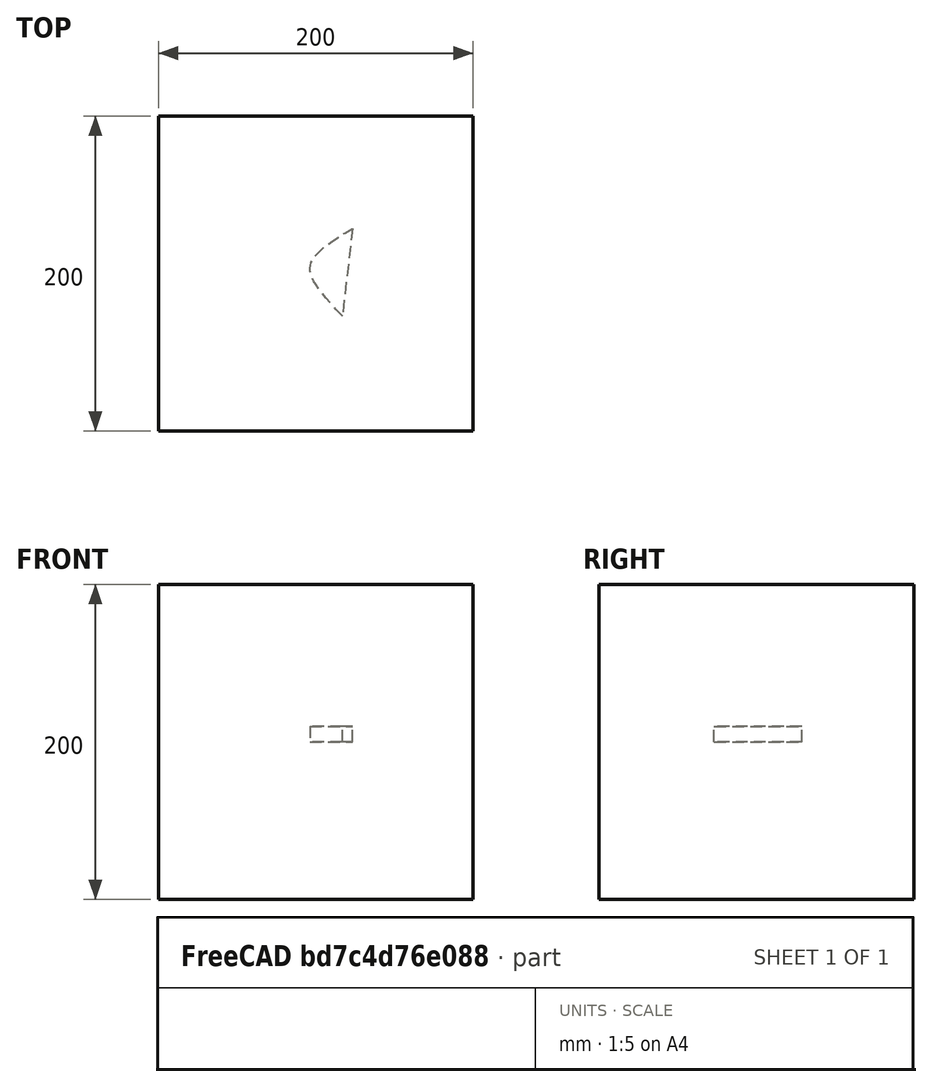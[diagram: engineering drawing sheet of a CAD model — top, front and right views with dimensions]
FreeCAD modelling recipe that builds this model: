
FCSTD DOCUMENT  (FreeCAD 1.0R39109 (Git))
Label: extrudedHyperbola
License: All rights reserved
LicenseURL: http://en.wikipedia.org/wiki/All_rights_reserved
objects: App::DocumentObjectGroupPython×1248, App::Part×2, Part::FeaturePython×1, Sketcher::SketchObject×1, Part::Extrusion×1
note: 4 computed .brp shape members not serialized (recipe doc carries the construction recipe); baked Part::Feature solids carry a one-line shape summary decoded from their .brp

FEATURE [App::DocumentObjectGroupPython] HALFPI  # scripted group (container) (typed FeaturePython)
  name = HALFPI
  value = pi/2.
FEATURE [App::DocumentObjectGroupPython] PI  # scripted group (container) (typed FeaturePython)
  name = PI
  value = 1.*pi
FEATURE [App::DocumentObjectGroupPython] TWOPI  # scripted group (container) (typed FeaturePython)
  name = TWOPI
  value = 2.*pi
FEATURE [App::DocumentObjectGroupPython] Constants  # scripted group (container) (typed FeaturePython)
  Group = -> [HALFPI,PI,TWOPI]
FEATURE [App::DocumentObjectGroupPython] Variables  # scripted group (container) (typed FeaturePython)
FEATURE [App::DocumentObjectGroupPython] Quantities  # scripted group (container) (typed FeaturePython)
FEATURE [App::DocumentObjectGroupPython] Isotopes  # scripted group (container) (typed FeaturePython)
FEATURE [App::DocumentObjectGroupPython] Elements  # scripted group (container) (typed FeaturePython)
FEATURE [App::DocumentObjectGroupPython] G4Isotopes  # scripted group (container) (typed FeaturePython)
FEATURE [App::DocumentObjectGroupPython] H_element  # scripted group (container) (typed FeaturePython)
  Z = 1
  atom_value = 1.008
  formula = H
  name = H_element
FEATURE [App::DocumentObjectGroupPython] He_element  # scripted group (container) (typed FeaturePython)
  Z = 2
  atom_value = 4.0026
  formula = He
  name = He_element
FEATURE [App::DocumentObjectGroupPython] Li_element  # scripted group (container) (typed FeaturePython)
  Z = 3
  atom_value = 6.94
  formula = Li
  name = Li_element
FEATURE [App::DocumentObjectGroupPython] Be_element  # scripted group (container) (typed FeaturePython)
  Z = 4
  atom_value = 9.01218
  formula = Be
  name = Be_element
FEATURE [App::DocumentObjectGroupPython] B_element  # scripted group (container) (typed FeaturePython)
  Z = 5
  atom_value = 10.81
  formula = B
  name = B_element
FEATURE [App::DocumentObjectGroupPython] C_element  # scripted group (container) (typed FeaturePython)
  Z = 6
  atom_value = 12.011
  formula = C
  name = C_element
FEATURE [App::DocumentObjectGroupPython] N_element  # scripted group (container) (typed FeaturePython)
  Z = 7
  atom_value = 14.007
  formula = N
  name = N_element
FEATURE [App::DocumentObjectGroupPython] O_element  # scripted group (container) (typed FeaturePython)
  Z = 8
  atom_value = 15.999
  formula = O
  name = O_element
FEATURE [App::DocumentObjectGroupPython] F_element  # scripted group (container) (typed FeaturePython)
  Z = 9
  atom_value = 18.9984
  formula = F
  name = F_element
FEATURE [App::DocumentObjectGroupPython] Ne_element  # scripted group (container) (typed FeaturePython)
  Z = 10
  atom_value = 20.1797
  formula = Ne
  name = Ne_element
FEATURE [App::DocumentObjectGroupPython] Na_element  # scripted group (container) (typed FeaturePython)
  Z = 11
  atom_value = 22.9898
  formula = Na
  name = Na_element
FEATURE [App::DocumentObjectGroupPython] Mg_element  # scripted group (container) (typed FeaturePython)
  Z = 12
  atom_value = 24.305
  formula = Mg
  name = Mg_element
FEATURE [App::DocumentObjectGroupPython] Al_element  # scripted group (container) (typed FeaturePython)
  Z = 13
  atom_value = 26.9815
  formula = Al
  name = Al_element
FEATURE [App::DocumentObjectGroupPython] Si_element  # scripted group (container) (typed FeaturePython)
  Z = 14
  atom_value = 28.085
  formula = Si
  name = Si_element
FEATURE [App::DocumentObjectGroupPython] P_element  # scripted group (container) (typed FeaturePython)
  Z = 15
  atom_value = 30.9738
  formula = P
  name = P_element
FEATURE [App::DocumentObjectGroupPython] S_element  # scripted group (container) (typed FeaturePython)
  Z = 16
  atom_value = 32.06
  formula = S
  name = S_element
FEATURE [App::DocumentObjectGroupPython] Cl_element  # scripted group (container) (typed FeaturePython)
  Z = 17
  atom_value = 35.45
  formula = Cl
  name = Cl_element
FEATURE [App::DocumentObjectGroupPython] Ar_element  # scripted group (container) (typed FeaturePython)
  Z = 18
  atom_value = 39.95
  formula = Ar
  name = Ar_element
FEATURE [App::DocumentObjectGroupPython] K_element  # scripted group (container) (typed FeaturePython)
  Z = 19
  atom_value = 39.0983
  formula = K
  name = K_element
FEATURE [App::DocumentObjectGroupPython] Ca_element  # scripted group (container) (typed FeaturePython)
  Z = 20
  atom_value = 40.078
  formula = Ca
  name = Ca_element
FEATURE [App::DocumentObjectGroupPython] Sc_element  # scripted group (container) (typed FeaturePython)
  Z = 21
  atom_value = 44.9559
  formula = Sc
  name = Sc_element
FEATURE [App::DocumentObjectGroupPython] Ti_element  # scripted group (container) (typed FeaturePython)
  Z = 22
  atom_value = 47.867
  formula = Ti
  name = Ti_element
FEATURE [App::DocumentObjectGroupPython] V_element  # scripted group (container) (typed FeaturePython)
  Z = 23
  atom_value = 50.9415
  formula = V
  name = V_element
FEATURE [App::DocumentObjectGroupPython] Cr_element  # scripted group (container) (typed FeaturePython)
  Z = 24
  atom_value = 51.9961
  formula = Cr
  name = Cr_element
FEATURE [App::DocumentObjectGroupPython] Mn_element  # scripted group (container) (typed FeaturePython)
  Z = 25
  atom_value = 54.938
  formula = Mn
  name = Mn_element
FEATURE [App::DocumentObjectGroupPython] Fe_element  # scripted group (container) (typed FeaturePython)
  Z = 26
  atom_value = 55.845
  formula = Fe
  name = Fe_element
FEATURE [App::DocumentObjectGroupPython] Co_element  # scripted group (container) (typed FeaturePython)
  Z = 27
  atom_value = 58.9332
  formula = Co
  name = Co_element
FEATURE [App::DocumentObjectGroupPython] Ni_element  # scripted group (container) (typed FeaturePython)
  Z = 28
  atom_value = 58.6934
  formula = Ni
  name = Ni_element
FEATURE [App::DocumentObjectGroupPython] Cu_element  # scripted group (container) (typed FeaturePython)
  Z = 29
  atom_value = 63.546
  formula = Cu
  name = Cu_element
FEATURE [App::DocumentObjectGroupPython] Zn_element  # scripted group (container) (typed FeaturePython)
  Z = 30
  atom_value = 65.38
  formula = Zn
  name = Zn_element
FEATURE [App::DocumentObjectGroupPython] Ga_element  # scripted group (container) (typed FeaturePython)
  Z = 31
  atom_value = 69.723
  formula = Ga
  name = Ga_element
FEATURE [App::DocumentObjectGroupPython] Ge_element  # scripted group (container) (typed FeaturePython)
  Z = 32
  atom_value = 72.63
  formula = Ge
  name = Ge_element
FEATURE [App::DocumentObjectGroupPython] As_element  # scripted group (container) (typed FeaturePython)
  Z = 33
  atom_value = 74.9216
  formula = As
  name = As_element
FEATURE [App::DocumentObjectGroupPython] Se_element  # scripted group (container) (typed FeaturePython)
  Z = 34
  atom_value = 78.971
  formula = Se
  name = Se_element
FEATURE [App::DocumentObjectGroupPython] Br_element  # scripted group (container) (typed FeaturePython)
  Z = 35
  atom_value = 79.904
  formula = Br
  name = Br_element
FEATURE [App::DocumentObjectGroupPython] Kr_element  # scripted group (container) (typed FeaturePython)
  Z = 36
  atom_value = 83.798
  formula = Kr
  name = Kr_element
FEATURE [App::DocumentObjectGroupPython] Rb_element  # scripted group (container) (typed FeaturePython)
  Z = 37
  atom_value = 85.4678
  formula = Rb
  name = Rb_element
FEATURE [App::DocumentObjectGroupPython] Sr_element  # scripted group (container) (typed FeaturePython)
  Z = 38
  atom_value = 87.62
  formula = Sr
  name = Sr_element
FEATURE [App::DocumentObjectGroupPython] Y_element  # scripted group (container) (typed FeaturePython)
  Z = 39
  atom_value = 88.9058
  formula = Y
  name = Y_element
FEATURE [App::DocumentObjectGroupPython] Zr_element  # scripted group (container) (typed FeaturePython)
  Z = 40
  atom_value = 91.224
  formula = Zr
  name = Zr_element
FEATURE [App::DocumentObjectGroupPython] Nb_element  # scripted group (container) (typed FeaturePython)
  Z = 41
  atom_value = 92.9064
  formula = Nb
  name = Nb_element
FEATURE [App::DocumentObjectGroupPython] Mo_element  # scripted group (container) (typed FeaturePython)
  Z = 42
  atom_value = 95.95
  formula = Mo
  name = Mo_element
FEATURE [App::DocumentObjectGroupPython] Tc_element  # scripted group (container) (typed FeaturePython)
  Z = 43
  atom_value = 97
  formula = Tc
  name = Tc_element
FEATURE [App::DocumentObjectGroupPython] Ru_element  # scripted group (container) (typed FeaturePython)
  Z = 44
  atom_value = 101.07
  formula = Ru
  name = Ru_element
FEATURE [App::DocumentObjectGroupPython] Rh_element  # scripted group (container) (typed FeaturePython)
  Z = 45
  atom_value = 102.905
  formula = Rh
  name = Rh_element
FEATURE [App::DocumentObjectGroupPython] Pd_element  # scripted group (container) (typed FeaturePython)
  Z = 46
  atom_value = 106.42
  formula = Pd
  name = Pd_element
FEATURE [App::DocumentObjectGroupPython] Ag_element  # scripted group (container) (typed FeaturePython)
  Z = 47
  atom_value = 107.868
  formula = Ag
  name = Ag_element
FEATURE [App::DocumentObjectGroupPython] Cd_element  # scripted group (container) (typed FeaturePython)
  Z = 48
  atom_value = 112.414
  formula = Cd
  name = Cd_element
FEATURE [App::DocumentObjectGroupPython] In_element  # scripted group (container) (typed FeaturePython)
  Z = 49
  atom_value = 114.818
  formula = In
  name = In_element
FEATURE [App::DocumentObjectGroupPython] Sn_element  # scripted group (container) (typed FeaturePython)
  Z = 50
  atom_value = 118.71
  formula = Sn
  name = Sn_element
FEATURE [App::DocumentObjectGroupPython] Sb_element  # scripted group (container) (typed FeaturePython)
  Z = 51
  atom_value = 121.76
  formula = Sb
  name = Sb_element
FEATURE [App::DocumentObjectGroupPython] Te_element  # scripted group (container) (typed FeaturePython)
  Z = 52
  atom_value = 127.6
  formula = Te
  name = Te_element
FEATURE [App::DocumentObjectGroupPython] I_element  # scripted group (container) (typed FeaturePython)
  Z = 53
  atom_value = 126.904
  formula = I
  name = I_element
FEATURE [App::DocumentObjectGroupPython] Xe_element  # scripted group (container) (typed FeaturePython)
  Z = 54
  atom_value = 131.293
  formula = Xe
  name = Xe_element
FEATURE [App::DocumentObjectGroupPython] Cs_element  # scripted group (container) (typed FeaturePython)
  Z = 55
  atom_value = 132.905
  formula = Cs
  name = Cs_element
FEATURE [App::DocumentObjectGroupPython] Ba_element  # scripted group (container) (typed FeaturePython)
  Z = 56
  atom_value = 137.327
  formula = Ba
  name = Ba_element
FEATURE [App::DocumentObjectGroupPython] La_element  # scripted group (container) (typed FeaturePython)
  Z = 57
  atom_value = 138.905
  formula = La
  name = La_element
FEATURE [App::DocumentObjectGroupPython] Ce_element  # scripted group (container) (typed FeaturePython)
  Z = 58
  atom_value = 140.116
  formula = Ce
  name = Ce_element
FEATURE [App::DocumentObjectGroupPython] Pr_element  # scripted group (container) (typed FeaturePython)
  Z = 59
  atom_value = 140.908
  formula = Pr
  name = Pr_element
FEATURE [App::DocumentObjectGroupPython] Nd_element  # scripted group (container) (typed FeaturePython)
  Z = 60
  atom_value = 144.242
  formula = Nd
  name = Nd_element
FEATURE [App::DocumentObjectGroupPython] Pm_element  # scripted group (container) (typed FeaturePython)
  Z = 61
  atom_value = 145
  formula = Pm
  name = Pm_element
FEATURE [App::DocumentObjectGroupPython] Sm_element  # scripted group (container) (typed FeaturePython)
  Z = 62
  atom_value = 150.36
  formula = Sm
  name = Sm_element
FEATURE [App::DocumentObjectGroupPython] Eu_element  # scripted group (container) (typed FeaturePython)
  Z = 63
  atom_value = 151.964
  formula = Eu
  name = Eu_element
FEATURE [App::DocumentObjectGroupPython] Gd_element  # scripted group (container) (typed FeaturePython)
  Z = 64
  atom_value = 157.25
  formula = Gd
  name = Gd_element
FEATURE [App::DocumentObjectGroupPython] Tb_element  # scripted group (container) (typed FeaturePython)
  Z = 65
  atom_value = 158.925
  formula = Tb
  name = Tb_element
FEATURE [App::DocumentObjectGroupPython] Dy_element  # scripted group (container) (typed FeaturePython)
  Z = 66
  atom_value = 162.5
  formula = Dy
  name = Dy_element
FEATURE [App::DocumentObjectGroupPython] Ho_element  # scripted group (container) (typed FeaturePython)
  Z = 67
  atom_value = 164.93
  formula = Ho
  name = Ho_element
FEATURE [App::DocumentObjectGroupPython] Er_element  # scripted group (container) (typed FeaturePython)
  Z = 68
  atom_value = 167.259
  formula = Er
  name = Er_element
FEATURE [App::DocumentObjectGroupPython] Tm_element  # scripted group (container) (typed FeaturePython)
  Z = 69
  atom_value = 168.934
  formula = Tm
  name = Tm_element
FEATURE [App::DocumentObjectGroupPython] Yb_element  # scripted group (container) (typed FeaturePython)
  Z = 70
  atom_value = 173.045
  formula = Yb
  name = Yb_element
FEATURE [App::DocumentObjectGroupPython] Lu_element  # scripted group (container) (typed FeaturePython)
  Z = 71
  atom_value = 174.967
  formula = Lu
  name = Lu_element
FEATURE [App::DocumentObjectGroupPython] Hf_element  # scripted group (container) (typed FeaturePython)
  Z = 72
  atom_value = 178.49
  formula = Hf
  name = Hf_element
FEATURE [App::DocumentObjectGroupPython] Ta_element  # scripted group (container) (typed FeaturePython)
  Z = 73
  atom_value = 180.948
  formula = Ta
  name = Ta_element
FEATURE [App::DocumentObjectGroupPython] W_element  # scripted group (container) (typed FeaturePython)
  Z = 74
  atom_value = 183.84
  formula = W
  name = W_element
FEATURE [App::DocumentObjectGroupPython] Re_element  # scripted group (container) (typed FeaturePython)
  Z = 75
  atom_value = 186.207
  formula = Re
  name = Re_element
FEATURE [App::DocumentObjectGroupPython] Os_element  # scripted group (container) (typed FeaturePython)
  Z = 76
  atom_value = 190.23
  formula = Os
  name = Os_element
FEATURE [App::DocumentObjectGroupPython] Ir_element  # scripted group (container) (typed FeaturePython)
  Z = 77
  atom_value = 192.217
  formula = Ir
  name = Ir_element
FEATURE [App::DocumentObjectGroupPython] Pt_element  # scripted group (container) (typed FeaturePython)
  Z = 78
  atom_value = 195.084
  formula = Pt
  name = Pt_element
FEATURE [App::DocumentObjectGroupPython] Au_element  # scripted group (container) (typed FeaturePython)
  Z = 79
  atom_value = 196.967
  formula = Au
  name = Au_element
FEATURE [App::DocumentObjectGroupPython] Hg_element  # scripted group (container) (typed FeaturePython)
  Z = 80
  atom_value = 200.592
  formula = Hg
  name = Hg_element
FEATURE [App::DocumentObjectGroupPython] Tl_element  # scripted group (container) (typed FeaturePython)
  Z = 81
  atom_value = 204.38
  formula = Tl
  name = Tl_element
FEATURE [App::DocumentObjectGroupPython] Pb_element  # scripted group (container) (typed FeaturePython)
  Z = 82
  atom_value = 207.2
  formula = Pb
  name = Pb_element
FEATURE [App::DocumentObjectGroupPython] Bi_element  # scripted group (container) (typed FeaturePython)
  Z = 83
  atom_value = 208.98
  formula = Bi
  name = Bi_element
FEATURE [App::DocumentObjectGroupPython] Po_element  # scripted group (container) (typed FeaturePython)
  Z = 84
  atom_value = 209
  formula = Po
  name = Po_element
FEATURE [App::DocumentObjectGroupPython] At_element  # scripted group (container) (typed FeaturePython)
  Z = 85
  atom_value = 210
  formula = At
  name = At_element
FEATURE [App::DocumentObjectGroupPython] Rn_element  # scripted group (container) (typed FeaturePython)
  Z = 86
  atom_value = 222
  formula = Rn
  name = Rn_element
FEATURE [App::DocumentObjectGroupPython] Fr_element  # scripted group (container) (typed FeaturePython)
  Z = 87
  atom_value = 223
  formula = Fr
  name = Fr_element
FEATURE [App::DocumentObjectGroupPython] Ra_element  # scripted group (container) (typed FeaturePython)
  Z = 88
  atom_value = 226
  formula = Ra
  name = Ra_element
FEATURE [App::DocumentObjectGroupPython] Ac_element  # scripted group (container) (typed FeaturePython)
  Z = 89
  atom_value = 227
  formula = Ac
  name = Ac_element
FEATURE [App::DocumentObjectGroupPython] Th_element  # scripted group (container) (typed FeaturePython)
  Z = 90
  atom_value = 232.038
  formula = Th
  name = Th_element
FEATURE [App::DocumentObjectGroupPython] Pa_element  # scripted group (container) (typed FeaturePython)
  Z = 91
  atom_value = 231.036
  formula = Pa
  name = Pa_element
FEATURE [App::DocumentObjectGroupPython] U_element  # scripted group (container) (typed FeaturePython)
  Z = 92
  atom_value = 238.029
  formula = U
  name = U_element
FEATURE [App::DocumentObjectGroupPython] Np_element  # scripted group (container) (typed FeaturePython)
  Z = 93
  atom_value = 237
  formula = Np
  name = Np_element
FEATURE [App::DocumentObjectGroupPython] Pu_element  # scripted group (container) (typed FeaturePython)
  Z = 94
  atom_value = 244
  formula = Pu
  name = Pu_element
FEATURE [App::DocumentObjectGroupPython] Am_element  # scripted group (container) (typed FeaturePython)
  Z = 95
  atom_value = 243
  formula = Am
  name = Am_element
FEATURE [App::DocumentObjectGroupPython] Cm_element  # scripted group (container) (typed FeaturePython)
  Z = 96
  atom_value = 247
  formula = Cm
  name = Cm_element
FEATURE [App::DocumentObjectGroupPython] Bk_element  # scripted group (container) (typed FeaturePython)
  Z = 97
  atom_value = 247
  formula = Bk
  name = Bk_element
FEATURE [App::DocumentObjectGroupPython] Cf_element  # scripted group (container) (typed FeaturePython)
  Z = 98
  atom_value = 251
  formula = Cf
  name = Cf_element
FEATURE [App::DocumentObjectGroupPython] G4Elements  # scripted group (container) (typed FeaturePython)
  Group = -> [H_element,He_element,Li_element,Be_element,B_element,C_element,N_element,O_element,F_element,Ne_element,Na_element,Mg_element,Al_element,Si_element,P_element,S_element,Cl_element,Ar_element,K_element,Ca_element,Sc_element,Ti_element,V_element,Cr_element,Mn_element,Fe_element,Co_element,Ni_element,Cu_element,Zn_element,Ga_element,Ge_element,As_element,Se_element,Br_element,Kr_element,Rb_element,+61 more]
FEATURE [App::DocumentObjectGroupPython] H_element001  label="H_element : 0.101"  # scripted group (container) (typed FeaturePython)
  n = 0.101327
FEATURE [App::DocumentObjectGroupPython] C_element001  label="C_element : 0.775"  # scripted group (container) (typed FeaturePython)
  n = 0.7755
FEATURE [App::DocumentObjectGroupPython] N_element001  label="N_element : 0.035"  # scripted group (container) (typed FeaturePython)
  n = 0.035057
FEATURE [App::DocumentObjectGroupPython] O_element001  label="O_element : 0.052"  # scripted group (container) (typed FeaturePython)
  n = 0.0523159
FEATURE [App::DocumentObjectGroupPython] F_element001  label="F_element : 0.017"  # scripted group (container) (typed FeaturePython)
  n = 0.017422
FEATURE [App::DocumentObjectGroupPython] Ca_element001  label="Ca_element : 0.018"  # scripted group (container) (typed FeaturePython)
  n = 0.018378
FEATURE [App::DocumentObjectGroupPython] G4_A_150_TISSUE  label="G4_A-150_TISSUE"  # scripted group (container) (typed FeaturePython)
  Dunit = g/cm3
  Dvalue = 1.127
  Group = -> [H_element001,C_element001,N_element001,O_element001,F_element001,Ca_element001]
  conduct = 2
  density = 1
  expand = 3
  formula = G4_A-150_TISSUE
  name = G4_A-150_TISSUE
  specific = 4
FEATURE [App::DocumentObjectGroupPython] C_element002  label="C_element : 3"  # scripted group (container) (typed FeaturePython)
  n = 3
  ref = C_element
FEATURE [App::DocumentObjectGroupPython] H_element002  label="H_element : 6"  # scripted group (container) (typed FeaturePython)
  n = 6
  ref = H_element
FEATURE [App::DocumentObjectGroupPython] O_element002  label="O_element : 1"  # scripted group (container) (typed FeaturePython)
  n = 1
  ref = O_element
FEATURE [App::DocumentObjectGroupPython] G4_ACETONE  # scripted group (container) (typed FeaturePython)
  Dunit = g/cm3
  Dvalue = 0.7899
  Group = -> [C_element002,H_element002,O_element002]
  conduct = 2
  density = 1
  expand = 3
  formula = G4_ACETONE
  name = G4_ACETONE
  specific = 4
FEATURE [App::DocumentObjectGroupPython] C_element003  label="C_element : 2"  # scripted group (container) (typed FeaturePython)
  n = 2
  ref = C_element
FEATURE [App::DocumentObjectGroupPython] H_element003  label="H_element : 2"  # scripted group (container) (typed FeaturePython)
  n = 2
  ref = H_element
FEATURE [App::DocumentObjectGroupPython] G4_ACETYLENE  # scripted group (container) (typed FeaturePython)
  Dunit = g/cm3
  Dvalue = 0.0010967
  Group = -> [C_element003,H_element003]
  conduct = 2
  density = 1
  expand = 3
  formula = G4_ACETYLENE
  name = G4_ACETYLENE
  specific = 4
FEATURE [App::DocumentObjectGroupPython] C_element004  label="C_element : 5"  # scripted group (container) (typed FeaturePython)
  n = 5
  ref = C_element
FEATURE [App::DocumentObjectGroupPython] H_element004  label="H_element : 5"  # scripted group (container) (typed FeaturePython)
  n = 5
  ref = H_element
FEATURE [App::DocumentObjectGroupPython] N_element002  label="N_element : 5"  # scripted group (container) (typed FeaturePython)
  n = 5
  ref = N_element
FEATURE [App::DocumentObjectGroupPython] G4_ADENINE  # scripted group (container) (typed FeaturePython)
  Dunit = g/cm3
  Dvalue = 1.6
  Group = -> [C_element004,H_element004,N_element002]
  conduct = 2
  density = 1
  expand = 3
  formula = G4_ADENINE
  name = G4_ADENINE
  specific = 4
FEATURE [App::DocumentObjectGroupPython] H_element005  label="H_element : 0.114"  # scripted group (container) (typed FeaturePython)
  n = 0.114
FEATURE [App::DocumentObjectGroupPython] C_element005  label="C_element : 0.598"  # scripted group (container) (typed FeaturePython)
  n = 0.598
FEATURE [App::DocumentObjectGroupPython] N_element003  label="N_element : 0.007"  # scripted group (container) (typed FeaturePython)
  n = 0.007
FEATURE [App::DocumentObjectGroupPython] O_element003  label="O_element : 0.278"  # scripted group (container) (typed FeaturePython)
  n = 0.278
FEATURE [App::DocumentObjectGroupPython] Na_element001  label="Na_element : 0.001"  # scripted group (container) (typed FeaturePython)
  n = 0.001
FEATURE [App::DocumentObjectGroupPython] S_element001  label="S_element : 0.001"  # scripted group (container) (typed FeaturePython)
  n = 0.001
FEATURE [App::DocumentObjectGroupPython] Cl_element001  label="Cl_element : 0.001"  # scripted group (container) (typed FeaturePython)
  n = 0.001
FEATURE [App::DocumentObjectGroupPython] G4_ADIPOSE_TISSUE_ICRP  # scripted group (container) (typed FeaturePython)
  Dunit = g/cm3
  Dvalue = 0.95
  Group = -> [H_element005,C_element005,N_element003,O_element003,Na_element001,S_element001,Cl_element001]
  conduct = 2
  density = 1
  expand = 3
  formula = G4_ADIPOSE_TISSUE_ICRP
  name = G4_ADIPOSE_TISSUE_ICRP
  specific = 4
FEATURE [App::DocumentObjectGroupPython] C_element006  label="C_element : 0.000"  # scripted group (container) (typed FeaturePython)
  n = 0.000124
FEATURE [App::DocumentObjectGroupPython] N_element004  label="N_element : 0.755"  # scripted group (container) (typed FeaturePython)
  n = 0.755268
FEATURE [App::DocumentObjectGroupPython] O_element004  label="O_element : 0.232"  # scripted group (container) (typed FeaturePython)
  n = 0.231781
FEATURE [App::DocumentObjectGroupPython] Ar_element001  label="Ar_element : 0.013"  # scripted group (container) (typed FeaturePython)
  n = 0.012827
FEATURE [App::DocumentObjectGroupPython] G4_AIR  # scripted group (container) (typed FeaturePython)
  Dunit = g/cm3
  Dvalue = 0.00120479
  Group = -> [C_element006,N_element004,O_element004,Ar_element001]
  conduct = 2
  density = 1
  expand = 3
  formula = G4_AIR
  name = G4_AIR
  specific = 4
FEATURE [App::DocumentObjectGroupPython] C_element007  label="C_element : 006"  # scripted group (container) (typed FeaturePython)
  n = 3
  ref = C_element
FEATURE [App::DocumentObjectGroupPython] H_element006  label="H_element : 7"  # scripted group (container) (typed FeaturePython)
  n = 7
  ref = H_element
FEATURE [App::DocumentObjectGroupPython] N_element005  label="N_element : 1"  # scripted group (container) (typed FeaturePython)
  n = 1
  ref = N_element
FEATURE [App::DocumentObjectGroupPython] O_element005  label="O_element : 2"  # scripted group (container) (typed FeaturePython)
  n = 2
  ref = O_element
FEATURE [App::DocumentObjectGroupPython] G4_ALANINE  # scripted group (container) (typed FeaturePython)
  Dunit = g/cm3
  Dvalue = 1.42
  Group = -> [C_element007,H_element006,N_element005,O_element005]
  conduct = 2
  density = 1
  expand = 3
  formula = G4_ALANINE
  name = G4_ALANINE
  specific = 4
FEATURE [App::DocumentObjectGroupPython] Al_element001  label="Al_element : 2"  # scripted group (container) (typed FeaturePython)
  n = 2
  ref = Al_element
FEATURE [App::DocumentObjectGroupPython] O_element006  label="O_element : 3"  # scripted group (container) (typed FeaturePython)
  n = 3
  ref = O_element
FEATURE [App::DocumentObjectGroupPython] G4_ALUMINUM_OXIDE  # scripted group (container) (typed FeaturePython)
  Dunit = g/cm3
  Dvalue = 3.97
  Group = -> [Al_element001,O_element006]
  conduct = 2
  density = 1
  expand = 3
  formula = G4_ALUMINUM_OXIDE
  name = G4_ALUMINUM_OXIDE
  specific = 4
FEATURE [App::DocumentObjectGroupPython] H_element007  label="H_element : 0.106"  # scripted group (container) (typed FeaturePython)
  n = 0.10593
FEATURE [App::DocumentObjectGroupPython] C_element008  label="C_element : 0.789"  # scripted group (container) (typed FeaturePython)
  n = 0.788974
FEATURE [App::DocumentObjectGroupPython] O_element007  label="O_element : 0.105"  # scripted group (container) (typed FeaturePython)
  n = 0.105096
FEATURE [App::DocumentObjectGroupPython] G4_AMBER  # scripted group (container) (typed FeaturePython)
  Dunit = g/cm3
  Dvalue = 1.1
  Group = -> [H_element007,C_element008,O_element007]
  conduct = 2
  density = 1
  expand = 3
  formula = G4_AMBER
  name = G4_AMBER
  specific = 4
FEATURE [App::DocumentObjectGroupPython] N_element006  label="N_element : 006"  # scripted group (container) (typed FeaturePython)
  n = 1
  ref = N_element
FEATURE [App::DocumentObjectGroupPython] H_element008  label="H_element : 3"  # scripted group (container) (typed FeaturePython)
  n = 3
  ref = H_element
FEATURE [App::DocumentObjectGroupPython] G4_AMMONIA  # scripted group (container) (typed FeaturePython)
  Dunit = g/cm3
  Dvalue = 0.000826019
  Group = -> [N_element006,H_element008]
  conduct = 2
  density = 1
  expand = 3
  formula = G4_AMMONIA
  name = G4_AMMONIA
  specific = 4
FEATURE [App::DocumentObjectGroupPython] C_element009  label="C_element : 6"  # scripted group (container) (typed FeaturePython)
  n = 6
  ref = C_element
FEATURE [App::DocumentObjectGroupPython] H_element009  label="H_element : 008"  # scripted group (container) (typed FeaturePython)
  n = 7
  ref = H_element
FEATURE [App::DocumentObjectGroupPython] N_element007  label="N_element : 007"  # scripted group (container) (typed FeaturePython)
  n = 1
  ref = N_element
FEATURE [App::DocumentObjectGroupPython] G4_ANILINE  # scripted group (container) (typed FeaturePython)
  Dunit = g/cm3
  Dvalue = 1.0235
  Group = -> [C_element009,H_element009,N_element007]
  conduct = 2
  density = 1
  expand = 3
  formula = G4_ANILINE
  name = G4_ANILINE
  specific = 4
FEATURE [App::DocumentObjectGroupPython] C_element010  label="C_element : 14"  # scripted group (container) (typed FeaturePython)
  n = 14
  ref = C_element
FEATURE [App::DocumentObjectGroupPython] H_element010  label="H_element : 10"  # scripted group (container) (typed FeaturePython)
  n = 10
  ref = H_element
FEATURE [App::DocumentObjectGroupPython] G4_ANTHRACENE  # scripted group (container) (typed FeaturePython)
  Dunit = g/cm3
  Dvalue = 1.283
  Group = -> [C_element010,H_element010]
  conduct = 2
  density = 1
  expand = 3
  formula = G4_ANTHRACENE
  name = G4_ANTHRACENE
  specific = 4
FEATURE [App::DocumentObjectGroupPython] H_element011  label="H_element : 0.065"  # scripted group (container) (typed FeaturePython)
  n = 0.0654709
FEATURE [App::DocumentObjectGroupPython] C_element011  label="C_element : 0.537"  # scripted group (container) (typed FeaturePython)
  n = 0.536944
FEATURE [App::DocumentObjectGroupPython] N_element008  label="N_element : 0.021"  # scripted group (container) (typed FeaturePython)
  n = 0.0215
FEATURE [App::DocumentObjectGroupPython] O_element008  label="O_element : 0.032"  # scripted group (container) (typed FeaturePython)
  n = 0.032085
FEATURE [App::DocumentObjectGroupPython] F_element002  label="F_element : 0.167"  # scripted group (container) (typed FeaturePython)
  n = 0.167411
FEATURE [App::DocumentObjectGroupPython] Ca_element002  label="Ca_element : 0.177"  # scripted group (container) (typed FeaturePython)
  n = 0.176589
FEATURE [App::DocumentObjectGroupPython] G4_B_100_BONE  label="G4_B-100_BONE"  # scripted group (container) (typed FeaturePython)
  Dunit = g/cm3
  Dvalue = 1.45
  Group = -> [H_element011,C_element011,N_element008,O_element008,F_element002,Ca_element002]
  conduct = 2
  density = 1
  expand = 3
  formula = G4_B-100_BONE
  name = G4_B-100_BONE
  specific = 4
FEATURE [App::DocumentObjectGroupPython] H_element012  label="H_element : 0.057"  # scripted group (container) (typed FeaturePython)
  n = 0.057441
FEATURE [App::DocumentObjectGroupPython] C_element012  label="C_element : 0.790"  # scripted group (container) (typed FeaturePython)
  n = 0.774591
FEATURE [App::DocumentObjectGroupPython] O_element009  label="O_element : 0.168"  # scripted group (container) (typed FeaturePython)
  n = 0.167968
FEATURE [App::DocumentObjectGroupPython] G4_BAKELITE  # scripted group (container) (typed FeaturePython)
  Dunit = g/cm3
  Dvalue = 1.25
  Group = -> [H_element012,C_element012,O_element009]
  conduct = 2
  density = 1
  expand = 3
  formula = G4_BAKELITE
  name = G4_BAKELITE
  specific = 4
FEATURE [App::DocumentObjectGroupPython] Ba_element001  label="Ba_element : 1"  # scripted group (container) (typed FeaturePython)
  n = 1
  ref = Ba_element
FEATURE [App::DocumentObjectGroupPython] F_element003  label="F_element : 2"  # scripted group (container) (typed FeaturePython)
  n = 2
  ref = F_element
FEATURE [App::DocumentObjectGroupPython] G4_BARIUM_FLUORIDE  # scripted group (container) (typed FeaturePython)
  Dunit = g/cm3
  Dvalue = 4.89
  Group = -> [Ba_element001,F_element003]
  conduct = 2
  density = 1
  expand = 3
  formula = G4_BARIUM_FLUORIDE
  name = G4_BARIUM_FLUORIDE
  specific = 4
FEATURE [App::DocumentObjectGroupPython] Ba_element002  label="Ba_element : 002"  # scripted group (container) (typed FeaturePython)
  n = 1
  ref = Ba_element
FEATURE [App::DocumentObjectGroupPython] S_element002  label="S_element : 1"  # scripted group (container) (typed FeaturePython)
  n = 1
  ref = S_element
FEATURE [App::DocumentObjectGroupPython] O_element010  label="O_element : 4"  # scripted group (container) (typed FeaturePython)
  n = 4
  ref = O_element
FEATURE [App::DocumentObjectGroupPython] G4_BARIUM_SULFATE  # scripted group (container) (typed FeaturePython)
  Dunit = g/cm3
  Dvalue = 4.5
  Group = -> [Ba_element002,S_element002,O_element010]
  conduct = 2
  density = 1
  expand = 3
  formula = G4_BARIUM_SULFATE
  name = G4_BARIUM_SULFATE
  specific = 4
FEATURE [App::DocumentObjectGroupPython] C_element013  label="C_element : 007"  # scripted group (container) (typed FeaturePython)
  n = 6
  ref = C_element
FEATURE [App::DocumentObjectGroupPython] H_element013  label="H_element : 009"  # scripted group (container) (typed FeaturePython)
  n = 6
  ref = H_element
FEATURE [App::DocumentObjectGroupPython] G4_BENZENE  # scripted group (container) (typed FeaturePython)
  Dunit = g/cm3
  Dvalue = 0.87865
  Group = -> [C_element013,H_element013]
  conduct = 2
  density = 1
  expand = 3
  formula = G4_BENZENE
  name = G4_BENZENE
  specific = 4
FEATURE [App::DocumentObjectGroupPython] Be_element001  label="Be_element : 1"  # scripted group (container) (typed FeaturePython)
  n = 1
  ref = Be_element
FEATURE [App::DocumentObjectGroupPython] O_element011  label="O_element : 005"  # scripted group (container) (typed FeaturePython)
  n = 1
  ref = O_element
FEATURE [App::DocumentObjectGroupPython] G4_BERYLLIUM_OXIDE  # scripted group (container) (typed FeaturePython)
  Dunit = g/cm3
  Dvalue = 3.01
  Group = -> [Be_element001,O_element011]
  conduct = 2
  density = 1
  expand = 3
  formula = G4_BERYLLIUM_OXIDE
  name = G4_BERYLLIUM_OXIDE
  specific = 4
FEATURE [App::DocumentObjectGroupPython] Bi_element001  label="Bi_element : 4"  # scripted group (container) (typed FeaturePython)
  n = 4
  ref = Bi_element
FEATURE [App::DocumentObjectGroupPython] Ge_element001  label="Ge_element : 3"  # scripted group (container) (typed FeaturePython)
  n = 3
  ref = Ge_element
FEATURE [App::DocumentObjectGroupPython] O_element012  label="O_element : 12"  # scripted group (container) (typed FeaturePython)
  n = 12
  ref = O_element
FEATURE [App::DocumentObjectGroupPython] G4_BGO  # scripted group (container) (typed FeaturePython)
  Dunit = g/cm3
  Dvalue = 7.13
  Group = -> [Bi_element001,Ge_element001,O_element012]
  conduct = 2
  density = 1
  expand = 3
  formula = G4_BGO
  name = G4_BGO
  specific = 4
FEATURE [App::DocumentObjectGroupPython] H_element014  label="H_element : 0.102"  # scripted group (container) (typed FeaturePython)
  n = 0.102
FEATURE [App::DocumentObjectGroupPython] C_element014  label="C_element : 0.110"  # scripted group (container) (typed FeaturePython)
  n = 0.11
FEATURE [App::DocumentObjectGroupPython] N_element009  label="N_element : 0.033"  # scripted group (container) (typed FeaturePython)
  n = 0.033
FEATURE [App::DocumentObjectGroupPython] O_element013  label="O_element : 0.745"  # scripted group (container) (typed FeaturePython)
  n = 0.745
FEATURE [App::DocumentObjectGroupPython] Na_element002  label="Na_element : 0.002"  # scripted group (container) (typed FeaturePython)
  n = 0.001
FEATURE [App::DocumentObjectGroupPython] P_element001  label="P_element : 0.001"  # scripted group (container) (typed FeaturePython)
  n = 0.001
FEATURE [App::DocumentObjectGroupPython] S_element003  label="S_element : 0.002"  # scripted group (container) (typed FeaturePython)
  n = 0.002
FEATURE [App::DocumentObjectGroupPython] Cl_element002  label="Cl_element : 0.003"  # scripted group (container) (typed FeaturePython)
  n = 0.003
FEATURE [App::DocumentObjectGroupPython] K_element001  label="K_element : 0.002"  # scripted group (container) (typed FeaturePython)
  n = 0.002
FEATURE [App::DocumentObjectGroupPython] Fe_element001  label="Fe_element : 0.001"  # scripted group (container) (typed FeaturePython)
  n = 0.001
FEATURE [App::DocumentObjectGroupPython] G4_BLOOD_ICRP  # scripted group (container) (typed FeaturePython)
  Dunit = g/cm3
  Dvalue = 1.06
  Group = -> [H_element014,C_element014,N_element009,O_element013,Na_element002,P_element001,S_element003,Cl_element002,K_element001,Fe_element001]
  conduct = 2
  density = 1
  expand = 3
  formula = G4_BLOOD_ICRP
  name = G4_BLOOD_ICRP
  specific = 4
FEATURE [App::DocumentObjectGroupPython] H_element015  label="H_element : 0.064"  # scripted group (container) (typed FeaturePython)
  n = 0.064
FEATURE [App::DocumentObjectGroupPython] C_element015  label="C_element : 0.278"  # scripted group (container) (typed FeaturePython)
  n = 0.278
FEATURE [App::DocumentObjectGroupPython] N_element010  label="N_element : 0.027"  # scripted group (container) (typed FeaturePython)
  n = 0.027
FEATURE [App::DocumentObjectGroupPython] O_element014  label="O_element : 0.410"  # scripted group (container) (typed FeaturePython)
  n = 0.41
FEATURE [App::DocumentObjectGroupPython] Mg_element001  label="Mg_element : 0.002"  # scripted group (container) (typed FeaturePython)
  n = 0.002
FEATURE [App::DocumentObjectGroupPython] P_element002  label="P_element : 0.070"  # scripted group (container) (typed FeaturePython)
  n = 0.07
FEATURE [App::DocumentObjectGroupPython] S_element004  label="S_element : 0.003"  # scripted group (container) (typed FeaturePython)
  n = 0.002
FEATURE [App::DocumentObjectGroupPython] Ca_element003  label="Ca_element : 0.147"  # scripted group (container) (typed FeaturePython)
  n = 0.147
FEATURE [App::DocumentObjectGroupPython] G4_BONE_COMPACT_ICRU  # scripted group (container) (typed FeaturePython)
  Dunit = g/cm3
  Dvalue = 1.85
  Group = -> [H_element015,C_element015,N_element010,O_element014,Mg_element001,P_element002,S_element004,Ca_element003]
  conduct = 2
  density = 1
  expand = 3
  formula = G4_BONE_COMPACT_ICRU
  name = G4_BONE_COMPACT_ICRU
  specific = 4
FEATURE [App::DocumentObjectGroupPython] H_element016  label="H_element : 0.034"  # scripted group (container) (typed FeaturePython)
  n = 0.034
FEATURE [App::DocumentObjectGroupPython] C_element016  label="C_element : 0.155"  # scripted group (container) (typed FeaturePython)
  n = 0.155
FEATURE [App::DocumentObjectGroupPython] N_element011  label="N_element : 0.042"  # scripted group (container) (typed FeaturePython)
  n = 0.042
FEATURE [App::DocumentObjectGroupPython] O_element015  label="O_element : 0.435"  # scripted group (container) (typed FeaturePython)
  n = 0.435
FEATURE [App::DocumentObjectGroupPython] Na_element003  label="Na_element : 0.003"  # scripted group (container) (typed FeaturePython)
  n = 0.001
FEATURE [App::DocumentObjectGroupPython] Mg_element002  label="Mg_element : 0.003"  # scripted group (container) (typed FeaturePython)
  n = 0.002
FEATURE [App::DocumentObjectGroupPython] P_element003  label="P_element : 0.103"  # scripted group (container) (typed FeaturePython)
  n = 0.103
FEATURE [App::DocumentObjectGroupPython] S_element005  label="S_element : 0.004"  # scripted group (container) (typed FeaturePython)
  n = 0.003
FEATURE [App::DocumentObjectGroupPython] Ca_element004  label="Ca_element : 0.225"  # scripted group (container) (typed FeaturePython)
  n = 0.225
FEATURE [App::DocumentObjectGroupPython] G4_BONE_CORTICAL_ICRP  # scripted group (container) (typed FeaturePython)
  Dunit = g/cm3
  Dvalue = 1.92
  Group = -> [H_element016,C_element016,N_element011,O_element015,Na_element003,Mg_element002,P_element003,S_element005,Ca_element004]
  conduct = 2
  density = 1
  expand = 3
  formula = G4_BONE_CORTICAL_ICRP
  name = G4_BONE_CORTICAL_ICRP
  specific = 4
FEATURE [App::DocumentObjectGroupPython] B_element001  label="B_element : 4"  # scripted group (container) (typed FeaturePython)
  n = 4
  ref = B_element
FEATURE [App::DocumentObjectGroupPython] C_element017  label="C_element : 1"  # scripted group (container) (typed FeaturePython)
  n = 1
  ref = C_element
FEATURE [App::DocumentObjectGroupPython] G4_BORON_CARBIDE  # scripted group (container) (typed FeaturePython)
  Dunit = g/cm3
  Dvalue = 2.52
  Group = -> [B_element001,C_element017]
  conduct = 2
  density = 1
  expand = 3
  formula = G4_BORON_CARBIDE
  name = G4_BORON_CARBIDE
  specific = 4
FEATURE [App::DocumentObjectGroupPython] B_element002  label="B_element : 2"  # scripted group (container) (typed FeaturePython)
  n = 2
  ref = B_element
FEATURE [App::DocumentObjectGroupPython] O_element016  label="O_element : 006"  # scripted group (container) (typed FeaturePython)
  n = 3
  ref = O_element
FEATURE [App::DocumentObjectGroupPython] G4_BORON_OXIDE  # scripted group (container) (typed FeaturePython)
  Dunit = g/cm3
  Dvalue = 1.812
  Group = -> [B_element002,O_element016]
  conduct = 2
  density = 1
  expand = 3
  formula = G4_BORON_OXIDE
  name = G4_BORON_OXIDE
  specific = 4
FEATURE [App::DocumentObjectGroupPython] H_element017  label="H_element : 0.107"  # scripted group (container) (typed FeaturePython)
  n = 0.107
FEATURE [App::DocumentObjectGroupPython] C_element018  label="C_element : 0.145"  # scripted group (container) (typed FeaturePython)
  n = 0.145
FEATURE [App::DocumentObjectGroupPython] N_element012  label="N_element : 0.022"  # scripted group (container) (typed FeaturePython)
  n = 0.022
FEATURE [App::DocumentObjectGroupPython] O_element017  label="O_element : 0.712"  # scripted group (container) (typed FeaturePython)
  n = 0.712
FEATURE [App::DocumentObjectGroupPython] Na_element004  label="Na_element : 0.004"  # scripted group (container) (typed FeaturePython)
  n = 0.002
FEATURE [App::DocumentObjectGroupPython] P_element004  label="P_element : 0.004"  # scripted group (container) (typed FeaturePython)
  n = 0.004
FEATURE [App::DocumentObjectGroupPython] S_element006  label="S_element : 0.005"  # scripted group (container) (typed FeaturePython)
  n = 0.002
FEATURE [App::DocumentObjectGroupPython] Cl_element003  label="Cl_element : 0.004"  # scripted group (container) (typed FeaturePython)
  n = 0.003
FEATURE [App::DocumentObjectGroupPython] K_element002  label="K_element : 0.003"  # scripted group (container) (typed FeaturePython)
  n = 0.003
FEATURE [App::DocumentObjectGroupPython] G4_BRAIN_ICRP  # scripted group (container) (typed FeaturePython)
  Dunit = g/cm3
  Dvalue = 1.04
  Group = -> [H_element017,C_element018,N_element012,O_element017,Na_element004,P_element004,S_element006,Cl_element003,K_element002]
  conduct = 2
  density = 1
  expand = 3
  formula = G4_BRAIN_ICRP
  name = G4_BRAIN_ICRP
  specific = 4
FEATURE [App::DocumentObjectGroupPython] C_element019  label="C_element : 4"  # scripted group (container) (typed FeaturePython)
  n = 4
  ref = C_element
FEATURE [App::DocumentObjectGroupPython] H_element018  label="H_element : 010"  # scripted group (container) (typed FeaturePython)
  n = 10
  ref = H_element
FEATURE [App::DocumentObjectGroupPython] G4_BUTANE  # scripted group (container) (typed FeaturePython)
  Dunit = g/cm3
  Dvalue = 0.00249343
  Group = -> [C_element019,H_element018]
  conduct = 2
  density = 1
  expand = 3
  formula = G4_BUTANE
  name = G4_BUTANE
  specific = 4
FEATURE [App::DocumentObjectGroupPython] C_element020  label="C_element : 008"  # scripted group (container) (typed FeaturePython)
  n = 4
  ref = C_element
FEATURE [App::DocumentObjectGroupPython] H_element019  label="H_element : 011"  # scripted group (container) (typed FeaturePython)
  n = 10
  ref = H_element
FEATURE [App::DocumentObjectGroupPython] O_element018  label="O_element : 007"  # scripted group (container) (typed FeaturePython)
  n = 1
  ref = O_element
FEATURE [App::DocumentObjectGroupPython] G4_N_BUTYL_ALCOHOL  label="G4_N-BUTYL_ALCOHOL"  # scripted group (container) (typed FeaturePython)
  Dunit = g/cm3
  Dvalue = 0.8098
  Group = -> [C_element020,H_element019,O_element018]
  conduct = 2
  density = 1
  expand = 3
  formula = G4_N-BUTYL_ALCOHOL
  name = G4_N-BUTYL_ALCOHOL
  specific = 4
FEATURE [App::DocumentObjectGroupPython] H_element020  label="H_element : 0.025"  # scripted group (container) (typed FeaturePython)
  n = 0.02468
FEATURE [App::DocumentObjectGroupPython] C_element021  label="C_element : 0.502"  # scripted group (container) (typed FeaturePython)
  n = 0.501611
FEATURE [App::DocumentObjectGroupPython] O_element019  label="O_element : 0.005"  # scripted group (container) (typed FeaturePython)
  n = 0.004527
FEATURE [App::DocumentObjectGroupPython] F_element004  label="F_element : 0.465"  # scripted group (container) (typed FeaturePython)
  n = 0.465209
FEATURE [App::DocumentObjectGroupPython] Si_element001  label="Si_element : 0.004"  # scripted group (container) (typed FeaturePython)
  n = 0.003973
FEATURE [App::DocumentObjectGroupPython] G4_C_552  label="G4_C-552"  # scripted group (container) (typed FeaturePython)
  Dunit = g/cm3
  Dvalue = 1.76
  Group = -> [H_element020,C_element021,O_element019,F_element004,Si_element001]
  conduct = 2
  density = 1
  expand = 3
  formula = G4_C-552
  name = G4_C-552
  specific = 4
FEATURE [App::DocumentObjectGroupPython] Cd_element001  label="Cd_element : 1"  # scripted group (container) (typed FeaturePython)
  n = 1
  ref = Cd_element
FEATURE [App::DocumentObjectGroupPython] Te_element001  label="Te_element : 1"  # scripted group (container) (typed FeaturePython)
  n = 1
  ref = Te_element
FEATURE [App::DocumentObjectGroupPython] G4_CADMIUM_TELLURIDE  # scripted group (container) (typed FeaturePython)
  Dunit = g/cm3
  Dvalue = 6.2
  Group = -> [Cd_element001,Te_element001]
  conduct = 2
  density = 1
  expand = 3
  formula = G4_CADMIUM_TELLURIDE
  name = G4_CADMIUM_TELLURIDE
  specific = 4
FEATURE [App::DocumentObjectGroupPython] Cd_element002  label="Cd_element : 002"  # scripted group (container) (typed FeaturePython)
  n = 1
  ref = Cd_element
FEATURE [App::DocumentObjectGroupPython] W_element001  label="W_element : 1"  # scripted group (container) (typed FeaturePython)
  n = 1
  ref = W_element
FEATURE [App::DocumentObjectGroupPython] O_element020  label="O_element : 008"  # scripted group (container) (typed FeaturePython)
  n = 4
  ref = O_element
FEATURE [App::DocumentObjectGroupPython] G4_CADMIUM_TUNGSTATE  # scripted group (container) (typed FeaturePython)
  Dunit = g/cm3
  Dvalue = 7.9
  Group = -> [Cd_element002,W_element001,O_element020]
  conduct = 2
  density = 1
  expand = 3
  formula = G4_CADMIUM_TUNGSTATE
  name = G4_CADMIUM_TUNGSTATE
  specific = 4
FEATURE [App::DocumentObjectGroupPython] Ca_element005  label="Ca_element : 1"  # scripted group (container) (typed FeaturePython)
  n = 1
  ref = Ca_element
FEATURE [App::DocumentObjectGroupPython] C_element022  label="C_element : 009"  # scripted group (container) (typed FeaturePython)
  n = 1
  ref = C_element
FEATURE [App::DocumentObjectGroupPython] O_element021  label="O_element : 009"  # scripted group (container) (typed FeaturePython)
  n = 3
  ref = O_element
FEATURE [App::DocumentObjectGroupPython] G4_CALCIUM_CARBONATE  # scripted group (container) (typed FeaturePython)
  Dunit = g/cm3
  Dvalue = 2.8
  Group = -> [Ca_element005,C_element022,O_element021]
  conduct = 2
  density = 1
  expand = 3
  formula = G4_CALCIUM_CARBONATE
  name = G4_CALCIUM_CARBONATE
  specific = 4
FEATURE [App::DocumentObjectGroupPython] Ca_element006  label="Ca_element : 002"  # scripted group (container) (typed FeaturePython)
  n = 1
  ref = Ca_element
FEATURE [App::DocumentObjectGroupPython] F_element005  label="F_element : 003"  # scripted group (container) (typed FeaturePython)
  n = 2
  ref = F_element
FEATURE [App::DocumentObjectGroupPython] G4_CALCIUM_FLUORIDE  # scripted group (container) (typed FeaturePython)
  Dunit = g/cm3
  Dvalue = 3.18
  Group = -> [Ca_element006,F_element005]
  conduct = 2
  density = 1
  expand = 3
  formula = G4_CALCIUM_FLUORIDE
  name = G4_CALCIUM_FLUORIDE
  specific = 4
FEATURE [App::DocumentObjectGroupPython] Ca_element007  label="Ca_element : 003"  # scripted group (container) (typed FeaturePython)
  n = 1
  ref = Ca_element
FEATURE [App::DocumentObjectGroupPython] O_element022  label="O_element : 010"  # scripted group (container) (typed FeaturePython)
  n = 1
  ref = O_element
FEATURE [App::DocumentObjectGroupPython] G4_CALCIUM_OXIDE  # scripted group (container) (typed FeaturePython)
  Dunit = g/cm3
  Dvalue = 3.3
  Group = -> [Ca_element007,O_element022]
  conduct = 2
  density = 1
  expand = 3
  formula = G4_CALCIUM_OXIDE
  name = G4_CALCIUM_OXIDE
  specific = 4
FEATURE [App::DocumentObjectGroupPython] Ca_element008  label="Ca_element : 004"  # scripted group (container) (typed FeaturePython)
  n = 1
  ref = Ca_element
FEATURE [App::DocumentObjectGroupPython] S_element007  label="S_element : 002"  # scripted group (container) (typed FeaturePython)
  n = 1
  ref = S_element
FEATURE [App::DocumentObjectGroupPython] O_element023  label="O_element : 011"  # scripted group (container) (typed FeaturePython)
  n = 4
  ref = O_element
FEATURE [App::DocumentObjectGroupPython] G4_CALCIUM_SULFATE  # scripted group (container) (typed FeaturePython)
  Dunit = g/cm3
  Dvalue = 2.96
  Group = -> [Ca_element008,S_element007,O_element023]
  conduct = 2
  density = 1
  expand = 3
  formula = G4_CALCIUM_SULFATE
  name = G4_CALCIUM_SULFATE
  specific = 4
FEATURE [App::DocumentObjectGroupPython] Ca_element009  label="Ca_element : 005"  # scripted group (container) (typed FeaturePython)
  n = 1
  ref = Ca_element
FEATURE [App::DocumentObjectGroupPython] W_element002  label="W_element : 002"  # scripted group (container) (typed FeaturePython)
  n = 1
  ref = W_element
FEATURE [App::DocumentObjectGroupPython] O_element024  label="O_element : 012"  # scripted group (container) (typed FeaturePython)
  n = 4
  ref = O_element
FEATURE [App::DocumentObjectGroupPython] G4_CALCIUM_TUNGSTATE  # scripted group (container) (typed FeaturePython)
  Dunit = g/cm3
  Dvalue = 6.062
  Group = -> [Ca_element009,W_element002,O_element024]
  conduct = 2
  density = 1
  expand = 3
  formula = G4_CALCIUM_TUNGSTATE
  name = G4_CALCIUM_TUNGSTATE
  specific = 4
FEATURE [App::DocumentObjectGroupPython] C_element023  label="C_element : 010"  # scripted group (container) (typed FeaturePython)
  n = 1
  ref = C_element
FEATURE [App::DocumentObjectGroupPython] O_element025  label="O_element : 013"  # scripted group (container) (typed FeaturePython)
  n = 2
  ref = O_element
FEATURE [App::DocumentObjectGroupPython] G4_CARBON_DIOXIDE  # scripted group (container) (typed FeaturePython)
  Dunit = g/cm3
  Dvalue = 0.00184212
  Group = -> [C_element023,O_element025]
  conduct = 2
  density = 1
  expand = 3
  formula = G4_CARBON_DIOXIDE
  name = G4_CARBON_DIOXIDE
  specific = 4
FEATURE [App::DocumentObjectGroupPython] C_element024  label="C_element : 011"  # scripted group (container) (typed FeaturePython)
  n = 1
  ref = C_element
FEATURE [App::DocumentObjectGroupPython] Cl_element004  label="Cl_element : 4"  # scripted group (container) (typed FeaturePython)
  n = 4
  ref = Cl_element
FEATURE [App::DocumentObjectGroupPython] G4_CARBON_TETRACHLORIDE  # scripted group (container) (typed FeaturePython)
  Dunit = g/cm3
  Dvalue = 1.594
  Group = -> [C_element024,Cl_element004]
  conduct = 2
  density = 1
  expand = 3
  formula = G4_CARBON_TETRACHLORIDE
  name = G4_CARBON_TETRACHLORIDE
  specific = 4
FEATURE [App::DocumentObjectGroupPython] C_element025  label="C_element : 012"  # scripted group (container) (typed FeaturePython)
  n = 6
  ref = C_element
FEATURE [App::DocumentObjectGroupPython] H_element021  label="H_element : 012"  # scripted group (container) (typed FeaturePython)
  n = 10
  ref = H_element
FEATURE [App::DocumentObjectGroupPython] O_element026  label="O_element : 5"  # scripted group (container) (typed FeaturePython)
  n = 5
  ref = O_element
FEATURE [App::DocumentObjectGroupPython] G4_CELLULOSE_CELLOPHANE  # scripted group (container) (typed FeaturePython)
  Dunit = g/cm3
  Dvalue = 1.42
  Group = -> [C_element025,H_element021,O_element026]
  conduct = 2
  density = 1
  expand = 3
  formula = G4_CELLULOSE_CELLOPHANE
  name = G4_CELLULOSE_CELLOPHANE
  specific = 4
FEATURE [App::DocumentObjectGroupPython] H_element022  label="H_element : 0.067"  # scripted group (container) (typed FeaturePython)
  n = 0.067125
FEATURE [App::DocumentObjectGroupPython] C_element026  label="C_element : 0.545"  # scripted group (container) (typed FeaturePython)
  n = 0.545403
FEATURE [App::DocumentObjectGroupPython] O_element027  label="O_element : 0.387"  # scripted group (container) (typed FeaturePython)
  n = 0.387472
FEATURE [App::DocumentObjectGroupPython] G4_CELLULOSE_BUTYRATE  # scripted group (container) (typed FeaturePython)
  Dunit = g/cm3
  Dvalue = 1.2
  Group = -> [H_element022,C_element026,O_element027]
  conduct = 2
  density = 1
  expand = 3
  formula = G4_CELLULOSE_BUTYRATE
  name = G4_CELLULOSE_BUTYRATE
  specific = 4
FEATURE [App::DocumentObjectGroupPython] H_element023  label="H_element : 0.029"  # scripted group (container) (typed FeaturePython)
  n = 0.029216
FEATURE [App::DocumentObjectGroupPython] C_element027  label="C_element : 0.271"  # scripted group (container) (typed FeaturePython)
  n = 0.271296
FEATURE [App::DocumentObjectGroupPython] N_element013  label="N_element : 0.121"  # scripted group (container) (typed FeaturePython)
  n = 0.121276
FEATURE [App::DocumentObjectGroupPython] O_element028  label="O_element : 0.578"  # scripted group (container) (typed FeaturePython)
  n = 0.578212
FEATURE [App::DocumentObjectGroupPython] G4_CELLULOSE_NITRATE  # scripted group (container) (typed FeaturePython)
  Dunit = g/cm3
  Dvalue = 1.49
  Group = -> [H_element023,C_element027,N_element013,O_element028]
  conduct = 2
  density = 1
  expand = 3
  formula = G4_CELLULOSE_NITRATE
  name = G4_CELLULOSE_NITRATE
  specific = 4
FEATURE [App::DocumentObjectGroupPython] H_element024  label="H_element : 0.108"  # scripted group (container) (typed FeaturePython)
  n = 0.107596
FEATURE [App::DocumentObjectGroupPython] N_element014  label="N_element : 0.001"  # scripted group (container) (typed FeaturePython)
  n = 0.0008
FEATURE [App::DocumentObjectGroupPython] O_element029  label="O_element : 0.875"  # scripted group (container) (typed FeaturePython)
  n = 0.874976
FEATURE [App::DocumentObjectGroupPython] S_element008  label="S_element : 0.015"  # scripted group (container) (typed FeaturePython)
  n = 0.014627
FEATURE [App::DocumentObjectGroupPython] Ce_element001  label="Ce_element : 0.002"  # scripted group (container) (typed FeaturePython)
  n = 0.002001
FEATURE [App::DocumentObjectGroupPython] G4_CERIC_SULFATE  # scripted group (container) (typed FeaturePython)
  Dunit = g/cm3
  Dvalue = 1.03
  Group = -> [H_element024,N_element014,O_element029,S_element008,Ce_element001]
  conduct = 2
  density = 1
  expand = 3
  formula = G4_CERIC_SULFATE
  name = G4_CERIC_SULFATE
  specific = 4
FEATURE [App::DocumentObjectGroupPython] Cs_element001  label="Cs_element : 1"  # scripted group (container) (typed FeaturePython)
  n = 1
  ref = Cs_element
FEATURE [App::DocumentObjectGroupPython] F_element006  label="F_element : 1"  # scripted group (container) (typed FeaturePython)
  n = 1
  ref = F_element
FEATURE [App::DocumentObjectGroupPython] G4_CESIUM_FLUORIDE  # scripted group (container) (typed FeaturePython)
  Dunit = g/cm3
  Dvalue = 4.115
  Group = -> [Cs_element001,F_element006]
  conduct = 2
  density = 1
  expand = 3
  formula = G4_CESIUM_FLUORIDE
  name = G4_CESIUM_FLUORIDE
  specific = 4
FEATURE [App::DocumentObjectGroupPython] Cs_element002  label="Cs_element : 002"  # scripted group (container) (typed FeaturePython)
  n = 1
  ref = Cs_element
FEATURE [App::DocumentObjectGroupPython] I_element001  label="I_element : 1"  # scripted group (container) (typed FeaturePython)
  n = 1
  ref = I_element
FEATURE [App::DocumentObjectGroupPython] G4_CESIUM_IODIDE  # scripted group (container) (typed FeaturePython)
  Dunit = g/cm3
  Dvalue = 4.51
  Group = -> [Cs_element002,I_element001]
  conduct = 2
  density = 1
  expand = 3
  formula = G4_CESIUM_IODIDE
  name = G4_CESIUM_IODIDE
  specific = 4
FEATURE [App::DocumentObjectGroupPython] C_element028  label="C_element : 013"  # scripted group (container) (typed FeaturePython)
  n = 6
  ref = C_element
FEATURE [App::DocumentObjectGroupPython] H_element025  label="H_element : 013"  # scripted group (container) (typed FeaturePython)
  n = 5
  ref = H_element
FEATURE [App::DocumentObjectGroupPython] Cl_element005  label="Cl_element : 1"  # scripted group (container) (typed FeaturePython)
  n = 1
  ref = Cl_element
FEATURE [App::DocumentObjectGroupPython] G4_CHLOROBENZENE  # scripted group (container) (typed FeaturePython)
  Dunit = g/cm3
  Dvalue = 1.1058
  Group = -> [C_element028,H_element025,Cl_element005]
  conduct = 2
  density = 1
  expand = 3
  formula = G4_CHLOROBENZENE
  name = G4_CHLOROBENZENE
  specific = 4
FEATURE [App::DocumentObjectGroupPython] C_element029  label="C_element : 014"  # scripted group (container) (typed FeaturePython)
  n = 1
  ref = C_element
FEATURE [App::DocumentObjectGroupPython] H_element026  label="H_element : 1"  # scripted group (container) (typed FeaturePython)
  n = 1
  ref = H_element
FEATURE [App::DocumentObjectGroupPython] Cl_element006  label="Cl_element : 3"  # scripted group (container) (typed FeaturePython)
  n = 3
  ref = Cl_element
FEATURE [App::DocumentObjectGroupPython] G4_CHLOROFORM  # scripted group (container) (typed FeaturePython)
  Dunit = g/cm3
  Dvalue = 1.4832
  Group = -> [C_element029,H_element026,Cl_element006]
  conduct = 2
  density = 1
  expand = 3
  formula = G4_CHLOROFORM
  name = G4_CHLOROFORM
  specific = 4
FEATURE [App::DocumentObjectGroupPython] H_element027  label="H_element : 0.010"  # scripted group (container) (typed FeaturePython)
  n = 0.01
FEATURE [App::DocumentObjectGroupPython] C_element030  label="C_element : 0.001"  # scripted group (container) (typed FeaturePython)
  n = 0.001
FEATURE [App::DocumentObjectGroupPython] O_element030  label="O_element : 0.529"  # scripted group (container) (typed FeaturePython)
  n = 0.529107
FEATURE [App::DocumentObjectGroupPython] Na_element005  label="Na_element : 0.016"  # scripted group (container) (typed FeaturePython)
  n = 0.016
FEATURE [App::DocumentObjectGroupPython] Mg_element003  label="Mg_element : 0.004"  # scripted group (container) (typed FeaturePython)
  n = 0.002
FEATURE [App::DocumentObjectGroupPython] Al_element002  label="Al_element : 0.034"  # scripted group (container) (typed FeaturePython)
  n = 0.033872
FEATURE [App::DocumentObjectGroupPython] Si_element002  label="Si_element : 0.337"  # scripted group (container) (typed FeaturePython)
  n = 0.337021
FEATURE [App::DocumentObjectGroupPython] K_element003  label="K_element : 0.013"  # scripted group (container) (typed FeaturePython)
  n = 0.013
FEATURE [App::DocumentObjectGroupPython] Ca_element010  label="Ca_element : 0.044"  # scripted group (container) (typed FeaturePython)
  n = 0.044
FEATURE [App::DocumentObjectGroupPython] Fe_element002  label="Fe_element : 0.014"  # scripted group (container) (typed FeaturePython)
  n = 0.014
FEATURE [App::DocumentObjectGroupPython] G4_CONCRETE  # scripted group (container) (typed FeaturePython)
  Dunit = g/cm3
  Dvalue = 2.3
  Group = -> [H_element027,C_element030,O_element030,Na_element005,Mg_element003,Al_element002,Si_element002,K_element003,Ca_element010,Fe_element002]
  conduct = 2
  density = 1
  expand = 3
  formula = G4_CONCRETE
  name = G4_CONCRETE
  specific = 4
FEATURE [App::DocumentObjectGroupPython] C_element031  label="C_element : 015"  # scripted group (container) (typed FeaturePython)
  n = 6
  ref = C_element
FEATURE [App::DocumentObjectGroupPython] H_element028  label="H_element : 12"  # scripted group (container) (typed FeaturePython)
  n = 12
  ref = H_element
FEATURE [App::DocumentObjectGroupPython] G4_CYCLOHEXANE  # scripted group (container) (typed FeaturePython)
  Dunit = g/cm3
  Dvalue = 0.779
  Group = -> [C_element031,H_element028]
  conduct = 2
  density = 1
  expand = 3
  formula = G4_CYCLOHEXANE
  name = G4_CYCLOHEXANE
  specific = 4
FEATURE [App::DocumentObjectGroupPython] C_element032  label="C_element : 016"  # scripted group (container) (typed FeaturePython)
  n = 6
  ref = C_element
FEATURE [App::DocumentObjectGroupPython] H_element029  label="H_element : 4"  # scripted group (container) (typed FeaturePython)
  n = 4
  ref = H_element
FEATURE [App::DocumentObjectGroupPython] Cl_element007  label="Cl_element : 2"  # scripted group (container) (typed FeaturePython)
  n = 2
  ref = Cl_element
FEATURE [App::DocumentObjectGroupPython] G4_1_2_DICHLOROBENZENE  label="G4_1.2-DICHLOROBENZENE"  # scripted group (container) (typed FeaturePython)
  Dunit = g/cm3
  Dvalue = 1.3048
  Group = -> [C_element032,H_element029,Cl_element007]
  conduct = 2
  density = 1
  expand = 3
  formula = G4_1.2-DICHLOROBENZENE
  name = G4_1.2-DICHLOROBENZENE
  specific = 4
FEATURE [App::DocumentObjectGroupPython] C_element033  label="C_element : 017"  # scripted group (container) (typed FeaturePython)
  n = 4
  ref = C_element
FEATURE [App::DocumentObjectGroupPython] H_element030  label="H_element : 8"  # scripted group (container) (typed FeaturePython)
  n = 8
  ref = H_element
FEATURE [App::DocumentObjectGroupPython] O_element031  label="O_element : 014"  # scripted group (container) (typed FeaturePython)
  n = 1
  ref = O_element
FEATURE [App::DocumentObjectGroupPython] Cl_element008  label="Cl_element : 005"  # scripted group (container) (typed FeaturePython)
  n = 2
  ref = Cl_element
FEATURE [App::DocumentObjectGroupPython] G4_DICHLORODIETHYL_ETHER  # scripted group (container) (typed FeaturePython)
  Dunit = g/cm3
  Dvalue = 1.2199
  Group = -> [C_element033,H_element030,O_element031,Cl_element008]
  conduct = 2
  density = 1
  expand = 3
  formula = G4_DICHLORODIETHYL_ETHER
  name = G4_DICHLORODIETHYL_ETHER
  specific = 4
FEATURE [App::DocumentObjectGroupPython] C_element034  label="C_element : 018"  # scripted group (container) (typed FeaturePython)
  n = 2
  ref = C_element
FEATURE [App::DocumentObjectGroupPython] H_element031  label="H_element : 014"  # scripted group (container) (typed FeaturePython)
  n = 4
  ref = H_element
FEATURE [App::DocumentObjectGroupPython] Cl_element009  label="Cl_element : 006"  # scripted group (container) (typed FeaturePython)
  n = 2
  ref = Cl_element
FEATURE [App::DocumentObjectGroupPython] G4_1_2_DICHLOROETHANE  label="G4_1.2-DICHLOROETHANE"  # scripted group (container) (typed FeaturePython)
  Dunit = g/cm3
  Dvalue = 1.2351
  Group = -> [C_element034,H_element031,Cl_element009]
  conduct = 2
  density = 1
  expand = 3
  formula = G4_1.2-DICHLOROETHANE
  name = G4_1.2-DICHLOROETHANE
  specific = 4
FEATURE [App::DocumentObjectGroupPython] C_element035  label="C_element : 019"  # scripted group (container) (typed FeaturePython)
  n = 4
  ref = C_element
FEATURE [App::DocumentObjectGroupPython] H_element032  label="H_element : 015"  # scripted group (container) (typed FeaturePython)
  n = 10
  ref = H_element
FEATURE [App::DocumentObjectGroupPython] O_element032  label="O_element : 015"  # scripted group (container) (typed FeaturePython)
  n = 1
  ref = O_element
FEATURE [App::DocumentObjectGroupPython] G4_DIETHYL_ETHER  # scripted group (container) (typed FeaturePython)
  Dunit = g/cm3
  Dvalue = 0.71378
  Group = -> [C_element035,H_element032,O_element032]
  conduct = 2
  density = 1
  expand = 3
  formula = G4_DIETHYL_ETHER
  name = G4_DIETHYL_ETHER
  specific = 4
FEATURE [App::DocumentObjectGroupPython] C_element036  label="C_element : 020"  # scripted group (container) (typed FeaturePython)
  n = 3
  ref = C_element
FEATURE [App::DocumentObjectGroupPython] H_element033  label="H_element : 016"  # scripted group (container) (typed FeaturePython)
  n = 7
  ref = H_element
FEATURE [App::DocumentObjectGroupPython] N_element015  label="N_element : 008"  # scripted group (container) (typed FeaturePython)
  n = 1
  ref = N_element
FEATURE [App::DocumentObjectGroupPython] O_element033  label="O_element : 016"  # scripted group (container) (typed FeaturePython)
  n = 1
  ref = O_element
FEATURE [App::DocumentObjectGroupPython] G4_N_N_DIMETHYL_FORMAMIDE  label="G4_N.N-DIMETHYL_FORMAMIDE"  # scripted group (container) (typed FeaturePython)
  Dunit = g/cm3
  Dvalue = 0.9487
  Group = -> [C_element036,H_element033,N_element015,O_element033]
  conduct = 2
  density = 1
  expand = 3
  formula = G4_N.N-DIMETHYL_FORMAMIDE
  name = G4_N.N-DIMETHYL_FORMAMIDE
  specific = 4
FEATURE [App::DocumentObjectGroupPython] C_element037  label="C_element : 021"  # scripted group (container) (typed FeaturePython)
  n = 2
  ref = C_element
FEATURE [App::DocumentObjectGroupPython] H_element034  label="H_element : 017"  # scripted group (container) (typed FeaturePython)
  n = 6
  ref = H_element
FEATURE [App::DocumentObjectGroupPython] O_element034  label="O_element : 017"  # scripted group (container) (typed FeaturePython)
  n = 1
  ref = O_element
FEATURE [App::DocumentObjectGroupPython] S_element009  label="S_element : 003"  # scripted group (container) (typed FeaturePython)
  n = 1
  ref = S_element
FEATURE [App::DocumentObjectGroupPython] G4_DIMETHYL_SULFOXIDE  # scripted group (container) (typed FeaturePython)
  Dunit = g/cm3
  Dvalue = 1.1014
  Group = -> [C_element037,H_element034,O_element034,S_element009]
  conduct = 2
  density = 1
  expand = 3
  formula = G4_DIMETHYL_SULFOXIDE
  name = G4_DIMETHYL_SULFOXIDE
  specific = 4
FEATURE [App::DocumentObjectGroupPython] C_element038  label="C_element : 022"  # scripted group (container) (typed FeaturePython)
  n = 2
  ref = C_element
FEATURE [App::DocumentObjectGroupPython] H_element035  label="H_element : 018"  # scripted group (container) (typed FeaturePython)
  n = 6
  ref = H_element
FEATURE [App::DocumentObjectGroupPython] G4_ETHANE  # scripted group (container) (typed FeaturePython)
  Dunit = g/cm3
  Dvalue = 0.00125324
  Group = -> [C_element038,H_element035]
  conduct = 2
  density = 1
  expand = 3
  formula = G4_ETHANE
  name = G4_ETHANE
  specific = 4
FEATURE [App::DocumentObjectGroupPython] C_element039  label="C_element : 023"  # scripted group (container) (typed FeaturePython)
  n = 2
  ref = C_element
FEATURE [App::DocumentObjectGroupPython] H_element036  label="H_element : 019"  # scripted group (container) (typed FeaturePython)
  n = 6
  ref = H_element
FEATURE [App::DocumentObjectGroupPython] O_element035  label="O_element : 018"  # scripted group (container) (typed FeaturePython)
  n = 1
  ref = O_element
FEATURE [App::DocumentObjectGroupPython] G4_ETHYL_ALCOHOL  # scripted group (container) (typed FeaturePython)
  Dunit = g/cm3
  Dvalue = 0.7893
  Group = -> [C_element039,H_element036,O_element035]
  conduct = 2
  density = 1
  expand = 3
  formula = G4_ETHYL_ALCOHOL
  name = G4_ETHYL_ALCOHOL
  specific = 4
FEATURE [App::DocumentObjectGroupPython] H_element037  label="H_element : 0.090"  # scripted group (container) (typed FeaturePython)
  n = 0.090027
FEATURE [App::DocumentObjectGroupPython] C_element040  label="C_element : 0.585"  # scripted group (container) (typed FeaturePython)
  n = 0.585182
FEATURE [App::DocumentObjectGroupPython] O_element036  label="O_element : 0.325"  # scripted group (container) (typed FeaturePython)
  n = 0.324791
FEATURE [App::DocumentObjectGroupPython] G4_ETHYL_CELLULOSE  # scripted group (container) (typed FeaturePython)
  Dunit = g/cm3
  Dvalue = 1.13
  Group = -> [H_element037,C_element040,O_element036]
  conduct = 2
  density = 1
  expand = 3
  formula = G4_ETHYL_CELLULOSE
  name = G4_ETHYL_CELLULOSE
  specific = 4
FEATURE [App::DocumentObjectGroupPython] C_element041  label="C_element : 024"  # scripted group (container) (typed FeaturePython)
  n = 2
  ref = C_element
FEATURE [App::DocumentObjectGroupPython] H_element038  label="H_element : 020"  # scripted group (container) (typed FeaturePython)
  n = 4
  ref = H_element
FEATURE [App::DocumentObjectGroupPython] G4_ETHYLENE  # scripted group (container) (typed FeaturePython)
  Dunit = g/cm3
  Dvalue = 0.00117497
  Group = -> [C_element041,H_element038]
  conduct = 2
  density = 1
  expand = 3
  formula = G4_ETHYLENE
  name = G4_ETHYLENE
  specific = 4
FEATURE [App::DocumentObjectGroupPython] H_element039  label="H_element : 0.096"  # scripted group (container) (typed FeaturePython)
  n = 0.096
FEATURE [App::DocumentObjectGroupPython] C_element042  label="C_element : 0.195"  # scripted group (container) (typed FeaturePython)
  n = 0.195
FEATURE [App::DocumentObjectGroupPython] N_element016  label="N_element : 0.057"  # scripted group (container) (typed FeaturePython)
  n = 0.057
FEATURE [App::DocumentObjectGroupPython] O_element037  label="O_element : 0.646"  # scripted group (container) (typed FeaturePython)
  n = 0.646
FEATURE [App::DocumentObjectGroupPython] Na_element006  label="Na_element : 0.017"  # scripted group (container) (typed FeaturePython)
  n = 0.001
FEATURE [App::DocumentObjectGroupPython] P_element005  label="P_element : 0.104"  # scripted group (container) (typed FeaturePython)
  n = 0.001
FEATURE [App::DocumentObjectGroupPython] S_element010  label="S_element : 0.016"  # scripted group (container) (typed FeaturePython)
  n = 0.003
FEATURE [App::DocumentObjectGroupPython] Cl_element010  label="Cl_element : 0.005"  # scripted group (container) (typed FeaturePython)
  n = 0.001
FEATURE [App::DocumentObjectGroupPython] G4_EYE_LENS_ICRP  # scripted group (container) (typed FeaturePython)
  Dunit = g/cm3
  Dvalue = 1.07
  Group = -> [H_element039,C_element042,N_element016,O_element037,Na_element006,P_element005,S_element010,Cl_element010]
  conduct = 2
  density = 1
  expand = 3
  formula = G4_EYE_LENS_ICRP
  name = G4_EYE_LENS_ICRP
  specific = 4
FEATURE [App::DocumentObjectGroupPython] Fe_element003  label="Fe_element : 2"  # scripted group (container) (typed FeaturePython)
  n = 2
  ref = Fe_element
FEATURE [App::DocumentObjectGroupPython] O_element038  label="O_element : 019"  # scripted group (container) (typed FeaturePython)
  n = 3
  ref = O_element
FEATURE [App::DocumentObjectGroupPython] G4_FERRIC_OXIDE  # scripted group (container) (typed FeaturePython)
  Dunit = g/cm3
  Dvalue = 5.2
  Group = -> [Fe_element003,O_element038]
  conduct = 2
  density = 1
  expand = 3
  formula = G4_FERRIC_OXIDE
  name = G4_FERRIC_OXIDE
  specific = 4
FEATURE [App::DocumentObjectGroupPython] Fe_element004  label="Fe_element : 1"  # scripted group (container) (typed FeaturePython)
  n = 1
  ref = Fe_element
FEATURE [App::DocumentObjectGroupPython] B_element003  label="B_element : 1"  # scripted group (container) (typed FeaturePython)
  n = 1
  ref = B_element
FEATURE [App::DocumentObjectGroupPython] G4_FERROBORIDE  # scripted group (container) (typed FeaturePython)
  Dunit = g/cm3
  Dvalue = 7.15
  Group = -> [Fe_element004,B_element003]
  conduct = 2
  density = 1
  expand = 3
  formula = G4_FERROBORIDE
  name = G4_FERROBORIDE
  specific = 4
FEATURE [App::DocumentObjectGroupPython] Fe_element005  label="Fe_element : 003"  # scripted group (container) (typed FeaturePython)
  n = 1
  ref = Fe_element
FEATURE [App::DocumentObjectGroupPython] O_element039  label="O_element : 020"  # scripted group (container) (typed FeaturePython)
  n = 1
  ref = O_element
FEATURE [App::DocumentObjectGroupPython] G4_FERROUS_OXIDE  # scripted group (container) (typed FeaturePython)
  Dunit = g/cm3
  Dvalue = 5.7
  Group = -> [Fe_element005,O_element039]
  conduct = 2
  density = 1
  expand = 3
  formula = G4_FERROUS_OXIDE
  name = G4_FERROUS_OXIDE
  specific = 4
FEATURE [App::DocumentObjectGroupPython] H_element040  label="H_element : 0.115"  # scripted group (container) (typed FeaturePython)
  n = 0.108259
FEATURE [App::DocumentObjectGroupPython] N_element017  label="N_element : 0.000"  # scripted group (container) (typed FeaturePython)
  n = 2.7e-05
FEATURE [App::DocumentObjectGroupPython] O_element040  label="O_element : 0.879"  # scripted group (container) (typed FeaturePython)
  n = 0.878636
FEATURE [App::DocumentObjectGroupPython] Na_element007  label="Na_element : 0.000"  # scripted group (container) (typed FeaturePython)
  n = 2.2e-05
FEATURE [App::DocumentObjectGroupPython] S_element011  label="S_element : 0.013"  # scripted group (container) (typed FeaturePython)
  n = 0.012968
FEATURE [App::DocumentObjectGroupPython] Cl_element011  label="Cl_element : 0.000"  # scripted group (container) (typed FeaturePython)
  n = 3.4e-05
FEATURE [App::DocumentObjectGroupPython] Fe_element006  label="Fe_element : 0.000"  # scripted group (container) (typed FeaturePython)
  n = 5.4e-05
FEATURE [App::DocumentObjectGroupPython] G4_FERROUS_SULFATE  # scripted group (container) (typed FeaturePython)
  Dunit = g/cm3
  Dvalue = 1.024
  Group = -> [H_element040,N_element017,O_element040,Na_element007,S_element011,Cl_element011,Fe_element006]
  conduct = 2
  density = 1
  expand = 3
  formula = G4_FERROUS_SULFATE
  name = G4_FERROUS_SULFATE
  specific = 4
FEATURE [App::DocumentObjectGroupPython] C_element043  label="C_element : 0.099"  # scripted group (container) (typed FeaturePython)
  n = 0.099335
FEATURE [App::DocumentObjectGroupPython] F_element007  label="F_element : 0.314"  # scripted group (container) (typed FeaturePython)
  n = 0.314247
FEATURE [App::DocumentObjectGroupPython] Cl_element012  label="Cl_element : 0.586"  # scripted group (container) (typed FeaturePython)
  n = 0.586418
FEATURE [App::DocumentObjectGroupPython] G4_FREON_12  label="G4_FREON-12"  # scripted group (container) (typed FeaturePython)
  Dunit = g/cm3
  Dvalue = 1.12
  Group = -> [C_element043,F_element007,Cl_element012]
  conduct = 2
  density = 1
  expand = 3
  formula = G4_FREON-12
  name = G4_FREON-12
  specific = 4
FEATURE [App::DocumentObjectGroupPython] C_element044  label="C_element : 0.057"  # scripted group (container) (typed FeaturePython)
  n = 0.057245
FEATURE [App::DocumentObjectGroupPython] F_element008  label="F_element : 0.181"  # scripted group (container) (typed FeaturePython)
  n = 0.181096
FEATURE [App::DocumentObjectGroupPython] Br_element001  label="Br_element : 0.762"  # scripted group (container) (typed FeaturePython)
  n = 0.761659
FEATURE [App::DocumentObjectGroupPython] G4_FREON_12B2  label="G4_FREON-12B2"  # scripted group (container) (typed FeaturePython)
  Dunit = g/cm3
  Dvalue = 1.8
  Group = -> [C_element044,F_element008,Br_element001]
  conduct = 2
  density = 1
  expand = 3
  formula = G4_FREON-12B2
  name = G4_FREON-12B2
  specific = 4
FEATURE [App::DocumentObjectGroupPython] C_element045  label="C_element : 0.115"  # scripted group (container) (typed FeaturePython)
  n = 0.114983
FEATURE [App::DocumentObjectGroupPython] F_element009  label="F_element : 0.546"  # scripted group (container) (typed FeaturePython)
  n = 0.545621
FEATURE [App::DocumentObjectGroupPython] Cl_element013  label="Cl_element : 0.339"  # scripted group (container) (typed FeaturePython)
  n = 0.339396
FEATURE [App::DocumentObjectGroupPython] G4_FREON_13  label="G4_FREON-13"  # scripted group (container) (typed FeaturePython)
  Dunit = g/cm3
  Dvalue = 0.95
  Group = -> [C_element045,F_element009,Cl_element013]
  conduct = 2
  density = 1
  expand = 3
  formula = G4_FREON-13
  name = G4_FREON-13
  specific = 4
FEATURE [App::DocumentObjectGroupPython] C_element046  label="C_element : 025"  # scripted group (container) (typed FeaturePython)
  n = 1
  ref = C_element
FEATURE [App::DocumentObjectGroupPython] F_element010  label="F_element : 3"  # scripted group (container) (typed FeaturePython)
  n = 3
  ref = F_element
FEATURE [App::DocumentObjectGroupPython] Br_element002  label="Br_element : 1"  # scripted group (container) (typed FeaturePython)
  n = 1
  ref = Br_element
FEATURE [App::DocumentObjectGroupPython] G4_FREON_13B1  label="G4_FREON-13B1"  # scripted group (container) (typed FeaturePython)
  Dunit = g/cm3
  Dvalue = 1.5
  Group = -> [C_element046,F_element010,Br_element002]
  conduct = 2
  density = 1
  expand = 3
  formula = G4_FREON-13B1
  name = G4_FREON-13B1
  specific = 4
FEATURE [App::DocumentObjectGroupPython] C_element047  label="C_element : 0.061"  # scripted group (container) (typed FeaturePython)
  n = 0.061309
FEATURE [App::DocumentObjectGroupPython] F_element011  label="F_element : 0.291"  # scripted group (container) (typed FeaturePython)
  n = 0.290924
FEATURE [App::DocumentObjectGroupPython] I_element002  label="I_element : 0.648"  # scripted group (container) (typed FeaturePython)
  n = 0.647767
FEATURE [App::DocumentObjectGroupPython] G4_FREON_13I1  label="G4_FREON-13I1"  # scripted group (container) (typed FeaturePython)
  Dunit = g/cm3
  Dvalue = 1.8
  Group = -> [C_element047,F_element011,I_element002]
  conduct = 2
  density = 1
  expand = 3
  formula = G4_FREON-13I1
  name = G4_FREON-13I1
  specific = 4
FEATURE [App::DocumentObjectGroupPython] Gd_element001  label="Gd_element : 2"  # scripted group (container) (typed FeaturePython)
  n = 2
  ref = Gd_element
FEATURE [App::DocumentObjectGroupPython] O_element041  label="O_element : 021"  # scripted group (container) (typed FeaturePython)
  n = 2
  ref = O_element
FEATURE [App::DocumentObjectGroupPython] S_element012  label="S_element : 004"  # scripted group (container) (typed FeaturePython)
  n = 1
  ref = S_element
FEATURE [App::DocumentObjectGroupPython] G4_GADOLINIUM_OXYSULFIDE  # scripted group (container) (typed FeaturePython)
  Dunit = g/cm3
  Dvalue = 7.44
  Group = -> [Gd_element001,O_element041,S_element012]
  conduct = 2
  density = 1
  expand = 3
  formula = G4_GADOLINIUM_OXYSULFIDE
  name = G4_GADOLINIUM_OXYSULFIDE
  specific = 4
FEATURE [App::DocumentObjectGroupPython] Ga_element001  label="Ga_element : 1"  # scripted group (container) (typed FeaturePython)
  n = 1
  ref = Ga_element
FEATURE [App::DocumentObjectGroupPython] As_element001  label="As_element : 1"  # scripted group (container) (typed FeaturePython)
  n = 1
  ref = As_element
FEATURE [App::DocumentObjectGroupPython] G4_GALLIUM_ARSENIDE  # scripted group (container) (typed FeaturePython)
  Dunit = g/cm3
  Dvalue = 5.31
  Group = -> [Ga_element001,As_element001]
  conduct = 2
  density = 1
  expand = 3
  formula = G4_GALLIUM_ARSENIDE
  name = G4_GALLIUM_ARSENIDE
  specific = 4
FEATURE [App::DocumentObjectGroupPython] H_element041  label="H_element : 0.081"  # scripted group (container) (typed FeaturePython)
  n = 0.08118
FEATURE [App::DocumentObjectGroupPython] C_element048  label="C_element : 0.416"  # scripted group (container) (typed FeaturePython)
  n = 0.41606
FEATURE [App::DocumentObjectGroupPython] N_element018  label="N_element : 0.111"  # scripted group (container) (typed FeaturePython)
  n = 0.11124
FEATURE [App::DocumentObjectGroupPython] O_element042  label="O_element : 0.381"  # scripted group (container) (typed FeaturePython)
  n = 0.38064
FEATURE [App::DocumentObjectGroupPython] S_element013  label="S_element : 0.011"  # scripted group (container) (typed FeaturePython)
  n = 0.01088
FEATURE [App::DocumentObjectGroupPython] G4_GEL_PHOTO_EMULSION  # scripted group (container) (typed FeaturePython)
  Dunit = g/cm3
  Dvalue = 1.2914
  Group = -> [H_element041,C_element048,N_element018,O_element042,S_element013]
  conduct = 2
  density = 1
  expand = 3
  formula = G4_GEL_PHOTO_EMULSION
  name = G4_GEL_PHOTO_EMULSION
  specific = 4
FEATURE [App::DocumentObjectGroupPython] B_element004  label="B_element : 0.040"  # scripted group (container) (typed FeaturePython)
  n = 0.0400639
FEATURE [App::DocumentObjectGroupPython] O_element043  label="O_element : 0.540"  # scripted group (container) (typed FeaturePython)
  n = 0.539561
FEATURE [App::DocumentObjectGroupPython] Na_element008  label="Na_element : 0.028"  # scripted group (container) (typed FeaturePython)
  n = 0.0281909
FEATURE [App::DocumentObjectGroupPython] Al_element003  label="Al_element : 0.012"  # scripted group (container) (typed FeaturePython)
  n = 0.011644
FEATURE [App::DocumentObjectGroupPython] Si_element003  label="Si_element : 0.377"  # scripted group (container) (typed FeaturePython)
  n = 0.377219
FEATURE [App::DocumentObjectGroupPython] K_element004  label="K_element : 0.014"  # scripted group (container) (typed FeaturePython)
  n = 0.00332099
FEATURE [App::DocumentObjectGroupPython] G4_Pyrex_Glass  # scripted group (container) (typed FeaturePython)
  Dunit = g/cm3
  Dvalue = 2.23
  Group = -> [B_element004,O_element043,Na_element008,Al_element003,Si_element003,K_element004]
  conduct = 2
  density = 1
  expand = 3
  formula = G4_Pyrex_Glass
  name = G4_Pyrex_Glass
  specific = 4
FEATURE [App::DocumentObjectGroupPython] O_element044  label="O_element : 0.156"  # scripted group (container) (typed FeaturePython)
  n = 0.156453
FEATURE [App::DocumentObjectGroupPython] Si_element004  label="Si_element : 0.081"  # scripted group (container) (typed FeaturePython)
  n = 0.080866
FEATURE [App::DocumentObjectGroupPython] Ti_element001  label="Ti_element : 0.008"  # scripted group (container) (typed FeaturePython)
  n = 0.008092
FEATURE [App::DocumentObjectGroupPython] As_element002  label="As_element : 0.003"  # scripted group (container) (typed FeaturePython)
  n = 0.002651
FEATURE [App::DocumentObjectGroupPython] Pb_element001  label="Pb_element : 0.752"  # scripted group (container) (typed FeaturePython)
  n = 0.751938
FEATURE [App::DocumentObjectGroupPython] G4_GLASS_LEAD  # scripted group (container) (typed FeaturePython)
  Dunit = g/cm3
  Dvalue = 6.22
  Group = -> [O_element044,Si_element004,Ti_element001,As_element002,Pb_element001]
  conduct = 2
  density = 1
  expand = 3
  formula = G4_GLASS_LEAD
  name = G4_GLASS_LEAD
  specific = 4
FEATURE [App::DocumentObjectGroupPython] O_element045  label="O_element : 0.460"  # scripted group (container) (typed FeaturePython)
  n = 0.4598
FEATURE [App::DocumentObjectGroupPython] Na_element009  label="Na_element : 0.096"  # scripted group (container) (typed FeaturePython)
  n = 0.0964411
FEATURE [App::DocumentObjectGroupPython] Si_element005  label="Si_element : 0.378"  # scripted group (container) (typed FeaturePython)
  n = 0.336553
FEATURE [App::DocumentObjectGroupPython] Ca_element011  label="Ca_element : 0.107"  # scripted group (container) (typed FeaturePython)
  n = 0.107205
FEATURE [App::DocumentObjectGroupPython] G4_GLASS_PLATE  # scripted group (container) (typed FeaturePython)
  Dunit = g/cm3
  Dvalue = 2.4
  Group = -> [O_element045,Na_element009,Si_element005,Ca_element011]
  conduct = 2
  density = 1
  expand = 3
  formula = G4_GLASS_PLATE
  name = G4_GLASS_PLATE
  specific = 4
FEATURE [App::DocumentObjectGroupPython] C_element049  label="C_element : 026"  # scripted group (container) (typed FeaturePython)
  n = 5
  ref = C_element
FEATURE [App::DocumentObjectGroupPython] H_element042  label="H_element : 021"  # scripted group (container) (typed FeaturePython)
  n = 10
  ref = H_element
FEATURE [App::DocumentObjectGroupPython] N_element019  label="N_element : 2"  # scripted group (container) (typed FeaturePython)
  n = 2
  ref = N_element
FEATURE [App::DocumentObjectGroupPython] O_element046  label="O_element : 022"  # scripted group (container) (typed FeaturePython)
  n = 3
  ref = O_element
FEATURE [App::DocumentObjectGroupPython] G4_GLUTAMINE  # scripted group (container) (typed FeaturePython)
  Dunit = g/cm3
  Dvalue = 1.46
  Group = -> [C_element049,H_element042,N_element019,O_element046]
  conduct = 2
  density = 1
  expand = 3
  formula = G4_GLUTAMINE
  name = G4_GLUTAMINE
  specific = 4
FEATURE [App::DocumentObjectGroupPython] C_element050  label="C_element : 027"  # scripted group (container) (typed FeaturePython)
  n = 3
  ref = C_element
FEATURE [App::DocumentObjectGroupPython] H_element043  label="H_element : 022"  # scripted group (container) (typed FeaturePython)
  n = 8
  ref = H_element
FEATURE [App::DocumentObjectGroupPython] O_element047  label="O_element : 023"  # scripted group (container) (typed FeaturePython)
  n = 3
  ref = O_element
FEATURE [App::DocumentObjectGroupPython] G4_GLYCEROL  # scripted group (container) (typed FeaturePython)
  Dunit = g/cm3
  Dvalue = 1.2613
  Group = -> [C_element050,H_element043,O_element047]
  conduct = 2
  density = 1
  expand = 3
  formula = G4_GLYCEROL
  name = G4_GLYCEROL
  specific = 4
FEATURE [App::DocumentObjectGroupPython] C_element051  label="C_element : 028"  # scripted group (container) (typed FeaturePython)
  n = 5
  ref = C_element
FEATURE [App::DocumentObjectGroupPython] H_element044  label="H_element : 023"  # scripted group (container) (typed FeaturePython)
  n = 5
  ref = H_element
FEATURE [App::DocumentObjectGroupPython] N_element020  label="N_element : 009"  # scripted group (container) (typed FeaturePython)
  n = 5
  ref = N_element
FEATURE [App::DocumentObjectGroupPython] O_element048  label="O_element : 024"  # scripted group (container) (typed FeaturePython)
  n = 1
  ref = O_element
FEATURE [App::DocumentObjectGroupPython] G4_GUANINE  # scripted group (container) (typed FeaturePython)
  Dunit = g/cm3
  Dvalue = 2.2
  Group = -> [C_element051,H_element044,N_element020,O_element048]
  conduct = 2
  density = 1
  expand = 3
  formula = G4_GUANINE
  name = G4_GUANINE
  specific = 4
FEATURE [App::DocumentObjectGroupPython] Ca_element012  label="Ca_element : 006"  # scripted group (container) (typed FeaturePython)
  n = 1
  ref = Ca_element
FEATURE [App::DocumentObjectGroupPython] S_element014  label="S_element : 005"  # scripted group (container) (typed FeaturePython)
  n = 1
  ref = S_element
FEATURE [App::DocumentObjectGroupPython] O_element049  label="O_element : 6"  # scripted group (container) (typed FeaturePython)
  n = 6
  ref = O_element
FEATURE [App::DocumentObjectGroupPython] H_element045  label="H_element : 024"  # scripted group (container) (typed FeaturePython)
  n = 4
  ref = H_element
FEATURE [App::DocumentObjectGroupPython] G4_GYPSUM  # scripted group (container) (typed FeaturePython)
  Dunit = g/cm3
  Dvalue = 2.32
  Group = -> [Ca_element012,S_element014,O_element049,H_element045]
  conduct = 2
  density = 1
  expand = 3
  formula = G4_GYPSUM
  name = G4_GYPSUM
  specific = 4
FEATURE [App::DocumentObjectGroupPython] C_element052  label="C_element : 7"  # scripted group (container) (typed FeaturePython)
  n = 7
  ref = C_element
FEATURE [App::DocumentObjectGroupPython] H_element046  label="H_element : 16"  # scripted group (container) (typed FeaturePython)
  n = 16
  ref = H_element
FEATURE [App::DocumentObjectGroupPython] G4_N_HEPTANE  label="G4_N-HEPTANE"  # scripted group (container) (typed FeaturePython)
  Dunit = g/cm3
  Dvalue = 0.68376
  Group = -> [C_element052,H_element046]
  conduct = 2
  density = 1
  expand = 3
  formula = G4_N-HEPTANE
  name = G4_N-HEPTANE
  specific = 4
FEATURE [App::DocumentObjectGroupPython] C_element053  label="C_element : 029"  # scripted group (container) (typed FeaturePython)
  n = 6
  ref = C_element
FEATURE [App::DocumentObjectGroupPython] H_element047  label="H_element : 14"  # scripted group (container) (typed FeaturePython)
  n = 14
  ref = H_element
FEATURE [App::DocumentObjectGroupPython] G4_N_HEXANE  label="G4_N-HEXANE"  # scripted group (container) (typed FeaturePython)
  Dunit = g/cm3
  Dvalue = 0.6603
  Group = -> [C_element053,H_element047]
  conduct = 2
  density = 1
  expand = 3
  formula = G4_N-HEXANE
  name = G4_N-HEXANE
  specific = 4
FEATURE [App::DocumentObjectGroupPython] C_element054  label="C_element : 22"  # scripted group (container) (typed FeaturePython)
  n = 22
  ref = C_element
FEATURE [App::DocumentObjectGroupPython] H_element048  label="H_element : 025"  # scripted group (container) (typed FeaturePython)
  n = 10
  ref = H_element
FEATURE [App::DocumentObjectGroupPython] N_element021  label="N_element : 010"  # scripted group (container) (typed FeaturePython)
  n = 2
  ref = N_element
FEATURE [App::DocumentObjectGroupPython] O_element050  label="O_element : 025"  # scripted group (container) (typed FeaturePython)
  n = 5
  ref = O_element
FEATURE [App::DocumentObjectGroupPython] G4_KAPTON  # scripted group (container) (typed FeaturePython)
  Dunit = g/cm3
  Dvalue = 1.42
  Group = -> [C_element054,H_element048,N_element021,O_element050]
  conduct = 2
  density = 1
  expand = 3
  formula = G4_KAPTON
  name = G4_KAPTON
  specific = 4
FEATURE [App::DocumentObjectGroupPython] La_element001  label="La_element : 1"  # scripted group (container) (typed FeaturePython)
  n = 1
  ref = La_element
FEATURE [App::DocumentObjectGroupPython] Br_element003  label="Br_element : 002"  # scripted group (container) (typed FeaturePython)
  n = 1
  ref = Br_element
FEATURE [App::DocumentObjectGroupPython] O_element051  label="O_element : 026"  # scripted group (container) (typed FeaturePython)
  n = 1
  ref = O_element
FEATURE [App::DocumentObjectGroupPython] G4_LANTHANUM_OXYBROMIDE  # scripted group (container) (typed FeaturePython)
  Dunit = g/cm3
  Dvalue = 6.28
  Group = -> [La_element001,Br_element003,O_element051]
  conduct = 2
  density = 1
  expand = 3
  formula = G4_LANTHANUM_OXYBROMIDE
  name = G4_LANTHANUM_OXYBROMIDE
  specific = 4
FEATURE [App::DocumentObjectGroupPython] La_element002  label="La_element : 2"  # scripted group (container) (typed FeaturePython)
  n = 2
  ref = La_element
FEATURE [App::DocumentObjectGroupPython] O_element052  label="O_element : 027"  # scripted group (container) (typed FeaturePython)
  n = 2
  ref = O_element
FEATURE [App::DocumentObjectGroupPython] S_element015  label="S_element : 006"  # scripted group (container) (typed FeaturePython)
  n = 1
  ref = S_element
FEATURE [App::DocumentObjectGroupPython] G4_LANTHANUM_OXYSULFIDE  # scripted group (container) (typed FeaturePython)
  Dunit = g/cm3
  Dvalue = 5.86
  Group = -> [La_element002,O_element052,S_element015]
  conduct = 2
  density = 1
  expand = 3
  formula = G4_LANTHANUM_OXYSULFIDE
  name = G4_LANTHANUM_OXYSULFIDE
  specific = 4
FEATURE [App::DocumentObjectGroupPython] O_element053  label="O_element : 0.072"  # scripted group (container) (typed FeaturePython)
  n = 0.071682
FEATURE [App::DocumentObjectGroupPython] Pb_element002  label="Pb_element : 0.928"  # scripted group (container) (typed FeaturePython)
  n = 0.928318
FEATURE [App::DocumentObjectGroupPython] G4_LEAD_OXIDE  # scripted group (container) (typed FeaturePython)
  Dunit = g/cm3
  Dvalue = 9.53
  Group = -> [O_element053,Pb_element002]
  conduct = 2
  density = 1
  expand = 3
  formula = G4_LEAD_OXIDE
  name = G4_LEAD_OXIDE
  specific = 4
FEATURE [App::DocumentObjectGroupPython] Li_element001  label="Li_element : 1"  # scripted group (container) (typed FeaturePython)
  n = 1
  ref = Li_element
FEATURE [App::DocumentObjectGroupPython] N_element022  label="N_element : 011"  # scripted group (container) (typed FeaturePython)
  n = 1
  ref = N_element
FEATURE [App::DocumentObjectGroupPython] H_element049  label="H_element : 026"  # scripted group (container) (typed FeaturePython)
  n = 2
  ref = H_element
FEATURE [App::DocumentObjectGroupPython] G4_LITHIUM_AMIDE  # scripted group (container) (typed FeaturePython)
  Dunit = g/cm3
  Dvalue = 1.178
  Group = -> [Li_element001,N_element022,H_element049]
  conduct = 2
  density = 1
  expand = 3
  formula = G4_LITHIUM_AMIDE
  name = G4_LITHIUM_AMIDE
  specific = 4
FEATURE [App::DocumentObjectGroupPython] Li_element002  label="Li_element : 2"  # scripted group (container) (typed FeaturePython)
  n = 2
  ref = Li_element
FEATURE [App::DocumentObjectGroupPython] C_element055  label="C_element : 030"  # scripted group (container) (typed FeaturePython)
  n = 1
  ref = C_element
FEATURE [App::DocumentObjectGroupPython] O_element054  label="O_element : 028"  # scripted group (container) (typed FeaturePython)
  n = 3
  ref = O_element
FEATURE [App::DocumentObjectGroupPython] G4_LITHIUM_CARBONATE  # scripted group (container) (typed FeaturePython)
  Dunit = g/cm3
  Dvalue = 2.11
  Group = -> [Li_element002,C_element055,O_element054]
  conduct = 2
  density = 1
  expand = 3
  formula = G4_LITHIUM_CARBONATE
  name = G4_LITHIUM_CARBONATE
  specific = 4
FEATURE [App::DocumentObjectGroupPython] Li_element003  label="Li_element : 003"  # scripted group (container) (typed FeaturePython)
  n = 1
  ref = Li_element
FEATURE [App::DocumentObjectGroupPython] F_element012  label="F_element : 004"  # scripted group (container) (typed FeaturePython)
  n = 1
  ref = F_element
FEATURE [App::DocumentObjectGroupPython] G4_LITHIUM_FLUORIDE  # scripted group (container) (typed FeaturePython)
  Dunit = g/cm3
  Dvalue = 2.635
  Group = -> [Li_element003,F_element012]
  conduct = 2
  density = 1
  expand = 3
  formula = G4_LITHIUM_FLUORIDE
  name = G4_LITHIUM_FLUORIDE
  specific = 4
FEATURE [App::DocumentObjectGroupPython] Li_element004  label="Li_element : 004"  # scripted group (container) (typed FeaturePython)
  n = 1
  ref = Li_element
FEATURE [App::DocumentObjectGroupPython] H_element050  label="H_element : 027"  # scripted group (container) (typed FeaturePython)
  n = 1
  ref = H_element
FEATURE [App::DocumentObjectGroupPython] G4_LITHIUM_HYDRIDE  # scripted group (container) (typed FeaturePython)
  Dunit = g/cm3
  Dvalue = 0.82
  Group = -> [Li_element004,H_element050]
  conduct = 2
  density = 1
  expand = 3
  formula = G4_LITHIUM_HYDRIDE
  name = G4_LITHIUM_HYDRIDE
  specific = 4
FEATURE [App::DocumentObjectGroupPython] Li_element005  label="Li_element : 005"  # scripted group (container) (typed FeaturePython)
  n = 1
  ref = Li_element
FEATURE [App::DocumentObjectGroupPython] I_element003  label="I_element : 002"  # scripted group (container) (typed FeaturePython)
  n = 1
  ref = I_element
FEATURE [App::DocumentObjectGroupPython] G4_LITHIUM_IODIDE  # scripted group (container) (typed FeaturePython)
  Dunit = g/cm3
  Dvalue = 3.494
  Group = -> [Li_element005,I_element003]
  conduct = 2
  density = 1
  expand = 3
  formula = G4_LITHIUM_IODIDE
  name = G4_LITHIUM_IODIDE
  specific = 4
FEATURE [App::DocumentObjectGroupPython] Li_element006  label="Li_element : 006"  # scripted group (container) (typed FeaturePython)
  n = 2
  ref = Li_element
FEATURE [App::DocumentObjectGroupPython] O_element055  label="O_element : 029"  # scripted group (container) (typed FeaturePython)
  n = 1
  ref = O_element
FEATURE [App::DocumentObjectGroupPython] G4_LITHIUM_OXIDE  # scripted group (container) (typed FeaturePython)
  Dunit = g/cm3
  Dvalue = 2.013
  Group = -> [Li_element006,O_element055]
  conduct = 2
  density = 1
  expand = 3
  formula = G4_LITHIUM_OXIDE
  name = G4_LITHIUM_OXIDE
  specific = 4
FEATURE [App::DocumentObjectGroupPython] Li_element007  label="Li_element : 007"  # scripted group (container) (typed FeaturePython)
  n = 2
  ref = Li_element
FEATURE [App::DocumentObjectGroupPython] B_element005  label="B_element : 005"  # scripted group (container) (typed FeaturePython)
  n = 4
  ref = B_element
FEATURE [App::DocumentObjectGroupPython] O_element056  label="O_element : 7"  # scripted group (container) (typed FeaturePython)
  n = 7
  ref = O_element
FEATURE [App::DocumentObjectGroupPython] G4_LITHIUM_TETRABORATE  # scripted group (container) (typed FeaturePython)
  Dunit = g/cm3
  Dvalue = 2.44
  Group = -> [Li_element007,B_element005,O_element056]
  conduct = 2
  density = 1
  expand = 3
  formula = G4_LITHIUM_TETRABORATE
  name = G4_LITHIUM_TETRABORATE
  specific = 4
FEATURE [App::DocumentObjectGroupPython] H_element051  label="H_element : 0.105"  # scripted group (container) (typed FeaturePython)
  n = 0.105
FEATURE [App::DocumentObjectGroupPython] C_element056  label="C_element : 0.083"  # scripted group (container) (typed FeaturePython)
  n = 0.083
FEATURE [App::DocumentObjectGroupPython] N_element023  label="N_element : 0.023"  # scripted group (container) (typed FeaturePython)
  n = 0.023
FEATURE [App::DocumentObjectGroupPython] O_element057  label="O_element : 0.779"  # scripted group (container) (typed FeaturePython)
  n = 0.779
FEATURE [App::DocumentObjectGroupPython] Na_element010  label="Na_element : 0.097"  # scripted group (container) (typed FeaturePython)
  n = 0.002
FEATURE [App::DocumentObjectGroupPython] P_element006  label="P_element : 0.105"  # scripted group (container) (typed FeaturePython)
  n = 0.001
FEATURE [App::DocumentObjectGroupPython] S_element016  label="S_element : 0.017"  # scripted group (container) (typed FeaturePython)
  n = 0.002
FEATURE [App::DocumentObjectGroupPython] Cl_element014  label="Cl_element : 0.587"  # scripted group (container) (typed FeaturePython)
  n = 0.003
FEATURE [App::DocumentObjectGroupPython] K_element005  label="K_element : 0.015"  # scripted group (container) (typed FeaturePython)
  n = 0.002
FEATURE [App::DocumentObjectGroupPython] G4_LUNG_ICRP  # scripted group (container) (typed FeaturePython)
  Dunit = g/cm3
  Dvalue = 1.04
  Group = -> [H_element051,C_element056,N_element023,O_element057,Na_element010,P_element006,S_element016,Cl_element014,K_element005]
  conduct = 2
  density = 1
  expand = 3
  formula = G4_LUNG_ICRP
  name = G4_LUNG_ICRP
  specific = 4
FEATURE [App::DocumentObjectGroupPython] H_element052  label="H_element : 0.116"  # scripted group (container) (typed FeaturePython)
  n = 0.114318
FEATURE [App::DocumentObjectGroupPython] C_element057  label="C_element : 0.656"  # scripted group (container) (typed FeaturePython)
  n = 0.655824
FEATURE [App::DocumentObjectGroupPython] O_element058  label="O_element : 0.092"  # scripted group (container) (typed FeaturePython)
  n = 0.0921831
FEATURE [App::DocumentObjectGroupPython] Mg_element004  label="Mg_element : 0.135"  # scripted group (container) (typed FeaturePython)
  n = 0.134792
FEATURE [App::DocumentObjectGroupPython] Ca_element013  label="Ca_element : 0.003"  # scripted group (container) (typed FeaturePython)
  n = 0.002883
FEATURE [App::DocumentObjectGroupPython] G4_M3_WAX  # scripted group (container) (typed FeaturePython)
  Dunit = g/cm3
  Dvalue = 1.05
  Group = -> [H_element052,C_element057,O_element058,Mg_element004,Ca_element013]
  conduct = 2
  density = 1
  expand = 3
  formula = G4_M3_WAX
  name = G4_M3_WAX
  specific = 4
FEATURE [App::DocumentObjectGroupPython] Mg_element005  label="Mg_element : 1"  # scripted group (container) (typed FeaturePython)
  n = 1
  ref = Mg_element
FEATURE [App::DocumentObjectGroupPython] C_element058  label="C_element : 031"  # scripted group (container) (typed FeaturePython)
  n = 1
  ref = C_element
FEATURE [App::DocumentObjectGroupPython] O_element059  label="O_element : 030"  # scripted group (container) (typed FeaturePython)
  n = 3
  ref = O_element
FEATURE [App::DocumentObjectGroupPython] G4_MAGNESIUM_CARBONATE  # scripted group (container) (typed FeaturePython)
  Dunit = g/cm3
  Dvalue = 2.958
  Group = -> [Mg_element005,C_element058,O_element059]
  conduct = 2
  density = 1
  expand = 3
  formula = G4_MAGNESIUM_CARBONATE
  name = G4_MAGNESIUM_CARBONATE
  specific = 4
FEATURE [App::DocumentObjectGroupPython] Mg_element006  label="Mg_element : 002"  # scripted group (container) (typed FeaturePython)
  n = 1
  ref = Mg_element
FEATURE [App::DocumentObjectGroupPython] F_element013  label="F_element : 005"  # scripted group (container) (typed FeaturePython)
  n = 2
  ref = F_element
FEATURE [App::DocumentObjectGroupPython] G4_MAGNESIUM_FLUORIDE  # scripted group (container) (typed FeaturePython)
  Dunit = g/cm3
  Dvalue = 3
  Group = -> [Mg_element006,F_element013]
  conduct = 2
  density = 1
  expand = 3
  formula = G4_MAGNESIUM_FLUORIDE
  name = G4_MAGNESIUM_FLUORIDE
  specific = 4
FEATURE [App::DocumentObjectGroupPython] Mg_element007  label="Mg_element : 003"  # scripted group (container) (typed FeaturePython)
  n = 1
  ref = Mg_element
FEATURE [App::DocumentObjectGroupPython] O_element060  label="O_element : 031"  # scripted group (container) (typed FeaturePython)
  n = 1
  ref = O_element
FEATURE [App::DocumentObjectGroupPython] G4_MAGNESIUM_OXIDE  # scripted group (container) (typed FeaturePython)
  Dunit = g/cm3
  Dvalue = 3.58
  Group = -> [Mg_element007,O_element060]
  conduct = 2
  density = 1
  expand = 3
  formula = G4_MAGNESIUM_OXIDE
  name = G4_MAGNESIUM_OXIDE
  specific = 4
FEATURE [App::DocumentObjectGroupPython] Mg_element008  label="Mg_element : 004"  # scripted group (container) (typed FeaturePython)
  n = 1
  ref = Mg_element
FEATURE [App::DocumentObjectGroupPython] B_element006  label="B_element : 006"  # scripted group (container) (typed FeaturePython)
  n = 4
  ref = B_element
FEATURE [App::DocumentObjectGroupPython] O_element061  label="O_element : 032"  # scripted group (container) (typed FeaturePython)
  n = 7
  ref = O_element
FEATURE [App::DocumentObjectGroupPython] G4_MAGNESIUM_TETRABORATE  # scripted group (container) (typed FeaturePython)
  Dunit = g/cm3
  Dvalue = 2.53
  Group = -> [Mg_element008,B_element006,O_element061]
  conduct = 2
  density = 1
  expand = 3
  formula = G4_MAGNESIUM_TETRABORATE
  name = G4_MAGNESIUM_TETRABORATE
  specific = 4
FEATURE [App::DocumentObjectGroupPython] Hg_element001  label="Hg_element : 1"  # scripted group (container) (typed FeaturePython)
  n = 1
  ref = Hg_element
FEATURE [App::DocumentObjectGroupPython] I_element004  label="I_element : 2"  # scripted group (container) (typed FeaturePython)
  n = 2
  ref = I_element
FEATURE [App::DocumentObjectGroupPython] G4_MERCURIC_IODIDE  # scripted group (container) (typed FeaturePython)
  Dunit = g/cm3
  Dvalue = 6.36
  Group = -> [Hg_element001,I_element004]
  conduct = 2
  density = 1
  expand = 3
  formula = G4_MERCURIC_IODIDE
  name = G4_MERCURIC_IODIDE
  specific = 4
FEATURE [App::DocumentObjectGroupPython] C_element059  label="C_element : 032"  # scripted group (container) (typed FeaturePython)
  n = 1
  ref = C_element
FEATURE [App::DocumentObjectGroupPython] H_element053  label="H_element : 028"  # scripted group (container) (typed FeaturePython)
  n = 4
  ref = H_element
FEATURE [App::DocumentObjectGroupPython] G4_METHANE  # scripted group (container) (typed FeaturePython)
  Dunit = g/cm3
  Dvalue = 0.000667151
  Group = -> [C_element059,H_element053]
  conduct = 2
  density = 1
  expand = 3
  formula = G4_METHANE
  name = G4_METHANE
  specific = 4
FEATURE [App::DocumentObjectGroupPython] C_element060  label="C_element : 033"  # scripted group (container) (typed FeaturePython)
  n = 1
  ref = C_element
FEATURE [App::DocumentObjectGroupPython] H_element054  label="H_element : 029"  # scripted group (container) (typed FeaturePython)
  n = 4
  ref = H_element
FEATURE [App::DocumentObjectGroupPython] O_element062  label="O_element : 033"  # scripted group (container) (typed FeaturePython)
  n = 1
  ref = O_element
FEATURE [App::DocumentObjectGroupPython] G4_METHANOL  # scripted group (container) (typed FeaturePython)
  Dunit = g/cm3
  Dvalue = 0.7914
  Group = -> [C_element060,H_element054,O_element062]
  conduct = 2
  density = 1
  expand = 3
  formula = G4_METHANOL
  name = G4_METHANOL
  specific = 4
FEATURE [App::DocumentObjectGroupPython] H_element055  label="H_element : 0.134"  # scripted group (container) (typed FeaturePython)
  n = 0.13404
FEATURE [App::DocumentObjectGroupPython] C_element061  label="C_element : 0.778"  # scripted group (container) (typed FeaturePython)
  n = 0.77796
FEATURE [App::DocumentObjectGroupPython] O_element063  label="O_element : 0.035"  # scripted group (container) (typed FeaturePython)
  n = 0.03502
FEATURE [App::DocumentObjectGroupPython] Mg_element009  label="Mg_element : 0.039"  # scripted group (container) (typed FeaturePython)
  n = 0.038594
FEATURE [App::DocumentObjectGroupPython] Ti_element002  label="Ti_element : 0.014"  # scripted group (container) (typed FeaturePython)
  n = 0.014386
FEATURE [App::DocumentObjectGroupPython] G4_MIX_D_WAX  # scripted group (container) (typed FeaturePython)
  Dunit = g/cm3
  Dvalue = 0.99
  Group = -> [H_element055,C_element061,O_element063,Mg_element009,Ti_element002]
  conduct = 2
  density = 1
  expand = 3
  formula = G4_MIX_D_WAX
  name = G4_MIX_D_WAX
  specific = 4
FEATURE [App::DocumentObjectGroupPython] H_element056  label="H_element : 0.135"  # scripted group (container) (typed FeaturePython)
  n = 0.081192
FEATURE [App::DocumentObjectGroupPython] C_element062  label="C_element : 0.583"  # scripted group (container) (typed FeaturePython)
  n = 0.583442
FEATURE [App::DocumentObjectGroupPython] N_element024  label="N_element : 0.018"  # scripted group (container) (typed FeaturePython)
  n = 0.017798
FEATURE [App::DocumentObjectGroupPython] O_element064  label="O_element : 0.186"  # scripted group (container) (typed FeaturePython)
  n = 0.186381
FEATURE [App::DocumentObjectGroupPython] Mg_element010  label="Mg_element : 0.130"  # scripted group (container) (typed FeaturePython)
  n = 0.130287
FEATURE [App::DocumentObjectGroupPython] Cl_element015  label="Cl_element : 0.588"  # scripted group (container) (typed FeaturePython)
  n = 0.0009
FEATURE [App::DocumentObjectGroupPython] G4_MS20_TISSUE  # scripted group (container) (typed FeaturePython)
  Dunit = g/cm3
  Dvalue = 1
  Group = -> [H_element056,C_element062,N_element024,O_element064,Mg_element010,Cl_element015]
  conduct = 2
  density = 1
  expand = 3
  formula = G4_MS20_TISSUE
  name = G4_MS20_TISSUE
  specific = 4
FEATURE [App::DocumentObjectGroupPython] H_element057  label="H_element : 0.136"  # scripted group (container) (typed FeaturePython)
  n = 0.102
FEATURE [App::DocumentObjectGroupPython] C_element063  label="C_element : 0.143"  # scripted group (container) (typed FeaturePython)
  n = 0.143
FEATURE [App::DocumentObjectGroupPython] N_element025  label="N_element : 0.034"  # scripted group (container) (typed FeaturePython)
  n = 0.034
FEATURE [App::DocumentObjectGroupPython] O_element065  label="O_element : 0.710"  # scripted group (container) (typed FeaturePython)
  n = 0.71
FEATURE [App::DocumentObjectGroupPython] Na_element011  label="Na_element : 0.098"  # scripted group (container) (typed FeaturePython)
  n = 0.001
FEATURE [App::DocumentObjectGroupPython] P_element007  label="P_element : 0.002"  # scripted group (container) (typed FeaturePython)
  n = 0.002
FEATURE [App::DocumentObjectGroupPython] S_element017  label="S_element : 0.018"  # scripted group (container) (typed FeaturePython)
  n = 0.003
FEATURE [App::DocumentObjectGroupPython] Cl_element016  label="Cl_element : 0.589"  # scripted group (container) (typed FeaturePython)
  n = 0.001
FEATURE [App::DocumentObjectGroupPython] K_element006  label="K_element : 0.004"  # scripted group (container) (typed FeaturePython)
  n = 0.004
FEATURE [App::DocumentObjectGroupPython] G4_MUSCLE_SKELETAL_ICRP  # scripted group (container) (typed FeaturePython)
  Dunit = g/cm3
  Dvalue = 1.05
  Group = -> [H_element057,C_element063,N_element025,O_element065,Na_element011,P_element007,S_element017,Cl_element016,K_element006]
  conduct = 2
  density = 1
  expand = 3
  formula = G4_MUSCLE_SKELETAL_ICRP
  name = G4_MUSCLE_SKELETAL_ICRP
  specific = 4
FEATURE [App::DocumentObjectGroupPython] H_element058  label="H_element : 0.137"  # scripted group (container) (typed FeaturePython)
  n = 0.102102
FEATURE [App::DocumentObjectGroupPython] C_element064  label="C_element : 0.123"  # scripted group (container) (typed FeaturePython)
  n = 0.123123
FEATURE [App::DocumentObjectGroupPython] N_element026  label="N_element : 0.756"  # scripted group (container) (typed FeaturePython)
  n = 0.035035
FEATURE [App::DocumentObjectGroupPython] O_element066  label="O_element : 0.730"  # scripted group (container) (typed FeaturePython)
  n = 0.72973
FEATURE [App::DocumentObjectGroupPython] Na_element012  label="Na_element : 0.099"  # scripted group (container) (typed FeaturePython)
  n = 0.001001
FEATURE [App::DocumentObjectGroupPython] P_element008  label="P_element : 0.106"  # scripted group (container) (typed FeaturePython)
  n = 0.002002
FEATURE [App::DocumentObjectGroupPython] S_element018  label="S_element : 0.019"  # scripted group (container) (typed FeaturePython)
  n = 0.004004
FEATURE [App::DocumentObjectGroupPython] K_element007  label="K_element : 0.016"  # scripted group (container) (typed FeaturePython)
  n = 0.003003
FEATURE [App::DocumentObjectGroupPython] G4_MUSCLE_STRIATED_ICRU  # scripted group (container) (typed FeaturePython)
  Dunit = g/cm3
  Dvalue = 1.04
  Group = -> [H_element058,C_element064,N_element026,O_element066,Na_element012,P_element008,S_element018,K_element007]
  conduct = 2
  density = 1
  expand = 3
  formula = G4_MUSCLE_STRIATED_ICRU
  name = G4_MUSCLE_STRIATED_ICRU
  specific = 4
FEATURE [App::DocumentObjectGroupPython] H_element059  label="H_element : 0.098"  # scripted group (container) (typed FeaturePython)
  n = 0.0982341
FEATURE [App::DocumentObjectGroupPython] C_element065  label="C_element : 0.156"  # scripted group (container) (typed FeaturePython)
  n = 0.156214
FEATURE [App::DocumentObjectGroupPython] N_element027  label="N_element : 0.757"  # scripted group (container) (typed FeaturePython)
  n = 0.035451
FEATURE [App::DocumentObjectGroupPython] O_element067  label="O_element : 0.880"  # scripted group (container) (typed FeaturePython)
  n = 0.710101
FEATURE [App::DocumentObjectGroupPython] G4_MUSCLE_WITH_SUCROSE  # scripted group (container) (typed FeaturePython)
  Dunit = g/cm3
  Dvalue = 1.11
  Group = -> [H_element059,C_element065,N_element027,O_element067]
  conduct = 2
  density = 1
  expand = 3
  formula = G4_MUSCLE_WITH_SUCROSE
  name = G4_MUSCLE_WITH_SUCROSE
  specific = 4
FEATURE [App::DocumentObjectGroupPython] H_element060  label="H_element : 0.138"  # scripted group (container) (typed FeaturePython)
  n = 0.101969
FEATURE [App::DocumentObjectGroupPython] C_element066  label="C_element : 0.120"  # scripted group (container) (typed FeaturePython)
  n = 0.120058
FEATURE [App::DocumentObjectGroupPython] N_element028  label="N_element : 0.758"  # scripted group (container) (typed FeaturePython)
  n = 0.035451
FEATURE [App::DocumentObjectGroupPython] O_element068  label="O_element : 0.743"  # scripted group (container) (typed FeaturePython)
  n = 0.742522
FEATURE [App::DocumentObjectGroupPython] G4_MUSCLE_WITHOUT_SUCROSE  # scripted group (container) (typed FeaturePython)
  Dunit = g/cm3
  Dvalue = 1.07
  Group = -> [H_element060,C_element066,N_element028,O_element068]
  conduct = 2
  density = 1
  expand = 3
  formula = G4_MUSCLE_WITHOUT_SUCROSE
  name = G4_MUSCLE_WITHOUT_SUCROSE
  specific = 4
FEATURE [App::DocumentObjectGroupPython] C_element067  label="C_element : 10"  # scripted group (container) (typed FeaturePython)
  n = 10
  ref = C_element
FEATURE [App::DocumentObjectGroupPython] H_element061  label="H_element : 030"  # scripted group (container) (typed FeaturePython)
  n = 8
  ref = H_element
FEATURE [App::DocumentObjectGroupPython] G4_NAPHTHALENE  # scripted group (container) (typed FeaturePython)
  Dunit = g/cm3
  Dvalue = 1.145
  Group = -> [C_element067,H_element061]
  conduct = 2
  density = 1
  expand = 3
  formula = G4_NAPHTHALENE
  name = G4_NAPHTHALENE
  specific = 4
FEATURE [App::DocumentObjectGroupPython] C_element068  label="C_element : 034"  # scripted group (container) (typed FeaturePython)
  n = 6
  ref = C_element
FEATURE [App::DocumentObjectGroupPython] H_element062  label="H_element : 031"  # scripted group (container) (typed FeaturePython)
  n = 5
  ref = H_element
FEATURE [App::DocumentObjectGroupPython] N_element029  label="N_element : 012"  # scripted group (container) (typed FeaturePython)
  n = 1
  ref = N_element
FEATURE [App::DocumentObjectGroupPython] O_element069  label="O_element : 034"  # scripted group (container) (typed FeaturePython)
  n = 2
  ref = O_element
FEATURE [App::DocumentObjectGroupPython] G4_NITROBENZENE  # scripted group (container) (typed FeaturePython)
  Dunit = g/cm3
  Dvalue = 1.19867
  Group = -> [C_element068,H_element062,N_element029,O_element069]
  conduct = 2
  density = 1
  expand = 3
  formula = G4_NITROBENZENE
  name = G4_NITROBENZENE
  specific = 4
FEATURE [App::DocumentObjectGroupPython] N_element030  label="N_element : 013"  # scripted group (container) (typed FeaturePython)
  n = 2
  ref = N_element
FEATURE [App::DocumentObjectGroupPython] O_element070  label="O_element : 035"  # scripted group (container) (typed FeaturePython)
  n = 1
  ref = O_element
FEATURE [App::DocumentObjectGroupPython] G4_NITROUS_OXIDE  # scripted group (container) (typed FeaturePython)
  Dunit = g/cm3
  Dvalue = 0.00183094
  Group = -> [N_element030,O_element070]
  conduct = 2
  density = 1
  expand = 3
  formula = G4_NITROUS_OXIDE
  name = G4_NITROUS_OXIDE
  specific = 4
FEATURE [App::DocumentObjectGroupPython] H_element063  label="H_element : 0.104"  # scripted group (container) (typed FeaturePython)
  n = 0.103509
FEATURE [App::DocumentObjectGroupPython] C_element069  label="C_element : 0.648"  # scripted group (container) (typed FeaturePython)
  n = 0.648416
FEATURE [App::DocumentObjectGroupPython] N_element031  label="N_element : 0.100"  # scripted group (container) (typed FeaturePython)
  n = 0.0995361
FEATURE [App::DocumentObjectGroupPython] O_element071  label="O_element : 0.149"  # scripted group (container) (typed FeaturePython)
  n = 0.148539
FEATURE [App::DocumentObjectGroupPython] G4_NYLON_8062  label="G4_NYLON-8062"  # scripted group (container) (typed FeaturePython)
  Dunit = g/cm3
  Dvalue = 1.08
  Group = -> [H_element063,C_element069,N_element031,O_element071]
  conduct = 2
  density = 1
  expand = 3
  formula = G4_NYLON-8062
  name = G4_NYLON-8062
  specific = 4
FEATURE [App::DocumentObjectGroupPython] C_element070  label="C_element : 035"  # scripted group (container) (typed FeaturePython)
  n = 6
  ref = C_element
FEATURE [App::DocumentObjectGroupPython] H_element064  label="H_element : 11"  # scripted group (container) (typed FeaturePython)
  n = 11
  ref = H_element
FEATURE [App::DocumentObjectGroupPython] N_element032  label="N_element : 014"  # scripted group (container) (typed FeaturePython)
  n = 1
  ref = N_element
FEATURE [App::DocumentObjectGroupPython] O_element072  label="O_element : 036"  # scripted group (container) (typed FeaturePython)
  n = 1
  ref = O_element
FEATURE [App::DocumentObjectGroupPython] G4_NYLON_6_6  label="G4_NYLON-6-6"  # scripted group (container) (typed FeaturePython)
  Dunit = g/cm3
  Dvalue = 1.14
  Group = -> [C_element070,H_element064,N_element032,O_element072]
  conduct = 2
  density = 1
  expand = 3
  formula = G4_NYLON-6-6
  name = G4_NYLON-6-6
  specific = 4
FEATURE [App::DocumentObjectGroupPython] H_element065  label="H_element : 0.139"  # scripted group (container) (typed FeaturePython)
  n = 0.107062
FEATURE [App::DocumentObjectGroupPython] C_element071  label="C_element : 0.680"  # scripted group (container) (typed FeaturePython)
  n = 0.680449
FEATURE [App::DocumentObjectGroupPython] N_element033  label="N_element : 0.099"  # scripted group (container) (typed FeaturePython)
  n = 0.099189
FEATURE [App::DocumentObjectGroupPython] O_element073  label="O_element : 0.113"  # scripted group (container) (typed FeaturePython)
  n = 0.1133
FEATURE [App::DocumentObjectGroupPython] G4_NYLON_6_10  label="G4_NYLON-6-10"  # scripted group (container) (typed FeaturePython)
  Dunit = g/cm3
  Dvalue = 1.14
  Group = -> [H_element065,C_element071,N_element033,O_element073]
  conduct = 2
  density = 1
  expand = 3
  formula = G4_NYLON-6-10
  name = G4_NYLON-6-10
  specific = 4
FEATURE [App::DocumentObjectGroupPython] H_element066  label="H_element : 0.140"  # scripted group (container) (typed FeaturePython)
  n = 0.115476
FEATURE [App::DocumentObjectGroupPython] C_element072  label="C_element : 0.721"  # scripted group (container) (typed FeaturePython)
  n = 0.720818
FEATURE [App::DocumentObjectGroupPython] N_element034  label="N_element : 0.076"  # scripted group (container) (typed FeaturePython)
  n = 0.0764169
FEATURE [App::DocumentObjectGroupPython] O_element074  label="O_element : 0.087"  # scripted group (container) (typed FeaturePython)
  n = 0.0872889
FEATURE [App::DocumentObjectGroupPython] G4_NYLON_11_RILSAN  label="G4_NYLON-11_RILSAN"  # scripted group (container) (typed FeaturePython)
  Dunit = g/cm3
  Dvalue = 1.425
  Group = -> [H_element066,C_element072,N_element034,O_element074]
  conduct = 2
  density = 1
  expand = 3
  formula = G4_NYLON-11_RILSAN
  name = G4_NYLON-11_RILSAN
  specific = 4
FEATURE [App::DocumentObjectGroupPython] C_element073  label="C_element : 8"  # scripted group (container) (typed FeaturePython)
  n = 8
  ref = C_element
FEATURE [App::DocumentObjectGroupPython] H_element067  label="H_element : 18"  # scripted group (container) (typed FeaturePython)
  n = 18
  ref = H_element
FEATURE [App::DocumentObjectGroupPython] G4_OCTANE  # scripted group (container) (typed FeaturePython)
  Dunit = g/cm3
  Dvalue = 0.7026
  Group = -> [C_element073,H_element067]
  conduct = 2
  density = 1
  expand = 3
  formula = G4_OCTANE
  name = G4_OCTANE
  specific = 4
FEATURE [App::DocumentObjectGroupPython] C_element074  label="C_element : 25"  # scripted group (container) (typed FeaturePython)
  n = 25
  ref = C_element
FEATURE [App::DocumentObjectGroupPython] H_element068  label="H_element : 52"  # scripted group (container) (typed FeaturePython)
  n = 52
  ref = H_element
FEATURE [App::DocumentObjectGroupPython] G4_PARAFFIN  # scripted group (container) (typed FeaturePython)
  Dunit = g/cm3
  Dvalue = 0.93
  Group = -> [C_element074,H_element068]
  conduct = 2
  density = 1
  expand = 3
  formula = G4_PARAFFIN
  name = G4_PARAFFIN
  specific = 4
FEATURE [App::DocumentObjectGroupPython] C_element075  label="C_element : 036"  # scripted group (container) (typed FeaturePython)
  n = 5
  ref = C_element
FEATURE [App::DocumentObjectGroupPython] H_element069  label="H_element : 032"  # scripted group (container) (typed FeaturePython)
  n = 12
  ref = H_element
FEATURE [App::DocumentObjectGroupPython] G4_N_PENTANE  label="G4_N-PENTANE"  # scripted group (container) (typed FeaturePython)
  Dunit = g/cm3
  Dvalue = 0.6262
  Group = -> [C_element075,H_element069]
  conduct = 2
  density = 1
  expand = 3
  formula = G4_N-PENTANE
  name = G4_N-PENTANE
  specific = 4
FEATURE [App::DocumentObjectGroupPython] H_element070  label="H_element : 0.014"  # scripted group (container) (typed FeaturePython)
  n = 0.0141
FEATURE [App::DocumentObjectGroupPython] C_element076  label="C_element : 0.072"  # scripted group (container) (typed FeaturePython)
  n = 0.072261
FEATURE [App::DocumentObjectGroupPython] N_element035  label="N_element : 0.019"  # scripted group (container) (typed FeaturePython)
  n = 0.01932
FEATURE [App::DocumentObjectGroupPython] O_element075  label="O_element : 0.066"  # scripted group (container) (typed FeaturePython)
  n = 0.066101
FEATURE [App::DocumentObjectGroupPython] S_element019  label="S_element : 0.020"  # scripted group (container) (typed FeaturePython)
  n = 0.00189
FEATURE [App::DocumentObjectGroupPython] Br_element004  label="Br_element : 0.349"  # scripted group (container) (typed FeaturePython)
  n = 0.349103
FEATURE [App::DocumentObjectGroupPython] Ag_element001  label="Ag_element : 0.474"  # scripted group (container) (typed FeaturePython)
  n = 0.474105
FEATURE [App::DocumentObjectGroupPython] I_element005  label="I_element : 0.003"  # scripted group (container) (typed FeaturePython)
  n = 0.00312
FEATURE [App::DocumentObjectGroupPython] G4_PHOTO_EMULSION  # scripted group (container) (typed FeaturePython)
  Dunit = g/cm3
  Dvalue = 3.815
  Group = -> [H_element070,C_element076,N_element035,O_element075,S_element019,Br_element004,Ag_element001,I_element005]
  conduct = 2
  density = 1
  expand = 3
  formula = G4_PHOTO_EMULSION
  name = G4_PHOTO_EMULSION
  specific = 4
FEATURE [App::DocumentObjectGroupPython] C_element077  label="C_element : 9"  # scripted group (container) (typed FeaturePython)
  n = 9
  ref = C_element
FEATURE [App::DocumentObjectGroupPython] H_element071  label="H_element : 033"  # scripted group (container) (typed FeaturePython)
  n = 10
  ref = H_element
FEATURE [App::DocumentObjectGroupPython] G4_PLASTIC_SC_VINYLTOLUENE  # scripted group (container) (typed FeaturePython)
  Dunit = g/cm3
  Dvalue = 1.032
  Group = -> [C_element077,H_element071]
  conduct = 2
  density = 1
  expand = 3
  formula = G4_PLASTIC_SC_VINYLTOLUENE
  name = G4_PLASTIC_SC_VINYLTOLUENE
  specific = 4
FEATURE [App::DocumentObjectGroupPython] Pu_element001  label="Pu_element : 1"  # scripted group (container) (typed FeaturePython)
  n = 1
  ref = Pu_element
FEATURE [App::DocumentObjectGroupPython] O_element076  label="O_element : 037"  # scripted group (container) (typed FeaturePython)
  n = 2
  ref = O_element
FEATURE [App::DocumentObjectGroupPython] G4_PLUTONIUM_DIOXIDE  # scripted group (container) (typed FeaturePython)
  Dunit = g/cm3
  Dvalue = 11.46
  Group = -> [Pu_element001,O_element076]
  conduct = 2
  density = 1
  expand = 3
  formula = G4_PLUTONIUM_DIOXIDE
  name = G4_PLUTONIUM_DIOXIDE
  specific = 4
FEATURE [App::DocumentObjectGroupPython] C_element078  label="C_element : 037"  # scripted group (container) (typed FeaturePython)
  n = 3
  ref = C_element
FEATURE [App::DocumentObjectGroupPython] H_element072  label="H_element : 034"  # scripted group (container) (typed FeaturePython)
  n = 3
  ref = H_element
FEATURE [App::DocumentObjectGroupPython] N_element036  label="N_element : 015"  # scripted group (container) (typed FeaturePython)
  n = 1
  ref = N_element
FEATURE [App::DocumentObjectGroupPython] G4_POLYACRYLONITRILE  # scripted group (container) (typed FeaturePython)
  Dunit = g/cm3
  Dvalue = 1.17
  Group = -> [C_element078,H_element072,N_element036]
  conduct = 2
  density = 1
  expand = 3
  formula = G4_POLYACRYLONITRILE
  name = G4_POLYACRYLONITRILE
  specific = 4
FEATURE [App::DocumentObjectGroupPython] C_element079  label="C_element : 16"  # scripted group (container) (typed FeaturePython)
  n = 16
  ref = C_element
FEATURE [App::DocumentObjectGroupPython] H_element073  label="H_element : 035"  # scripted group (container) (typed FeaturePython)
  n = 14
  ref = H_element
FEATURE [App::DocumentObjectGroupPython] O_element077  label="O_element : 038"  # scripted group (container) (typed FeaturePython)
  n = 3
  ref = O_element
FEATURE [App::DocumentObjectGroupPython] G4_POLYCARBONATE  # scripted group (container) (typed FeaturePython)
  Dunit = g/cm3
  Dvalue = 1.2
  Group = -> [C_element079,H_element073,O_element077]
  conduct = 2
  density = 1
  expand = 3
  formula = G4_POLYCARBONATE
  name = G4_POLYCARBONATE
  specific = 4
FEATURE [App::DocumentObjectGroupPython] C_element080  label="C_element : 038"  # scripted group (container) (typed FeaturePython)
  n = 8
  ref = C_element
FEATURE [App::DocumentObjectGroupPython] H_element074  label="H_element : 036"  # scripted group (container) (typed FeaturePython)
  n = 7
  ref = H_element
FEATURE [App::DocumentObjectGroupPython] Cl_element017  label="Cl_element : 007"  # scripted group (container) (typed FeaturePython)
  n = 1
  ref = Cl_element
FEATURE [App::DocumentObjectGroupPython] G4_POLYCHLOROSTYRENE  # scripted group (container) (typed FeaturePython)
  Dunit = g/cm3
  Dvalue = 1.3
  Group = -> [C_element080,H_element074,Cl_element017]
  conduct = 2
  density = 1
  expand = 3
  formula = G4_POLYCHLOROSTYRENE
  name = G4_POLYCHLOROSTYRENE
  specific = 4
FEATURE [App::DocumentObjectGroupPython] C_element081  label="C_element : 039"  # scripted group (container) (typed FeaturePython)
  n = 1
  ref = C_element
FEATURE [App::DocumentObjectGroupPython] H_element075  label="H_element : 037"  # scripted group (container) (typed FeaturePython)
  n = 2
  ref = H_element
FEATURE [App::DocumentObjectGroupPython] G4_POLYETHYLENE  # scripted group (container) (typed FeaturePython)
  Dunit = g/cm3
  Dvalue = 0.94
  Group = -> [C_element081,H_element075]
  conduct = 2
  density = 1
  expand = 3
  formula = G4_POLYETHYLENE
  name = G4_POLYETHYLENE
  specific = 4
FEATURE [App::DocumentObjectGroupPython] C_element082  label="C_element : 040"  # scripted group (container) (typed FeaturePython)
  n = 10
  ref = C_element
FEATURE [App::DocumentObjectGroupPython] H_element076  label="H_element : 038"  # scripted group (container) (typed FeaturePython)
  n = 8
  ref = H_element
FEATURE [App::DocumentObjectGroupPython] O_element078  label="O_element : 039"  # scripted group (container) (typed FeaturePython)
  n = 4
  ref = O_element
FEATURE [App::DocumentObjectGroupPython] G4_MYLAR  # scripted group (container) (typed FeaturePython)
  Dunit = g/cm3
  Dvalue = 1.4
  Group = -> [C_element082,H_element076,O_element078]
  conduct = 2
  density = 1
  expand = 3
  formula = G4_MYLAR
  name = G4_MYLAR
  specific = 4
FEATURE [App::DocumentObjectGroupPython] C_element083  label="C_element : 041"  # scripted group (container) (typed FeaturePython)
  n = 5
  ref = C_element
FEATURE [App::DocumentObjectGroupPython] H_element077  label="H_element : 039"  # scripted group (container) (typed FeaturePython)
  n = 8
  ref = H_element
FEATURE [App::DocumentObjectGroupPython] O_element079  label="O_element : 040"  # scripted group (container) (typed FeaturePython)
  n = 2
  ref = O_element
FEATURE [App::DocumentObjectGroupPython] G4_PLEXIGLASS  # scripted group (container) (typed FeaturePython)
  Dunit = g/cm3
  Dvalue = 1.19
  Group = -> [C_element083,H_element077,O_element079]
  conduct = 2
  density = 1
  expand = 3
  formula = G4_PLEXIGLASS
  name = G4_PLEXIGLASS
  specific = 4
FEATURE [App::DocumentObjectGroupPython] C_element084  label="C_element : 042"  # scripted group (container) (typed FeaturePython)
  n = 1
  ref = C_element
FEATURE [App::DocumentObjectGroupPython] H_element078  label="H_element : 040"  # scripted group (container) (typed FeaturePython)
  n = 2
  ref = H_element
FEATURE [App::DocumentObjectGroupPython] O_element080  label="O_element : 041"  # scripted group (container) (typed FeaturePython)
  n = 1
  ref = O_element
FEATURE [App::DocumentObjectGroupPython] G4_POLYOXYMETHYLENE  # scripted group (container) (typed FeaturePython)
  Dunit = g/cm3
  Dvalue = 1.425
  Group = -> [C_element084,H_element078,O_element080]
  conduct = 2
  density = 1
  expand = 3
  formula = G4_POLYOXYMETHYLENE
  name = G4_POLYOXYMETHYLENE
  specific = 4
FEATURE [App::DocumentObjectGroupPython] C_element085  label="C_element : 043"  # scripted group (container) (typed FeaturePython)
  n = 2
  ref = C_element
FEATURE [App::DocumentObjectGroupPython] H_element079  label="H_element : 041"  # scripted group (container) (typed FeaturePython)
  n = 4
  ref = H_element
FEATURE [App::DocumentObjectGroupPython] G4_POLYPROPYLENE  # scripted group (container) (typed FeaturePython)
  Dunit = g/cm3
  Dvalue = 0.9
  Group = -> [C_element085,H_element079]
  conduct = 2
  density = 1
  expand = 3
  formula = G4_POLYPROPYLENE
  name = G4_POLYPROPYLENE
  specific = 4
FEATURE [App::DocumentObjectGroupPython] C_element086  label="C_element : 044"  # scripted group (container) (typed FeaturePython)
  n = 8
  ref = C_element
FEATURE [App::DocumentObjectGroupPython] H_element080  label="H_element : 042"  # scripted group (container) (typed FeaturePython)
  n = 8
  ref = H_element
FEATURE [App::DocumentObjectGroupPython] G4_POLYSTYRENE  # scripted group (container) (typed FeaturePython)
  Dunit = g/cm3
  Dvalue = 1.06
  Group = -> [C_element086,H_element080]
  conduct = 2
  density = 1
  expand = 3
  formula = G4_POLYSTYRENE
  name = G4_POLYSTYRENE
  specific = 4
FEATURE [App::DocumentObjectGroupPython] C_element087  label="C_element : 045"  # scripted group (container) (typed FeaturePython)
  n = 2
  ref = C_element
FEATURE [App::DocumentObjectGroupPython] F_element014  label="F_element : 4"  # scripted group (container) (typed FeaturePython)
  n = 4
  ref = F_element
FEATURE [App::DocumentObjectGroupPython] G4_TEFLON  # scripted group (container) (typed FeaturePython)
  Dunit = g/cm3
  Dvalue = 2.2
  Group = -> [C_element087,F_element014]
  conduct = 2
  density = 1
  expand = 3
  formula = G4_TEFLON
  name = G4_TEFLON
  specific = 4
FEATURE [App::DocumentObjectGroupPython] C_element088  label="C_element : 046"  # scripted group (container) (typed FeaturePython)
  n = 2
  ref = C_element
FEATURE [App::DocumentObjectGroupPython] F_element015  label="F_element : 006"  # scripted group (container) (typed FeaturePython)
  n = 3
  ref = F_element
FEATURE [App::DocumentObjectGroupPython] Cl_element018  label="Cl_element : 008"  # scripted group (container) (typed FeaturePython)
  n = 1
  ref = Cl_element
FEATURE [App::DocumentObjectGroupPython] G4_POLYTRIFLUOROCHLOROETHYLENE  # scripted group (container) (typed FeaturePython)
  Dunit = g/cm3
  Dvalue = 2.1
  Group = -> [C_element088,F_element015,Cl_element018]
  conduct = 2
  density = 1
  expand = 3
  formula = G4_POLYTRIFLUOROCHLOROETHYLENE
  name = G4_POLYTRIFLUOROCHLOROETHYLENE
  specific = 4
FEATURE [App::DocumentObjectGroupPython] C_element089  label="C_element : 047"  # scripted group (container) (typed FeaturePython)
  n = 4
  ref = C_element
FEATURE [App::DocumentObjectGroupPython] H_element081  label="H_element : 043"  # scripted group (container) (typed FeaturePython)
  n = 6
  ref = H_element
FEATURE [App::DocumentObjectGroupPython] O_element081  label="O_element : 042"  # scripted group (container) (typed FeaturePython)
  n = 2
  ref = O_element
FEATURE [App::DocumentObjectGroupPython] G4_POLYVINYL_ACETATE  # scripted group (container) (typed FeaturePython)
  Dunit = g/cm3
  Dvalue = 1.19
  Group = -> [C_element089,H_element081,O_element081]
  conduct = 2
  density = 1
  expand = 3
  formula = G4_POLYVINYL_ACETATE
  name = G4_POLYVINYL_ACETATE
  specific = 4
FEATURE [App::DocumentObjectGroupPython] C_element090  label="C_element : 048"  # scripted group (container) (typed FeaturePython)
  n = 2
  ref = C_element
FEATURE [App::DocumentObjectGroupPython] H_element082  label="H_element : 044"  # scripted group (container) (typed FeaturePython)
  n = 4
  ref = H_element
FEATURE [App::DocumentObjectGroupPython] O_element082  label="O_element : 043"  # scripted group (container) (typed FeaturePython)
  n = 1
  ref = O_element
FEATURE [App::DocumentObjectGroupPython] G4_POLYVINYL_ALCOHOL  # scripted group (container) (typed FeaturePython)
  Dunit = g/cm3
  Dvalue = 1.3
  Group = -> [C_element090,H_element082,O_element082]
  conduct = 2
  density = 1
  expand = 3
  formula = G4_POLYVINYL_ALCOHOL
  name = G4_POLYVINYL_ALCOHOL
  specific = 4
FEATURE [App::DocumentObjectGroupPython] C_element091  label="C_element : 049"  # scripted group (container) (typed FeaturePython)
  n = 8
  ref = C_element
FEATURE [App::DocumentObjectGroupPython] H_element083  label="H_element : 045"  # scripted group (container) (typed FeaturePython)
  n = 14
  ref = H_element
FEATURE [App::DocumentObjectGroupPython] O_element083  label="O_element : 044"  # scripted group (container) (typed FeaturePython)
  n = 2
  ref = O_element
FEATURE [App::DocumentObjectGroupPython] G4_POLYVINYL_BUTYRAL  # scripted group (container) (typed FeaturePython)
  Dunit = g/cm3
  Dvalue = 1.12
  Group = -> [C_element091,H_element083,O_element083]
  conduct = 2
  density = 1
  expand = 3
  formula = G4_POLYVINYL_BUTYRAL
  name = G4_POLYVINYL_BUTYRAL
  specific = 4
FEATURE [App::DocumentObjectGroupPython] C_element092  label="C_element : 050"  # scripted group (container) (typed FeaturePython)
  n = 2
  ref = C_element
FEATURE [App::DocumentObjectGroupPython] H_element084  label="H_element : 046"  # scripted group (container) (typed FeaturePython)
  n = 3
  ref = H_element
FEATURE [App::DocumentObjectGroupPython] Cl_element019  label="Cl_element : 009"  # scripted group (container) (typed FeaturePython)
  n = 1
  ref = Cl_element
FEATURE [App::DocumentObjectGroupPython] G4_POLYVINYL_CHLORIDE  # scripted group (container) (typed FeaturePython)
  Dunit = g/cm3
  Dvalue = 1.3
  Group = -> [C_element092,H_element084,Cl_element019]
  conduct = 2
  density = 1
  expand = 3
  formula = G4_POLYVINYL_CHLORIDE
  name = G4_POLYVINYL_CHLORIDE
  specific = 4
FEATURE [App::DocumentObjectGroupPython] C_element093  label="C_element : 051"  # scripted group (container) (typed FeaturePython)
  n = 2
  ref = C_element
FEATURE [App::DocumentObjectGroupPython] H_element085  label="H_element : 047"  # scripted group (container) (typed FeaturePython)
  n = 2
  ref = H_element
FEATURE [App::DocumentObjectGroupPython] Cl_element020  label="Cl_element : 010"  # scripted group (container) (typed FeaturePython)
  n = 2
  ref = Cl_element
FEATURE [App::DocumentObjectGroupPython] G4_POLYVINYLIDENE_CHLORIDE  # scripted group (container) (typed FeaturePython)
  Dunit = g/cm3
  Dvalue = 1.7
  Group = -> [C_element093,H_element085,Cl_element020]
  conduct = 2
  density = 1
  expand = 3
  formula = G4_POLYVINYLIDENE_CHLORIDE
  name = G4_POLYVINYLIDENE_CHLORIDE
  specific = 4
FEATURE [App::DocumentObjectGroupPython] C_element094  label="C_element : 052"  # scripted group (container) (typed FeaturePython)
  n = 2
  ref = C_element
FEATURE [App::DocumentObjectGroupPython] H_element086  label="H_element : 048"  # scripted group (container) (typed FeaturePython)
  n = 2
  ref = H_element
FEATURE [App::DocumentObjectGroupPython] F_element016  label="F_element : 007"  # scripted group (container) (typed FeaturePython)
  n = 2
  ref = F_element
FEATURE [App::DocumentObjectGroupPython] G4_POLYVINYLIDENE_FLUORIDE  # scripted group (container) (typed FeaturePython)
  Dunit = g/cm3
  Dvalue = 1.76
  Group = -> [C_element094,H_element086,F_element016]
  conduct = 2
  density = 1
  expand = 3
  formula = G4_POLYVINYLIDENE_FLUORIDE
  name = G4_POLYVINYLIDENE_FLUORIDE
  specific = 4
FEATURE [App::DocumentObjectGroupPython] C_element095  label="C_element : 053"  # scripted group (container) (typed FeaturePython)
  n = 6
  ref = C_element
FEATURE [App::DocumentObjectGroupPython] H_element087  label="H_element : 9"  # scripted group (container) (typed FeaturePython)
  n = 9
  ref = H_element
FEATURE [App::DocumentObjectGroupPython] N_element037  label="N_element : 016"  # scripted group (container) (typed FeaturePython)
  n = 1
  ref = N_element
FEATURE [App::DocumentObjectGroupPython] O_element084  label="O_element : 045"  # scripted group (container) (typed FeaturePython)
  n = 1
  ref = O_element
FEATURE [App::DocumentObjectGroupPython] G4_POLYVINYL_PYRROLIDONE  # scripted group (container) (typed FeaturePython)
  Dunit = g/cm3
  Dvalue = 1.25
  Group = -> [C_element095,H_element087,N_element037,O_element084]
  conduct = 2
  density = 1
  expand = 3
  formula = G4_POLYVINYL_PYRROLIDONE
  name = G4_POLYVINYL_PYRROLIDONE
  specific = 4
FEATURE [App::DocumentObjectGroupPython] K_element008  label="K_element : 1"  # scripted group (container) (typed FeaturePython)
  n = 1
  ref = K_element
FEATURE [App::DocumentObjectGroupPython] I_element006  label="I_element : 003"  # scripted group (container) (typed FeaturePython)
  n = 1
  ref = I_element
FEATURE [App::DocumentObjectGroupPython] G4_POTASSIUM_IODIDE  # scripted group (container) (typed FeaturePython)
  Dunit = g/cm3
  Dvalue = 3.13
  Group = -> [K_element008,I_element006]
  conduct = 2
  density = 1
  expand = 3
  formula = G4_POTASSIUM_IODIDE
  name = G4_POTASSIUM_IODIDE
  specific = 4
FEATURE [App::DocumentObjectGroupPython] K_element009  label="K_element : 2"  # scripted group (container) (typed FeaturePython)
  n = 2
  ref = K_element
FEATURE [App::DocumentObjectGroupPython] O_element085  label="O_element : 046"  # scripted group (container) (typed FeaturePython)
  n = 1
  ref = O_element
FEATURE [App::DocumentObjectGroupPython] G4_POTASSIUM_OXIDE  # scripted group (container) (typed FeaturePython)
  Dunit = g/cm3
  Dvalue = 2.32
  Group = -> [K_element009,O_element085]
  conduct = 2
  density = 1
  expand = 3
  formula = G4_POTASSIUM_OXIDE
  name = G4_POTASSIUM_OXIDE
  specific = 4
FEATURE [App::DocumentObjectGroupPython] C_element096  label="C_element : 054"  # scripted group (container) (typed FeaturePython)
  n = 3
  ref = C_element
FEATURE [App::DocumentObjectGroupPython] H_element088  label="H_element : 049"  # scripted group (container) (typed FeaturePython)
  n = 8
  ref = H_element
FEATURE [App::DocumentObjectGroupPython] G4_PROPANE  # scripted group (container) (typed FeaturePython)
  Dunit = g/cm3
  Dvalue = 0.00187939
  Group = -> [C_element096,H_element088]
  conduct = 2
  density = 1
  expand = 3
  formula = G4_PROPANE
  name = G4_PROPANE
  specific = 4
FEATURE [App::DocumentObjectGroupPython] C_element097  label="C_element : 055"  # scripted group (container) (typed FeaturePython)
  n = 3
  ref = C_element
FEATURE [App::DocumentObjectGroupPython] H_element089  label="H_element : 050"  # scripted group (container) (typed FeaturePython)
  n = 8
  ref = H_element
FEATURE [App::DocumentObjectGroupPython] G4_lPROPANE  # scripted group (container) (typed FeaturePython)
  Dunit = g/cm3
  Dvalue = 0.43
  Group = -> [C_element097,H_element089]
  conduct = 2
  density = 1
  expand = 3
  formula = G4_lPROPANE
  name = G4_lPROPANE
  specific = 4
FEATURE [App::DocumentObjectGroupPython] C_element098  label="C_element : 056"  # scripted group (container) (typed FeaturePython)
  n = 3
  ref = C_element
FEATURE [App::DocumentObjectGroupPython] H_element090  label="H_element : 051"  # scripted group (container) (typed FeaturePython)
  n = 8
  ref = H_element
FEATURE [App::DocumentObjectGroupPython] O_element086  label="O_element : 047"  # scripted group (container) (typed FeaturePython)
  n = 1
  ref = O_element
FEATURE [App::DocumentObjectGroupPython] G4_N_PROPYL_ALCOHOL  label="G4_N-PROPYL_ALCOHOL"  # scripted group (container) (typed FeaturePython)
  Dunit = g/cm3
  Dvalue = 0.8035
  Group = -> [C_element098,H_element090,O_element086]
  conduct = 2
  density = 1
  expand = 3
  formula = G4_N-PROPYL_ALCOHOL
  name = G4_N-PROPYL_ALCOHOL
  specific = 4
FEATURE [App::DocumentObjectGroupPython] C_element099  label="C_element : 057"  # scripted group (container) (typed FeaturePython)
  n = 5
  ref = C_element
FEATURE [App::DocumentObjectGroupPython] H_element091  label="H_element : 052"  # scripted group (container) (typed FeaturePython)
  n = 5
  ref = H_element
FEATURE [App::DocumentObjectGroupPython] N_element038  label="N_element : 017"  # scripted group (container) (typed FeaturePython)
  n = 1
  ref = N_element
FEATURE [App::DocumentObjectGroupPython] G4_PYRIDINE  # scripted group (container) (typed FeaturePython)
  Dunit = g/cm3
  Dvalue = 0.9819
  Group = -> [C_element099,H_element091,N_element038]
  conduct = 2
  density = 1
  expand = 3
  formula = G4_PYRIDINE
  name = G4_PYRIDINE
  specific = 4
FEATURE [App::DocumentObjectGroupPython] H_element092  label="H_element : 0.144"  # scripted group (container) (typed FeaturePython)
  n = 0.143711
FEATURE [App::DocumentObjectGroupPython] C_element100  label="C_element : 0.856"  # scripted group (container) (typed FeaturePython)
  n = 0.856289
FEATURE [App::DocumentObjectGroupPython] G4_RUBBER_BUTYL  # scripted group (container) (typed FeaturePython)
  Dunit = g/cm3
  Dvalue = 0.92
  Group = -> [H_element092,C_element100]
  conduct = 2
  density = 1
  expand = 3
  formula = G4_RUBBER_BUTYL
  name = G4_RUBBER_BUTYL
  specific = 4
FEATURE [App::DocumentObjectGroupPython] H_element093  label="H_element : 0.118"  # scripted group (container) (typed FeaturePython)
  n = 0.118371
FEATURE [App::DocumentObjectGroupPython] C_element101  label="C_element : 0.882"  # scripted group (container) (typed FeaturePython)
  n = 0.881629
FEATURE [App::DocumentObjectGroupPython] G4_RUBBER_NATURAL  # scripted group (container) (typed FeaturePython)
  Dunit = g/cm3
  Dvalue = 0.92
  Group = -> [H_element093,C_element101]
  conduct = 2
  density = 1
  expand = 3
  formula = G4_RUBBER_NATURAL
  name = G4_RUBBER_NATURAL
  specific = 4
FEATURE [App::DocumentObjectGroupPython] H_element094  label="H_element : 0.145"  # scripted group (container) (typed FeaturePython)
  n = 0.05692
FEATURE [App::DocumentObjectGroupPython] C_element102  label="C_element : 0.543"  # scripted group (container) (typed FeaturePython)
  n = 0.542646
FEATURE [App::DocumentObjectGroupPython] Cl_element021  label="Cl_element : 0.400"  # scripted group (container) (typed FeaturePython)
  n = 0.400434
FEATURE [App::DocumentObjectGroupPython] G4_RUBBER_NEOPRENE  # scripted group (container) (typed FeaturePython)
  Dunit = g/cm3
  Dvalue = 1.23
  Group = -> [H_element094,C_element102,Cl_element021]
  conduct = 2
  density = 1
  expand = 3
  formula = G4_RUBBER_NEOPRENE
  name = G4_RUBBER_NEOPRENE
  specific = 4
FEATURE [App::DocumentObjectGroupPython] Si_element006  label="Si_element : 1"  # scripted group (container) (typed FeaturePython)
  n = 1
  ref = Si_element
FEATURE [App::DocumentObjectGroupPython] O_element087  label="O_element : 048"  # scripted group (container) (typed FeaturePython)
  n = 2
  ref = O_element
FEATURE [App::DocumentObjectGroupPython] G4_SILICON_DIOXIDE  # scripted group (container) (typed FeaturePython)
  Dunit = g/cm3
  Dvalue = 2.32
  Group = -> [Si_element006,O_element087]
  conduct = 2
  density = 1
  expand = 3
  formula = G4_SILICON_DIOXIDE
  name = G4_SILICON_DIOXIDE
  specific = 4
FEATURE [App::DocumentObjectGroupPython] Ag_element002  label="Ag_element : 1"  # scripted group (container) (typed FeaturePython)
  n = 1
  ref = Ag_element
FEATURE [App::DocumentObjectGroupPython] Br_element005  label="Br_element : 003"  # scripted group (container) (typed FeaturePython)
  n = 1
  ref = Br_element
FEATURE [App::DocumentObjectGroupPython] G4_SILVER_BROMIDE  # scripted group (container) (typed FeaturePython)
  Dunit = g/cm3
  Dvalue = 6.473
  Group = -> [Ag_element002,Br_element005]
  conduct = 2
  density = 1
  expand = 3
  formula = G4_SILVER_BROMIDE
  name = G4_SILVER_BROMIDE
  specific = 4
FEATURE [App::DocumentObjectGroupPython] Ag_element003  label="Ag_element : 002"  # scripted group (container) (typed FeaturePython)
  n = 1
  ref = Ag_element
FEATURE [App::DocumentObjectGroupPython] Cl_element022  label="Cl_element : 011"  # scripted group (container) (typed FeaturePython)
  n = 1
  ref = Cl_element
FEATURE [App::DocumentObjectGroupPython] G4_SILVER_CHLORIDE  # scripted group (container) (typed FeaturePython)
  Dunit = g/cm3
  Dvalue = 5.56
  Group = -> [Ag_element003,Cl_element022]
  conduct = 2
  density = 1
  expand = 3
  formula = G4_SILVER_CHLORIDE
  name = G4_SILVER_CHLORIDE
  specific = 4
FEATURE [App::DocumentObjectGroupPython] Br_element006  label="Br_element : 0.423"  # scripted group (container) (typed FeaturePython)
  n = 0.422895
FEATURE [App::DocumentObjectGroupPython] Ag_element004  label="Ag_element : 0.574"  # scripted group (container) (typed FeaturePython)
  n = 0.573748
FEATURE [App::DocumentObjectGroupPython] I_element007  label="I_element : 0.649"  # scripted group (container) (typed FeaturePython)
  n = 0.003357
FEATURE [App::DocumentObjectGroupPython] G4_SILVER_HALIDES  # scripted group (container) (typed FeaturePython)
  Dunit = g/cm3
  Dvalue = 6.47
  Group = -> [Br_element006,Ag_element004,I_element007]
  conduct = 2
  density = 1
  expand = 3
  formula = G4_SILVER_HALIDES
  name = G4_SILVER_HALIDES
  specific = 4
FEATURE [App::DocumentObjectGroupPython] Ag_element005  label="Ag_element : 003"  # scripted group (container) (typed FeaturePython)
  n = 1
  ref = Ag_element
FEATURE [App::DocumentObjectGroupPython] I_element008  label="I_element : 004"  # scripted group (container) (typed FeaturePython)
  n = 1
  ref = I_element
FEATURE [App::DocumentObjectGroupPython] G4_SILVER_IODIDE  # scripted group (container) (typed FeaturePython)
  Dunit = g/cm3
  Dvalue = 6.01
  Group = -> [Ag_element005,I_element008]
  conduct = 2
  density = 1
  expand = 3
  formula = G4_SILVER_IODIDE
  name = G4_SILVER_IODIDE
  specific = 4
FEATURE [App::DocumentObjectGroupPython] H_element095  label="H_element : 0.100"  # scripted group (container) (typed FeaturePython)
  n = 0.1
FEATURE [App::DocumentObjectGroupPython] C_element103  label="C_element : 0.204"  # scripted group (container) (typed FeaturePython)
  n = 0.204
FEATURE [App::DocumentObjectGroupPython] N_element039  label="N_element : 0.759"  # scripted group (container) (typed FeaturePython)
  n = 0.042
FEATURE [App::DocumentObjectGroupPython] O_element088  label="O_element : 0.645"  # scripted group (container) (typed FeaturePython)
  n = 0.645
FEATURE [App::DocumentObjectGroupPython] Na_element013  label="Na_element : 0.100"  # scripted group (container) (typed FeaturePython)
  n = 0.002
FEATURE [App::DocumentObjectGroupPython] P_element009  label="P_element : 0.107"  # scripted group (container) (typed FeaturePython)
  n = 0.001
FEATURE [App::DocumentObjectGroupPython] S_element020  label="S_element : 0.021"  # scripted group (container) (typed FeaturePython)
  n = 0.002
FEATURE [App::DocumentObjectGroupPython] Cl_element023  label="Cl_element : 0.590"  # scripted group (container) (typed FeaturePython)
  n = 0.003
FEATURE [App::DocumentObjectGroupPython] K_element010  label="K_element : 0.001"  # scripted group (container) (typed FeaturePython)
  n = 0.001
FEATURE [App::DocumentObjectGroupPython] G4_SKIN_ICRP  # scripted group (container) (typed FeaturePython)
  Dunit = g/cm3
  Dvalue = 1.09
  Group = -> [H_element095,C_element103,N_element039,O_element088,Na_element013,P_element009,S_element020,Cl_element023,K_element010]
  conduct = 2
  density = 1
  expand = 3
  formula = G4_SKIN_ICRP
  name = G4_SKIN_ICRP
  specific = 4
FEATURE [App::DocumentObjectGroupPython] Na_element014  label="Na_element : 2"  # scripted group (container) (typed FeaturePython)
  n = 2
  ref = Na_element
FEATURE [App::DocumentObjectGroupPython] C_element104  label="C_element : 058"  # scripted group (container) (typed FeaturePython)
  n = 1
  ref = C_element
FEATURE [App::DocumentObjectGroupPython] O_element089  label="O_element : 049"  # scripted group (container) (typed FeaturePython)
  n = 3
  ref = O_element
FEATURE [App::DocumentObjectGroupPython] G4_SODIUM_CARBONATE  # scripted group (container) (typed FeaturePython)
  Dunit = g/cm3
  Dvalue = 2.532
  Group = -> [Na_element014,C_element104,O_element089]
  conduct = 2
  density = 1
  expand = 3
  formula = G4_SODIUM_CARBONATE
  name = G4_SODIUM_CARBONATE
  specific = 4
FEATURE [App::DocumentObjectGroupPython] Na_element015  label="Na_element : 1"  # scripted group (container) (typed FeaturePython)
  n = 1
  ref = Na_element
FEATURE [App::DocumentObjectGroupPython] I_element009  label="I_element : 005"  # scripted group (container) (typed FeaturePython)
  n = 1
  ref = I_element
FEATURE [App::DocumentObjectGroupPython] G4_SODIUM_IODIDE  # scripted group (container) (typed FeaturePython)
  Dunit = g/cm3
  Dvalue = 3.667
  Group = -> [Na_element015,I_element009]
  conduct = 2
  density = 1
  expand = 3
  formula = G4_SODIUM_IODIDE
  name = G4_SODIUM_IODIDE
  specific = 4
FEATURE [App::DocumentObjectGroupPython] Na_element016  label="Na_element : 003"  # scripted group (container) (typed FeaturePython)
  n = 2
  ref = Na_element
FEATURE [App::DocumentObjectGroupPython] O_element090  label="O_element : 050"  # scripted group (container) (typed FeaturePython)
  n = 1
  ref = O_element
FEATURE [App::DocumentObjectGroupPython] G4_SODIUM_MONOXIDE  # scripted group (container) (typed FeaturePython)
  Dunit = g/cm3
  Dvalue = 2.27
  Group = -> [Na_element016,O_element090]
  conduct = 2
  density = 1
  expand = 3
  formula = G4_SODIUM_MONOXIDE
  name = G4_SODIUM_MONOXIDE
  specific = 4
FEATURE [App::DocumentObjectGroupPython] Na_element017  label="Na_element : 004"  # scripted group (container) (typed FeaturePython)
  n = 1
  ref = Na_element
FEATURE [App::DocumentObjectGroupPython] N_element040  label="N_element : 018"  # scripted group (container) (typed FeaturePython)
  n = 1
  ref = N_element
FEATURE [App::DocumentObjectGroupPython] O_element091  label="O_element : 051"  # scripted group (container) (typed FeaturePython)
  n = 3
  ref = O_element
FEATURE [App::DocumentObjectGroupPython] G4_SODIUM_NITRATE  # scripted group (container) (typed FeaturePython)
  Dunit = g/cm3
  Dvalue = 2.261
  Group = -> [Na_element017,N_element040,O_element091]
  conduct = 2
  density = 1
  expand = 3
  formula = G4_SODIUM_NITRATE
  name = G4_SODIUM_NITRATE
  specific = 4
FEATURE [App::DocumentObjectGroupPython] C_element105  label="C_element : 059"  # scripted group (container) (typed FeaturePython)
  n = 14
  ref = C_element
FEATURE [App::DocumentObjectGroupPython] H_element096  label="H_element : 053"  # scripted group (container) (typed FeaturePython)
  n = 12
  ref = H_element
FEATURE [App::DocumentObjectGroupPython] G4_STILBENE  # scripted group (container) (typed FeaturePython)
  Dunit = g/cm3
  Dvalue = 0.9707
  Group = -> [C_element105,H_element096]
  conduct = 2
  density = 1
  expand = 3
  formula = G4_STILBENE
  name = G4_STILBENE
  specific = 4
FEATURE [App::DocumentObjectGroupPython] C_element106  label="C_element : 12"  # scripted group (container) (typed FeaturePython)
  n = 12
  ref = C_element
FEATURE [App::DocumentObjectGroupPython] H_element097  label="H_element : 22"  # scripted group (container) (typed FeaturePython)
  n = 22
  ref = H_element
FEATURE [App::DocumentObjectGroupPython] O_element092  label="O_element : 11"  # scripted group (container) (typed FeaturePython)
  n = 11
  ref = O_element
FEATURE [App::DocumentObjectGroupPython] G4_SUCROSE  # scripted group (container) (typed FeaturePython)
  Dunit = g/cm3
  Dvalue = 1.5805
  Group = -> [C_element106,H_element097,O_element092]
  conduct = 2
  density = 1
  expand = 3
  formula = G4_SUCROSE
  name = G4_SUCROSE
  specific = 4
FEATURE [App::DocumentObjectGroupPython] C_element107  label="C_element : 18"  # scripted group (container) (typed FeaturePython)
  n = 18
  ref = C_element
FEATURE [App::DocumentObjectGroupPython] H_element098  label="H_element : 054"  # scripted group (container) (typed FeaturePython)
  n = 14
  ref = H_element
FEATURE [App::DocumentObjectGroupPython] G4_TERPHENYL  # scripted group (container) (typed FeaturePython)
  Dunit = g/cm3
  Dvalue = 1.24
  Group = -> [C_element107,H_element098]
  conduct = 2
  density = 1
  expand = 3
  formula = G4_TERPHENYL
  name = G4_TERPHENYL
  specific = 4
FEATURE [App::DocumentObjectGroupPython] H_element099  label="H_element : 0.146"  # scripted group (container) (typed FeaturePython)
  n = 0.106
FEATURE [App::DocumentObjectGroupPython] C_element108  label="C_element : 0.883"  # scripted group (container) (typed FeaturePython)
  n = 0.099
FEATURE [App::DocumentObjectGroupPython] N_element041  label="N_element : 0.020"  # scripted group (container) (typed FeaturePython)
  n = 0.02
FEATURE [App::DocumentObjectGroupPython] O_element093  label="O_element : 0.766"  # scripted group (container) (typed FeaturePython)
  n = 0.766
FEATURE [App::DocumentObjectGroupPython] Na_element018  label="Na_element : 0.101"  # scripted group (container) (typed FeaturePython)
  n = 0.002
FEATURE [App::DocumentObjectGroupPython] P_element010  label="P_element : 0.108"  # scripted group (container) (typed FeaturePython)
  n = 0.001
FEATURE [App::DocumentObjectGroupPython] S_element021  label="S_element : 0.022"  # scripted group (container) (typed FeaturePython)
  n = 0.002
FEATURE [App::DocumentObjectGroupPython] Cl_element024  label="Cl_element : 0.002"  # scripted group (container) (typed FeaturePython)
  n = 0.002
FEATURE [App::DocumentObjectGroupPython] K_element011  label="K_element : 0.017"  # scripted group (container) (typed FeaturePython)
  n = 0.002
FEATURE [App::DocumentObjectGroupPython] G4_TESTIS_ICRP  # scripted group (container) (typed FeaturePython)
  Dunit = g/cm3
  Dvalue = 1.04
  Group = -> [H_element099,C_element108,N_element041,O_element093,Na_element018,P_element010,S_element021,Cl_element024,K_element011]
  conduct = 2
  density = 1
  expand = 3
  formula = G4_TESTIS_ICRP
  name = G4_TESTIS_ICRP
  specific = 4
FEATURE [App::DocumentObjectGroupPython] C_element109  label="C_element : 060"  # scripted group (container) (typed FeaturePython)
  n = 2
  ref = C_element
FEATURE [App::DocumentObjectGroupPython] Cl_element025  label="Cl_element : 012"  # scripted group (container) (typed FeaturePython)
  n = 4
  ref = Cl_element
FEATURE [App::DocumentObjectGroupPython] G4_TETRACHLOROETHYLENE  # scripted group (container) (typed FeaturePython)
  Dunit = g/cm3
  Dvalue = 1.625
  Group = -> [C_element109,Cl_element025]
  conduct = 2
  density = 1
  expand = 3
  formula = G4_TETRACHLOROETHYLENE
  name = G4_TETRACHLOROETHYLENE
  specific = 4
FEATURE [App::DocumentObjectGroupPython] Tl_element001  label="Tl_element : 1"  # scripted group (container) (typed FeaturePython)
  n = 1
  ref = Tl_element
FEATURE [App::DocumentObjectGroupPython] Cl_element026  label="Cl_element : 013"  # scripted group (container) (typed FeaturePython)
  n = 1
  ref = Cl_element
FEATURE [App::DocumentObjectGroupPython] G4_THALLIUM_CHLORIDE  # scripted group (container) (typed FeaturePython)
  Dunit = g/cm3
  Dvalue = 7.004
  Group = -> [Tl_element001,Cl_element026]
  conduct = 2
  density = 1
  expand = 3
  formula = G4_THALLIUM_CHLORIDE
  name = G4_THALLIUM_CHLORIDE
  specific = 4
FEATURE [App::DocumentObjectGroupPython] H_element100  label="H_element : 0.147"  # scripted group (container) (typed FeaturePython)
  n = 0.105
FEATURE [App::DocumentObjectGroupPython] C_element110  label="C_element : 0.256"  # scripted group (container) (typed FeaturePython)
  n = 0.256
FEATURE [App::DocumentObjectGroupPython] N_element042  label="N_element : 0.760"  # scripted group (container) (typed FeaturePython)
  n = 0.027
FEATURE [App::DocumentObjectGroupPython] O_element094  label="O_element : 0.602"  # scripted group (container) (typed FeaturePython)
  n = 0.602
FEATURE [App::DocumentObjectGroupPython] Na_element019  label="Na_element : 0.102"  # scripted group (container) (typed FeaturePython)
  n = 0.001
FEATURE [App::DocumentObjectGroupPython] P_element011  label="P_element : 0.109"  # scripted group (container) (typed FeaturePython)
  n = 0.002
FEATURE [App::DocumentObjectGroupPython] S_element022  label="S_element : 0.023"  # scripted group (container) (typed FeaturePython)
  n = 0.003
FEATURE [App::DocumentObjectGroupPython] Cl_element027  label="Cl_element : 0.591"  # scripted group (container) (typed FeaturePython)
  n = 0.002
FEATURE [App::DocumentObjectGroupPython] K_element012  label="K_element : 0.018"  # scripted group (container) (typed FeaturePython)
  n = 0.002
FEATURE [App::DocumentObjectGroupPython] G4_TISSUE_SOFT_ICRP  # scripted group (container) (typed FeaturePython)
  Dunit = g/cm3
  Dvalue = 1.03
  Group = -> [H_element100,C_element110,N_element042,O_element094,Na_element019,P_element011,S_element022,Cl_element027,K_element012]
  conduct = 2
  density = 1
  expand = 3
  formula = G4_TISSUE_SOFT_ICRP
  name = G4_TISSUE_SOFT_ICRP
  specific = 4
FEATURE [App::DocumentObjectGroupPython] H_element101  label="H_element : 0.148"  # scripted group (container) (typed FeaturePython)
  n = 0.101
FEATURE [App::DocumentObjectGroupPython] C_element111  label="C_element : 0.111"  # scripted group (container) (typed FeaturePython)
  n = 0.111
FEATURE [App::DocumentObjectGroupPython] N_element043  label="N_element : 0.026"  # scripted group (container) (typed FeaturePython)
  n = 0.026
FEATURE [App::DocumentObjectGroupPython] O_element095  label="O_element : 0.762"  # scripted group (container) (typed FeaturePython)
  n = 0.762
FEATURE [App::DocumentObjectGroupPython] G4_TISSUE_SOFT_ICRU_4  label="G4_TISSUE_SOFT_ICRU-4"  # scripted group (container) (typed FeaturePython)
  Dunit = g/cm3
  Dvalue = 1
  Group = -> [H_element101,C_element111,N_element043,O_element095]
  conduct = 2
  density = 1
  expand = 3
  formula = G4_TISSUE_SOFT_ICRU-4
  name = G4_TISSUE_SOFT_ICRU-4
  specific = 4
FEATURE [App::DocumentObjectGroupPython] H_element102  label="H_element : 0.149"  # scripted group (container) (typed FeaturePython)
  n = 0.101869
FEATURE [App::DocumentObjectGroupPython] C_element112  label="C_element : 0.456"  # scripted group (container) (typed FeaturePython)
  n = 0.456179
FEATURE [App::DocumentObjectGroupPython] N_element044  label="N_element : 0.761"  # scripted group (container) (typed FeaturePython)
  n = 0.035172
FEATURE [App::DocumentObjectGroupPython] O_element096  label="O_element : 0.407"  # scripted group (container) (typed FeaturePython)
  n = 0.40678
FEATURE [App::DocumentObjectGroupPython] G4_TISSUE_METHANE  label="G4_TISSUE-METHANE"  # scripted group (container) (typed FeaturePython)
  Dunit = g/cm3
  Dvalue = 0.00106409
  Group = -> [H_element102,C_element112,N_element044,O_element096]
  conduct = 2
  density = 1
  expand = 3
  formula = G4_TISSUE-METHANE
  name = G4_TISSUE-METHANE
  specific = 4
FEATURE [App::DocumentObjectGroupPython] H_element103  label="H_element : 0.103"  # scripted group (container) (typed FeaturePython)
  n = 0.102672
FEATURE [App::DocumentObjectGroupPython] C_element113  label="C_element : 0.569"  # scripted group (container) (typed FeaturePython)
  n = 0.56894
FEATURE [App::DocumentObjectGroupPython] N_element045  label="N_element : 0.762"  # scripted group (container) (typed FeaturePython)
  n = 0.035022
FEATURE [App::DocumentObjectGroupPython] O_element097  label="O_element : 0.293"  # scripted group (container) (typed FeaturePython)
  n = 0.293366
FEATURE [App::DocumentObjectGroupPython] G4_TISSUE_PROPANE  label="G4_TISSUE-PROPANE"  # scripted group (container) (typed FeaturePython)
  Dunit = g/cm3
  Dvalue = 0.00182628
  Group = -> [H_element103,C_element113,N_element045,O_element097]
  conduct = 2
  density = 1
  expand = 3
  formula = G4_TISSUE-PROPANE
  name = G4_TISSUE-PROPANE
  specific = 4
FEATURE [App::DocumentObjectGroupPython] Ti_element003  label="Ti_element : 1"  # scripted group (container) (typed FeaturePython)
  n = 1
  ref = Ti_element
FEATURE [App::DocumentObjectGroupPython] O_element098  label="O_element : 052"  # scripted group (container) (typed FeaturePython)
  n = 2
  ref = O_element
FEATURE [App::DocumentObjectGroupPython] G4_TITANIUM_DIOXIDE  # scripted group (container) (typed FeaturePython)
  Dunit = g/cm3
  Dvalue = 4.26
  Group = -> [Ti_element003,O_element098]
  conduct = 2
  density = 1
  expand = 3
  formula = G4_TITANIUM_DIOXIDE
  name = G4_TITANIUM_DIOXIDE
  specific = 4
FEATURE [App::DocumentObjectGroupPython] C_element114  label="C_element : 061"  # scripted group (container) (typed FeaturePython)
  n = 7
  ref = C_element
FEATURE [App::DocumentObjectGroupPython] H_element104  label="H_element : 055"  # scripted group (container) (typed FeaturePython)
  n = 8
  ref = H_element
FEATURE [App::DocumentObjectGroupPython] G4_TOLUENE  # scripted group (container) (typed FeaturePython)
  Dunit = g/cm3
  Dvalue = 0.8669
  Group = -> [C_element114,H_element104]
  conduct = 2
  density = 1
  expand = 3
  formula = G4_TOLUENE
  name = G4_TOLUENE
  specific = 4
FEATURE [App::DocumentObjectGroupPython] C_element115  label="C_element : 062"  # scripted group (container) (typed FeaturePython)
  n = 2
  ref = C_element
FEATURE [App::DocumentObjectGroupPython] H_element105  label="H_element : 056"  # scripted group (container) (typed FeaturePython)
  n = 1
  ref = H_element
FEATURE [App::DocumentObjectGroupPython] Cl_element028  label="Cl_element : 014"  # scripted group (container) (typed FeaturePython)
  n = 3
  ref = Cl_element
FEATURE [App::DocumentObjectGroupPython] G4_TRICHLOROETHYLENE  # scripted group (container) (typed FeaturePython)
  Dunit = g/cm3
  Dvalue = 1.46
  Group = -> [C_element115,H_element105,Cl_element028]
  conduct = 2
  density = 1
  expand = 3
  formula = G4_TRICHLOROETHYLENE
  name = G4_TRICHLOROETHYLENE
  specific = 4
FEATURE [App::DocumentObjectGroupPython] C_element116  label="C_element : 063"  # scripted group (container) (typed FeaturePython)
  n = 6
  ref = C_element
FEATURE [App::DocumentObjectGroupPython] H_element106  label="H_element : 15"  # scripted group (container) (typed FeaturePython)
  n = 15
  ref = H_element
FEATURE [App::DocumentObjectGroupPython] O_element099  label="O_element : 053"  # scripted group (container) (typed FeaturePython)
  n = 4
  ref = O_element
FEATURE [App::DocumentObjectGroupPython] P_element012  label="P_element : 1"  # scripted group (container) (typed FeaturePython)
  n = 1
  ref = P_element
FEATURE [App::DocumentObjectGroupPython] G4_TRIETHYL_PHOSPHATE  # scripted group (container) (typed FeaturePython)
  Dunit = g/cm3
  Dvalue = 1.07
  Group = -> [C_element116,H_element106,O_element099,P_element012]
  conduct = 2
  density = 1
  expand = 3
  formula = G4_TRIETHYL_PHOSPHATE
  name = G4_TRIETHYL_PHOSPHATE
  specific = 4
FEATURE [App::DocumentObjectGroupPython] W_element003  label="W_element : 003"  # scripted group (container) (typed FeaturePython)
  n = 1
  ref = W_element
FEATURE [App::DocumentObjectGroupPython] F_element017  label="F_element : 6"  # scripted group (container) (typed FeaturePython)
  n = 6
  ref = F_element
FEATURE [App::DocumentObjectGroupPython] G4_TUNGSTEN_HEXAFLUORIDE  # scripted group (container) (typed FeaturePython)
  Dunit = g/cm3
  Dvalue = 2.4
  Group = -> [W_element003,F_element017]
  conduct = 2
  density = 1
  expand = 3
  formula = G4_TUNGSTEN_HEXAFLUORIDE
  name = G4_TUNGSTEN_HEXAFLUORIDE
  specific = 4
FEATURE [App::DocumentObjectGroupPython] U_element001  label="U_element : 1"  # scripted group (container) (typed FeaturePython)
  n = 1
  ref = U_element
FEATURE [App::DocumentObjectGroupPython] C_element117  label="C_element : 064"  # scripted group (container) (typed FeaturePython)
  n = 2
  ref = C_element
FEATURE [App::DocumentObjectGroupPython] G4_URANIUM_DICARBIDE  # scripted group (container) (typed FeaturePython)
  Dunit = g/cm3
  Dvalue = 11.28
  Group = -> [U_element001,C_element117]
  conduct = 2
  density = 1
  expand = 3
  formula = G4_URANIUM_DICARBIDE
  name = G4_URANIUM_DICARBIDE
  specific = 4
FEATURE [App::DocumentObjectGroupPython] U_element002  label="U_element : 002"  # scripted group (container) (typed FeaturePython)
  n = 1
  ref = U_element
FEATURE [App::DocumentObjectGroupPython] C_element118  label="C_element : 065"  # scripted group (container) (typed FeaturePython)
  n = 1
  ref = C_element
FEATURE [App::DocumentObjectGroupPython] G4_URANIUM_MONOCARBIDE  # scripted group (container) (typed FeaturePython)
  Dunit = g/cm3
  Dvalue = 13.63
  Group = -> [U_element002,C_element118]
  conduct = 2
  density = 1
  expand = 3
  formula = G4_URANIUM_MONOCARBIDE
  name = G4_URANIUM_MONOCARBIDE
  specific = 4
FEATURE [App::DocumentObjectGroupPython] U_element003  label="U_element : 003"  # scripted group (container) (typed FeaturePython)
  n = 1
  ref = U_element
FEATURE [App::DocumentObjectGroupPython] O_element100  label="O_element : 054"  # scripted group (container) (typed FeaturePython)
  n = 2
  ref = O_element
FEATURE [App::DocumentObjectGroupPython] G4_URANIUM_OXIDE  # scripted group (container) (typed FeaturePython)
  Dunit = g/cm3
  Dvalue = 10.96
  Group = -> [U_element003,O_element100]
  conduct = 2
  density = 1
  expand = 3
  formula = G4_URANIUM_OXIDE
  name = G4_URANIUM_OXIDE
  specific = 4
FEATURE [App::DocumentObjectGroupPython] C_element119  label="C_element : 066"  # scripted group (container) (typed FeaturePython)
  n = 1
  ref = C_element
FEATURE [App::DocumentObjectGroupPython] H_element107  label="H_element : 057"  # scripted group (container) (typed FeaturePython)
  n = 4
  ref = H_element
FEATURE [App::DocumentObjectGroupPython] N_element046  label="N_element : 019"  # scripted group (container) (typed FeaturePython)
  n = 2
  ref = N_element
FEATURE [App::DocumentObjectGroupPython] O_element101  label="O_element : 055"  # scripted group (container) (typed FeaturePython)
  n = 1
  ref = O_element
FEATURE [App::DocumentObjectGroupPython] G4_UREA  # scripted group (container) (typed FeaturePython)
  Dunit = g/cm3
  Dvalue = 1.323
  Group = -> [C_element119,H_element107,N_element046,O_element101]
  conduct = 2
  density = 1
  expand = 3
  formula = G4_UREA
  name = G4_UREA
  specific = 4
FEATURE [App::DocumentObjectGroupPython] C_element120  label="C_element : 067"  # scripted group (container) (typed FeaturePython)
  n = 5
  ref = C_element
FEATURE [App::DocumentObjectGroupPython] H_element108  label="H_element : 058"  # scripted group (container) (typed FeaturePython)
  n = 11
  ref = H_element
FEATURE [App::DocumentObjectGroupPython] N_element047  label="N_element : 020"  # scripted group (container) (typed FeaturePython)
  n = 1
  ref = N_element
FEATURE [App::DocumentObjectGroupPython] O_element102  label="O_element : 056"  # scripted group (container) (typed FeaturePython)
  n = 2
  ref = O_element
FEATURE [App::DocumentObjectGroupPython] G4_VALINE  # scripted group (container) (typed FeaturePython)
  Dunit = g/cm3
  Dvalue = 1.23
  Group = -> [C_element120,H_element108,N_element047,O_element102]
  conduct = 2
  density = 1
  expand = 3
  formula = G4_VALINE
  name = G4_VALINE
  specific = 4
FEATURE [App::DocumentObjectGroupPython] H_element109  label="H_element : 0.009"  # scripted group (container) (typed FeaturePython)
  n = 0.009417
FEATURE [App::DocumentObjectGroupPython] C_element121  label="C_element : 0.281"  # scripted group (container) (typed FeaturePython)
  n = 0.280555
FEATURE [App::DocumentObjectGroupPython] F_element018  label="F_element : 0.710"  # scripted group (container) (typed FeaturePython)
  n = 0.710028
FEATURE [App::DocumentObjectGroupPython] G4_VITON  # scripted group (container) (typed FeaturePython)
  Dunit = g/cm3
  Dvalue = 1.8
  Group = -> [H_element109,C_element121,F_element018]
  conduct = 2
  density = 1
  expand = 3
  formula = G4_VITON
  name = G4_VITON
  specific = 4
FEATURE [App::DocumentObjectGroupPython] H_element110  label="H_element : 059"  # scripted group (container) (typed FeaturePython)
  n = 2
  ref = H_element
FEATURE [App::DocumentObjectGroupPython] O_element103  label="O_element : 057"  # scripted group (container) (typed FeaturePython)
  n = 1
  ref = O_element
FEATURE [App::DocumentObjectGroupPython] G4_WATER  # scripted group (container) (typed FeaturePython)
  Dunit = g/cm3
  Dvalue = 1
  Group = -> [H_element110,O_element103]
  conduct = 2
  density = 1
  expand = 3
  formula = G4_WATER
  name = G4_WATER
  specific = 4
FEATURE [App::DocumentObjectGroupPython] H_element111  label="H_element : 060"  # scripted group (container) (typed FeaturePython)
  n = 2
  ref = H_element
FEATURE [App::DocumentObjectGroupPython] O_element104  label="O_element : 058"  # scripted group (container) (typed FeaturePython)
  n = 1
  ref = O_element
FEATURE [App::DocumentObjectGroupPython] G4_WATER_VAPOR  # scripted group (container) (typed FeaturePython)
  Dunit = g/cm3
  Dvalue = 0.000756182
  Group = -> [H_element111,O_element104]
  conduct = 2
  density = 1
  expand = 3
  formula = G4_WATER_VAPOR
  name = G4_WATER_VAPOR
  specific = 4
FEATURE [App::DocumentObjectGroupPython] C_element122  label="C_element : 068"  # scripted group (container) (typed FeaturePython)
  n = 8
  ref = C_element
FEATURE [App::DocumentObjectGroupPython] H_element112  label="H_element : 061"  # scripted group (container) (typed FeaturePython)
  n = 10
  ref = H_element
FEATURE [App::DocumentObjectGroupPython] G4_XYLENE  # scripted group (container) (typed FeaturePython)
  Dunit = g/cm3
  Dvalue = 0.87
  Group = -> [C_element122,H_element112]
  conduct = 2
  density = 1
  expand = 3
  formula = G4_XYLENE
  name = G4_XYLENE
  specific = 4
FEATURE [App::DocumentObjectGroupPython] C_element123  label="C_element : 069"  # scripted group (container) (typed FeaturePython)
  n = 1
  ref = C_element
FEATURE [App::DocumentObjectGroupPython] G4_GRAPHITE  # scripted group (container) (typed FeaturePython)
  Dunit = g/cm3
  Dvalue = 2.21
  Group = -> [C_element123]
  conduct = 2
  density = 1
  expand = 3
  formula = G4_GRAPHITE
  name = G4_GRAPHITE
  specific = 4
FEATURE [App::DocumentObjectGroupPython] NIST  # scripted group (container) (typed FeaturePython)
  Group = -> [G4_A_150_TISSUE,G4_ACETONE,G4_ACETYLENE,G4_ADENINE,G4_ADIPOSE_TISSUE_ICRP,G4_AIR,G4_ALANINE,G4_ALUMINUM_OXIDE,G4_AMBER,G4_AMMONIA,G4_ANILINE,G4_ANTHRACENE,G4_B_100_BONE,G4_BAKELITE,G4_BARIUM_FLUORIDE,G4_BARIUM_SULFATE,G4_BENZENE,G4_BERYLLIUM_OXIDE,G4_BGO,G4_BLOOD_ICRP,G4_BONE_COMPACT_ICRU,G4_BONE_CORTICAL_ICRP,G4_BORON_CARBIDE,G4_BORON_OXIDE,G4_BRAIN_ICRP,G4_BUTANE,G4_N_BUTYL_ALCOHOL,G4_C_552,+152 more]
FEATURE [App::DocumentObjectGroupPython] H_element113  label="H_element : 062"  # scripted group (container) (typed FeaturePython)
  n = 1
  ref = H_element
FEATURE [App::DocumentObjectGroupPython] G4_H  # scripted group (container) (typed FeaturePython)
  Dunit = g/cm3
  Dvalue = 8.3748e-05
  Group = -> [H_element113]
  conduct = 2
  density = 1
  expand = 3
  formula = H
  name = G4_H
  specific = 4
FEATURE [App::DocumentObjectGroupPython] He_element001  label="He_element : 1"  # scripted group (container) (typed FeaturePython)
  n = 1
  ref = He_element
FEATURE [App::DocumentObjectGroupPython] G4_He  # scripted group (container) (typed FeaturePython)
  Dunit = g/cm3
  Dvalue = 0.000166322
  Group = -> [He_element001]
  conduct = 2
  density = 1
  expand = 3
  formula = He
  name = G4_He
  specific = 4
FEATURE [App::DocumentObjectGroupPython] Li_element008  label="Li_element : 008"  # scripted group (container) (typed FeaturePython)
  n = 1
  ref = Li_element
FEATURE [App::DocumentObjectGroupPython] G4_Li  # scripted group (container) (typed FeaturePython)
  Dunit = g/cm3
  Dvalue = 0.534
  Group = -> [Li_element008]
  conduct = 2
  density = 1
  expand = 3
  formula = Li
  name = G4_Li
  specific = 4
FEATURE [App::DocumentObjectGroupPython] Be_element002  label="Be_element : 002"  # scripted group (container) (typed FeaturePython)
  n = 1
  ref = Be_element
FEATURE [App::DocumentObjectGroupPython] G4_Be  # scripted group (container) (typed FeaturePython)
  Dunit = g/cm3
  Dvalue = 1.848
  Group = -> [Be_element002]
  conduct = 2
  density = 1
  expand = 3
  formula = Be
  name = G4_Be
  specific = 4
FEATURE [App::DocumentObjectGroupPython] B_element007  label="B_element : 007"  # scripted group (container) (typed FeaturePython)
  n = 1
  ref = B_element
FEATURE [App::DocumentObjectGroupPython] G4_B  # scripted group (container) (typed FeaturePython)
  Dunit = g/cm3
  Dvalue = 2.37
  Group = -> [B_element007]
  conduct = 2
  density = 1
  expand = 3
  formula = B
  name = G4_B
  specific = 4
FEATURE [App::DocumentObjectGroupPython] C_element124  label="C_element : 070"  # scripted group (container) (typed FeaturePython)
  n = 1
  ref = C_element
FEATURE [App::DocumentObjectGroupPython] G4_C  # scripted group (container) (typed FeaturePython)
  Dunit = g/cm3
  Dvalue = 2
  Group = -> [C_element124]
  conduct = 2
  density = 1
  expand = 3
  formula = C
  name = G4_C
  specific = 4
FEATURE [App::DocumentObjectGroupPython] N_element048  label="N_element : 021"  # scripted group (container) (typed FeaturePython)
  n = 1
  ref = N_element
FEATURE [App::DocumentObjectGroupPython] G4_N  # scripted group (container) (typed FeaturePython)
  Dunit = g/cm3
  Dvalue = 0.0011652
  Group = -> [N_element048]
  conduct = 2
  density = 1
  expand = 3
  formula = N
  name = G4_N
  specific = 4
FEATURE [App::DocumentObjectGroupPython] O_element105  label="O_element : 059"  # scripted group (container) (typed FeaturePython)
  n = 1
  ref = O_element
FEATURE [App::DocumentObjectGroupPython] G4_O  # scripted group (container) (typed FeaturePython)
  Dunit = g/cm3
  Dvalue = 0.00133151
  Group = -> [O_element105]
  conduct = 2
  density = 1
  expand = 3
  formula = O
  name = G4_O
  specific = 4
FEATURE [App::DocumentObjectGroupPython] F_element019  label="F_element : 008"  # scripted group (container) (typed FeaturePython)
  n = 1
  ref = F_element
FEATURE [App::DocumentObjectGroupPython] G4_F  # scripted group (container) (typed FeaturePython)
  Dunit = g/cm3
  Dvalue = 0.00158029
  Group = -> [F_element019]
  conduct = 2
  density = 1
  expand = 3
  formula = F
  name = G4_F
  specific = 4
FEATURE [App::DocumentObjectGroupPython] Ne_element001  label="Ne_element : 1"  # scripted group (container) (typed FeaturePython)
  n = 1
  ref = Ne_element
FEATURE [App::DocumentObjectGroupPython] G4_Ne  # scripted group (container) (typed FeaturePython)
  Dunit = g/cm3
  Dvalue = 0.000838505
  Group = -> [Ne_element001]
  conduct = 2
  density = 1
  expand = 3
  formula = Ne
  name = G4_Ne
  specific = 4
FEATURE [App::DocumentObjectGroupPython] Na_element020  label="Na_element : 005"  # scripted group (container) (typed FeaturePython)
  n = 1
  ref = Na_element
FEATURE [App::DocumentObjectGroupPython] G4_Na  # scripted group (container) (typed FeaturePython)
  Dunit = g/cm3
  Dvalue = 0.971
  Group = -> [Na_element020]
  conduct = 2
  density = 1
  expand = 3
  formula = Na
  name = G4_Na
  specific = 4
FEATURE [App::DocumentObjectGroupPython] Mg_element011  label="Mg_element : 005"  # scripted group (container) (typed FeaturePython)
  n = 1
  ref = Mg_element
FEATURE [App::DocumentObjectGroupPython] G4_Mg  # scripted group (container) (typed FeaturePython)
  Dunit = g/cm3
  Dvalue = 1.74
  Group = -> [Mg_element011]
  conduct = 2
  density = 1
  expand = 3
  formula = Mg
  name = G4_Mg
  specific = 4
FEATURE [App::DocumentObjectGroupPython] Al_element004  label="Al_element : 1"  # scripted group (container) (typed FeaturePython)
  n = 1
  ref = Al_element
FEATURE [App::DocumentObjectGroupPython] G4_Al  # scripted group (container) (typed FeaturePython)
  Dunit = g/cm3
  Dvalue = 2.699
  Group = -> [Al_element004]
  conduct = 2
  density = 1
  expand = 3
  formula = Al
  name = G4_Al
  specific = 4
FEATURE [App::DocumentObjectGroupPython] Si_element007  label="Si_element : 002"  # scripted group (container) (typed FeaturePython)
  n = 1
  ref = Si_element
FEATURE [App::DocumentObjectGroupPython] G4_Si  # scripted group (container) (typed FeaturePython)
  Dunit = g/cm3
  Dvalue = 2.33
  Group = -> [Si_element007]
  conduct = 2
  density = 1
  expand = 3
  formula = Si
  name = G4_Si
  specific = 4
FEATURE [App::DocumentObjectGroupPython] P_element013  label="P_element : 002"  # scripted group (container) (typed FeaturePython)
  n = 1
  ref = P_element
FEATURE [App::DocumentObjectGroupPython] G4_P  # scripted group (container) (typed FeaturePython)
  Dunit = g/cm3
  Dvalue = 2.2
  Group = -> [P_element013]
  conduct = 2
  density = 1
  expand = 3
  formula = P
  name = G4_P
  specific = 4
FEATURE [App::DocumentObjectGroupPython] S_element023  label="S_element : 007"  # scripted group (container) (typed FeaturePython)
  n = 1
  ref = S_element
FEATURE [App::DocumentObjectGroupPython] G4_S  # scripted group (container) (typed FeaturePython)
  Dunit = g/cm3
  Dvalue = 2
  Group = -> [S_element023]
  conduct = 2
  density = 1
  expand = 3
  formula = S
  name = G4_S
  specific = 4
FEATURE [App::DocumentObjectGroupPython] Cl_element029  label="Cl_element : 015"  # scripted group (container) (typed FeaturePython)
  n = 1
  ref = Cl_element
FEATURE [App::DocumentObjectGroupPython] G4_Cl  # scripted group (container) (typed FeaturePython)
  Dunit = g/cm3
  Dvalue = 0.00299473
  Group = -> [Cl_element029]
  conduct = 2
  density = 1
  expand = 3
  formula = Cl
  name = G4_Cl
  specific = 4
FEATURE [App::DocumentObjectGroupPython] Ar_element002  label="Ar_element : 1"  # scripted group (container) (typed FeaturePython)
  n = 1
  ref = Ar_element
FEATURE [App::DocumentObjectGroupPython] G4_Ar  # scripted group (container) (typed FeaturePython)
  Dunit = g/cm3
  Dvalue = 0.00166201
  Group = -> [Ar_element002]
  conduct = 2
  density = 1
  expand = 3
  formula = Ar
  name = G4_Ar
  specific = 4
FEATURE [App::DocumentObjectGroupPython] K_element013  label="K_element : 003"  # scripted group (container) (typed FeaturePython)
  n = 1
  ref = K_element
FEATURE [App::DocumentObjectGroupPython] G4_K  # scripted group (container) (typed FeaturePython)
  Dunit = g/cm3
  Dvalue = 0.862
  Group = -> [K_element013]
  conduct = 2
  density = 1
  expand = 3
  formula = K
  name = G4_K
  specific = 4
FEATURE [App::DocumentObjectGroupPython] Ca_element014  label="Ca_element : 007"  # scripted group (container) (typed FeaturePython)
  n = 1
  ref = Ca_element
FEATURE [App::DocumentObjectGroupPython] G4_Ca  # scripted group (container) (typed FeaturePython)
  Dunit = g/cm3
  Dvalue = 1.55
  Group = -> [Ca_element014]
  conduct = 2
  density = 1
  expand = 3
  formula = Ca
  name = G4_Ca
  specific = 4
FEATURE [App::DocumentObjectGroupPython] Sc_element001  label="Sc_element : 1"  # scripted group (container) (typed FeaturePython)
  n = 1
  ref = Sc_element
FEATURE [App::DocumentObjectGroupPython] G4_Sc  # scripted group (container) (typed FeaturePython)
  Dunit = g/cm3
  Dvalue = 2.989
  Group = -> [Sc_element001]
  conduct = 2
  density = 1
  expand = 3
  formula = Sc
  name = G4_Sc
  specific = 4
FEATURE [App::DocumentObjectGroupPython] Ti_element004  label="Ti_element : 002"  # scripted group (container) (typed FeaturePython)
  n = 1
  ref = Ti_element
FEATURE [App::DocumentObjectGroupPython] G4_Ti  # scripted group (container) (typed FeaturePython)
  Dunit = g/cm3
  Dvalue = 4.54
  Group = -> [Ti_element004]
  conduct = 2
  density = 1
  expand = 3
  formula = Ti
  name = G4_Ti
  specific = 4
FEATURE [App::DocumentObjectGroupPython] V_element001  label="V_element : 1"  # scripted group (container) (typed FeaturePython)
  n = 1
  ref = V_element
FEATURE [App::DocumentObjectGroupPython] G4_V  # scripted group (container) (typed FeaturePython)
  Dunit = g/cm3
  Dvalue = 6.11
  Group = -> [V_element001]
  conduct = 2
  density = 1
  expand = 3
  formula = V
  name = G4_V
  specific = 4
FEATURE [App::DocumentObjectGroupPython] Cr_element001  label="Cr_element : 1"  # scripted group (container) (typed FeaturePython)
  n = 1
  ref = Cr_element
FEATURE [App::DocumentObjectGroupPython] G4_Cr  # scripted group (container) (typed FeaturePython)
  Dunit = g/cm3
  Dvalue = 7.18
  Group = -> [Cr_element001]
  conduct = 2
  density = 1
  expand = 3
  formula = Cr
  name = G4_Cr
  specific = 4
FEATURE [App::DocumentObjectGroupPython] Mn_element001  label="Mn_element : 1"  # scripted group (container) (typed FeaturePython)
  n = 1
  ref = Mn_element
FEATURE [App::DocumentObjectGroupPython] G4_Mn  # scripted group (container) (typed FeaturePython)
  Dunit = g/cm3
  Dvalue = 7.44
  Group = -> [Mn_element001]
  conduct = 2
  density = 1
  expand = 3
  formula = Mn
  name = G4_Mn
  specific = 4
FEATURE [App::DocumentObjectGroupPython] Fe_element007  label="Fe_element : 004"  # scripted group (container) (typed FeaturePython)
  n = 1
  ref = Fe_element
FEATURE [App::DocumentObjectGroupPython] G4_Fe  # scripted group (container) (typed FeaturePython)
  Dunit = g/cm3
  Dvalue = 7.874
  Group = -> [Fe_element007]
  conduct = 2
  density = 1
  expand = 3
  formula = Fe
  name = G4_Fe
  specific = 4
FEATURE [App::DocumentObjectGroupPython] Co_element001  label="Co_element : 1"  # scripted group (container) (typed FeaturePython)
  n = 1
  ref = Co_element
FEATURE [App::DocumentObjectGroupPython] G4_Co  # scripted group (container) (typed FeaturePython)
  Dunit = g/cm3
  Dvalue = 8.9
  Group = -> [Co_element001]
  conduct = 2
  density = 1
  expand = 3
  formula = Co
  name = G4_Co
  specific = 4
FEATURE [App::DocumentObjectGroupPython] Ni_element001  label="Ni_element : 1"  # scripted group (container) (typed FeaturePython)
  n = 1
  ref = Ni_element
FEATURE [App::DocumentObjectGroupPython] G4_Ni  # scripted group (container) (typed FeaturePython)
  Dunit = g/cm3
  Dvalue = 8.902
  Group = -> [Ni_element001]
  conduct = 2
  density = 1
  expand = 3
  formula = Ni
  name = G4_Ni
  specific = 4
FEATURE [App::DocumentObjectGroupPython] Cu_element001  label="Cu_element : 1"  # scripted group (container) (typed FeaturePython)
  n = 1
  ref = Cu_element
FEATURE [App::DocumentObjectGroupPython] G4_Cu  # scripted group (container) (typed FeaturePython)
  Dunit = g/cm3
  Dvalue = 8.96
  Group = -> [Cu_element001]
  conduct = 2
  density = 1
  expand = 3
  formula = Cu
  name = G4_Cu
  specific = 4
FEATURE [App::DocumentObjectGroupPython] Zn_element001  label="Zn_element : 1"  # scripted group (container) (typed FeaturePython)
  n = 1
  ref = Zn_element
FEATURE [App::DocumentObjectGroupPython] G4_Zn  # scripted group (container) (typed FeaturePython)
  Dunit = g/cm3
  Dvalue = 7.133
  Group = -> [Zn_element001]
  conduct = 2
  density = 1
  expand = 3
  formula = Zn
  name = G4_Zn
  specific = 4
FEATURE [App::DocumentObjectGroupPython] Ga_element002  label="Ga_element : 002"  # scripted group (container) (typed FeaturePython)
  n = 1
  ref = Ga_element
FEATURE [App::DocumentObjectGroupPython] G4_Ga  # scripted group (container) (typed FeaturePython)
  Dunit = g/cm3
  Dvalue = 5.904
  Group = -> [Ga_element002]
  conduct = 2
  density = 1
  expand = 3
  formula = Ga
  name = G4_Ga
  specific = 4
FEATURE [App::DocumentObjectGroupPython] Ge_element002  label="Ge_element : 1"  # scripted group (container) (typed FeaturePython)
  n = 1
  ref = Ge_element
FEATURE [App::DocumentObjectGroupPython] G4_Ge  # scripted group (container) (typed FeaturePython)
  Dunit = g/cm3
  Dvalue = 5.323
  Group = -> [Ge_element002]
  conduct = 2
  density = 1
  expand = 3
  formula = Ge
  name = G4_Ge
  specific = 4
FEATURE [App::DocumentObjectGroupPython] As_element003  label="As_element : 002"  # scripted group (container) (typed FeaturePython)
  n = 1
  ref = As_element
FEATURE [App::DocumentObjectGroupPython] G4_As  # scripted group (container) (typed FeaturePython)
  Dunit = g/cm3
  Dvalue = 5.73
  Group = -> [As_element003]
  conduct = 2
  density = 1
  expand = 3
  formula = As
  name = G4_As
  specific = 4
FEATURE [App::DocumentObjectGroupPython] Se_element001  label="Se_element : 1"  # scripted group (container) (typed FeaturePython)
  n = 1
  ref = Se_element
FEATURE [App::DocumentObjectGroupPython] G4_Se  # scripted group (container) (typed FeaturePython)
  Dunit = g/cm3
  Dvalue = 4.5
  Group = -> [Se_element001]
  conduct = 2
  density = 1
  expand = 3
  formula = Se
  name = G4_Se
  specific = 4
FEATURE [App::DocumentObjectGroupPython] Br_element007  label="Br_element : 004"  # scripted group (container) (typed FeaturePython)
  n = 1
  ref = Br_element
FEATURE [App::DocumentObjectGroupPython] G4_Br  # scripted group (container) (typed FeaturePython)
  Dunit = g/cm3
  Dvalue = 0.0070721
  Group = -> [Br_element007]
  conduct = 2
  density = 1
  expand = 3
  formula = Br
  name = G4_Br
  specific = 4
FEATURE [App::DocumentObjectGroupPython] Kr_element001  label="Kr_element : 1"  # scripted group (container) (typed FeaturePython)
  n = 1
  ref = Kr_element
FEATURE [App::DocumentObjectGroupPython] G4_Kr  # scripted group (container) (typed FeaturePython)
  Dunit = g/cm3
  Dvalue = 0.00347832
  Group = -> [Kr_element001]
  conduct = 2
  density = 1
  expand = 3
  formula = Kr
  name = G4_Kr
  specific = 4
FEATURE [App::DocumentObjectGroupPython] Rb_element001  label="Rb_element : 1"  # scripted group (container) (typed FeaturePython)
  n = 1
  ref = Rb_element
FEATURE [App::DocumentObjectGroupPython] G4_Rb  # scripted group (container) (typed FeaturePython)
  Dunit = g/cm3
  Dvalue = 1.532
  Group = -> [Rb_element001]
  conduct = 2
  density = 1
  expand = 3
  formula = Rb
  name = G4_Rb
  specific = 4
FEATURE [App::DocumentObjectGroupPython] Sr_element001  label="Sr_element : 1"  # scripted group (container) (typed FeaturePython)
  n = 1
  ref = Sr_element
FEATURE [App::DocumentObjectGroupPython] G4_Sr  # scripted group (container) (typed FeaturePython)
  Dunit = g/cm3
  Dvalue = 2.54
  Group = -> [Sr_element001]
  conduct = 2
  density = 1
  expand = 3
  formula = Sr
  name = G4_Sr
  specific = 4
FEATURE [App::DocumentObjectGroupPython] Y_element001  label="Y_element : 1"  # scripted group (container) (typed FeaturePython)
  n = 1
  ref = Y_element
FEATURE [App::DocumentObjectGroupPython] G4_Y  # scripted group (container) (typed FeaturePython)
  Dunit = g/cm3
  Dvalue = 4.469
  Group = -> [Y_element001]
  conduct = 2
  density = 1
  expand = 3
  formula = Y
  name = G4_Y
  specific = 4
FEATURE [App::DocumentObjectGroupPython] Zr_element001  label="Zr_element : 1"  # scripted group (container) (typed FeaturePython)
  n = 1
  ref = Zr_element
FEATURE [App::DocumentObjectGroupPython] G4_Zr  # scripted group (container) (typed FeaturePython)
  Dunit = g/cm3
  Dvalue = 6.506
  Group = -> [Zr_element001]
  conduct = 2
  density = 1
  expand = 3
  formula = Zr
  name = G4_Zr
  specific = 4
FEATURE [App::DocumentObjectGroupPython] Nb_element001  label="Nb_element : 1"  # scripted group (container) (typed FeaturePython)
  n = 1
  ref = Nb_element
FEATURE [App::DocumentObjectGroupPython] G4_Nb  # scripted group (container) (typed FeaturePython)
  Dunit = g/cm3
  Dvalue = 8.57
  Group = -> [Nb_element001]
  conduct = 2
  density = 1
  expand = 3
  formula = Nb
  name = G4_Nb
  specific = 4
FEATURE [App::DocumentObjectGroupPython] Mo_element001  label="Mo_element : 1"  # scripted group (container) (typed FeaturePython)
  n = 1
  ref = Mo_element
FEATURE [App::DocumentObjectGroupPython] G4_Mo  # scripted group (container) (typed FeaturePython)
  Dunit = g/cm3
  Dvalue = 10.22
  Group = -> [Mo_element001]
  conduct = 2
  density = 1
  expand = 3
  formula = Mo
  name = G4_Mo
  specific = 4
FEATURE [App::DocumentObjectGroupPython] Tc_element001  label="Tc_element : 1"  # scripted group (container) (typed FeaturePython)
  n = 1
  ref = Tc_element
FEATURE [App::DocumentObjectGroupPython] G4_Tc  # scripted group (container) (typed FeaturePython)
  Dunit = g/cm3
  Dvalue = 11.5
  Group = -> [Tc_element001]
  conduct = 2
  density = 1
  expand = 3
  formula = Tc
  name = G4_Tc
  specific = 4
FEATURE [App::DocumentObjectGroupPython] Ru_element001  label="Ru_element : 1"  # scripted group (container) (typed FeaturePython)
  n = 1
  ref = Ru_element
FEATURE [App::DocumentObjectGroupPython] G4_Ru  # scripted group (container) (typed FeaturePython)
  Dunit = g/cm3
  Dvalue = 12.41
  Group = -> [Ru_element001]
  conduct = 2
  density = 1
  expand = 3
  formula = Ru
  name = G4_Ru
  specific = 4
FEATURE [App::DocumentObjectGroupPython] Rh_element001  label="Rh_element : 1"  # scripted group (container) (typed FeaturePython)
  n = 1
  ref = Rh_element
FEATURE [App::DocumentObjectGroupPython] G4_Rh  # scripted group (container) (typed FeaturePython)
  Dunit = g/cm3
  Dvalue = 12.41
  Group = -> [Rh_element001]
  conduct = 2
  density = 1
  expand = 3
  formula = Rh
  name = G4_Rh
  specific = 4
FEATURE [App::DocumentObjectGroupPython] Pd_element001  label="Pd_element : 1"  # scripted group (container) (typed FeaturePython)
  n = 1
  ref = Pd_element
FEATURE [App::DocumentObjectGroupPython] G4_Pd  # scripted group (container) (typed FeaturePython)
  Dunit = g/cm3
  Dvalue = 12.02
  Group = -> [Pd_element001]
  conduct = 2
  density = 1
  expand = 3
  formula = Pd
  name = G4_Pd
  specific = 4
FEATURE [App::DocumentObjectGroupPython] Ag_element006  label="Ag_element : 004"  # scripted group (container) (typed FeaturePython)
  n = 1
  ref = Ag_element
FEATURE [App::DocumentObjectGroupPython] G4_Ag  # scripted group (container) (typed FeaturePython)
  Dunit = g/cm3
  Dvalue = 10.5
  Group = -> [Ag_element006]
  conduct = 2
  density = 1
  expand = 3
  formula = Ag
  name = G4_Ag
  specific = 4
FEATURE [App::DocumentObjectGroupPython] Cd_element003  label="Cd_element : 003"  # scripted group (container) (typed FeaturePython)
  n = 1
  ref = Cd_element
FEATURE [App::DocumentObjectGroupPython] G4_Cd  # scripted group (container) (typed FeaturePython)
  Dunit = g/cm3
  Dvalue = 8.65
  Group = -> [Cd_element003]
  conduct = 2
  density = 1
  expand = 3
  formula = Cd
  name = G4_Cd
  specific = 4
FEATURE [App::DocumentObjectGroupPython] In_element001  label="In_element : 1"  # scripted group (container) (typed FeaturePython)
  n = 1
  ref = In_element
FEATURE [App::DocumentObjectGroupPython] G4_In  # scripted group (container) (typed FeaturePython)
  Dunit = g/cm3
  Dvalue = 7.31
  Group = -> [In_element001]
  conduct = 2
  density = 1
  expand = 3
  formula = In
  name = G4_In
  specific = 4
FEATURE [App::DocumentObjectGroupPython] Sn_element001  label="Sn_element : 1"  # scripted group (container) (typed FeaturePython)
  n = 1
  ref = Sn_element
FEATURE [App::DocumentObjectGroupPython] G4_Sn  # scripted group (container) (typed FeaturePython)
  Dunit = g/cm3
  Dvalue = 7.31
  Group = -> [Sn_element001]
  conduct = 2
  density = 1
  expand = 3
  formula = Sn
  name = G4_Sn
  specific = 4
FEATURE [App::DocumentObjectGroupPython] Sb_element001  label="Sb_element : 1"  # scripted group (container) (typed FeaturePython)
  n = 1
  ref = Sb_element
FEATURE [App::DocumentObjectGroupPython] G4_Sb  # scripted group (container) (typed FeaturePython)
  Dunit = g/cm3
  Dvalue = 6.691
  Group = -> [Sb_element001]
  conduct = 2
  density = 1
  expand = 3
  formula = Sb
  name = G4_Sb
  specific = 4
FEATURE [App::DocumentObjectGroupPython] Te_element002  label="Te_element : 002"  # scripted group (container) (typed FeaturePython)
  n = 1
  ref = Te_element
FEATURE [App::DocumentObjectGroupPython] G4_Te  # scripted group (container) (typed FeaturePython)
  Dunit = g/cm3
  Dvalue = 6.24
  Group = -> [Te_element002]
  conduct = 2
  density = 1
  expand = 3
  formula = Te
  name = G4_Te
  specific = 4
FEATURE [App::DocumentObjectGroupPython] I_element010  label="I_element : 006"  # scripted group (container) (typed FeaturePython)
  n = 1
  ref = I_element
FEATURE [App::DocumentObjectGroupPython] G4_I  # scripted group (container) (typed FeaturePython)
  Dunit = g/cm3
  Dvalue = 4.93
  Group = -> [I_element010]
  conduct = 2
  density = 1
  expand = 3
  formula = I
  name = G4_I
  specific = 4
FEATURE [App::DocumentObjectGroupPython] Xe_element001  label="Xe_element : 1"  # scripted group (container) (typed FeaturePython)
  n = 1
  ref = Xe_element
FEATURE [App::DocumentObjectGroupPython] G4_Xe  # scripted group (container) (typed FeaturePython)
  Dunit = g/cm3
  Dvalue = 0.00548536
  Group = -> [Xe_element001]
  conduct = 2
  density = 1
  expand = 3
  formula = Xe
  name = G4_Xe
  specific = 4
FEATURE [App::DocumentObjectGroupPython] Cs_element003  label="Cs_element : 003"  # scripted group (container) (typed FeaturePython)
  n = 1
  ref = Cs_element
FEATURE [App::DocumentObjectGroupPython] G4_Cs  # scripted group (container) (typed FeaturePython)
  Dunit = g/cm3
  Dvalue = 1.873
  Group = -> [Cs_element003]
  conduct = 2
  density = 1
  expand = 3
  formula = Cs
  name = G4_Cs
  specific = 4
FEATURE [App::DocumentObjectGroupPython] Ba_element003  label="Ba_element : 003"  # scripted group (container) (typed FeaturePython)
  n = 1
  ref = Ba_element
FEATURE [App::DocumentObjectGroupPython] G4_Ba  # scripted group (container) (typed FeaturePython)
  Dunit = g/cm3
  Dvalue = 3.5
  Group = -> [Ba_element003]
  conduct = 2
  density = 1
  expand = 3
  formula = Ba
  name = G4_Ba
  specific = 4
FEATURE [App::DocumentObjectGroupPython] La_element003  label="La_element : 003"  # scripted group (container) (typed FeaturePython)
  n = 1
  ref = La_element
FEATURE [App::DocumentObjectGroupPython] G4_La  # scripted group (container) (typed FeaturePython)
  Dunit = g/cm3
  Dvalue = 6.154
  Group = -> [La_element003]
  conduct = 2
  density = 1
  expand = 3
  formula = La
  name = G4_La
  specific = 4
FEATURE [App::DocumentObjectGroupPython] Ce_element002  label="Ce_element : 1"  # scripted group (container) (typed FeaturePython)
  n = 1
  ref = Ce_element
FEATURE [App::DocumentObjectGroupPython] G4_Ce  # scripted group (container) (typed FeaturePython)
  Dunit = g/cm3
  Dvalue = 6.657
  Group = -> [Ce_element002]
  conduct = 2
  density = 1
  expand = 3
  formula = Ce
  name = G4_Ce
  specific = 4
FEATURE [App::DocumentObjectGroupPython] Pr_element001  label="Pr_element : 1"  # scripted group (container) (typed FeaturePython)
  n = 1
  ref = Pr_element
FEATURE [App::DocumentObjectGroupPython] G4_Pr  # scripted group (container) (typed FeaturePython)
  Dunit = g/cm3
  Dvalue = 6.71
  Group = -> [Pr_element001]
  conduct = 2
  density = 1
  expand = 3
  formula = Pr
  name = G4_Pr
  specific = 4
FEATURE [App::DocumentObjectGroupPython] Nd_element001  label="Nd_element : 1"  # scripted group (container) (typed FeaturePython)
  n = 1
  ref = Nd_element
FEATURE [App::DocumentObjectGroupPython] G4_Nd  # scripted group (container) (typed FeaturePython)
  Dunit = g/cm3
  Dvalue = 6.9
  Group = -> [Nd_element001]
  conduct = 2
  density = 1
  expand = 3
  formula = Nd
  name = G4_Nd
  specific = 4
FEATURE [App::DocumentObjectGroupPython] Pm_element001  label="Pm_element : 1"  # scripted group (container) (typed FeaturePython)
  n = 1
  ref = Pm_element
FEATURE [App::DocumentObjectGroupPython] G4_Pm  # scripted group (container) (typed FeaturePython)
  Dunit = g/cm3
  Dvalue = 7.22
  Group = -> [Pm_element001]
  conduct = 2
  density = 1
  expand = 3
  formula = Pm
  name = G4_Pm
  specific = 4
FEATURE [App::DocumentObjectGroupPython] Sm_element001  label="Sm_element : 1"  # scripted group (container) (typed FeaturePython)
  n = 1
  ref = Sm_element
FEATURE [App::DocumentObjectGroupPython] G4_Sm  # scripted group (container) (typed FeaturePython)
  Dunit = g/cm3
  Dvalue = 7.46
  Group = -> [Sm_element001]
  conduct = 2
  density = 1
  expand = 3
  formula = Sm
  name = G4_Sm
  specific = 4
FEATURE [App::DocumentObjectGroupPython] Eu_element001  label="Eu_element : 1"  # scripted group (container) (typed FeaturePython)
  n = 1
  ref = Eu_element
FEATURE [App::DocumentObjectGroupPython] G4_Eu  # scripted group (container) (typed FeaturePython)
  Dunit = g/cm3
  Dvalue = 5.243
  Group = -> [Eu_element001]
  conduct = 2
  density = 1
  expand = 3
  formula = Eu
  name = G4_Eu
  specific = 4
FEATURE [App::DocumentObjectGroupPython] Gd_element002  label="Gd_element : 1"  # scripted group (container) (typed FeaturePython)
  n = 1
  ref = Gd_element
FEATURE [App::DocumentObjectGroupPython] G4_Gd  # scripted group (container) (typed FeaturePython)
  Dunit = g/cm3
  Dvalue = 7.9004
  Group = -> [Gd_element002]
  conduct = 2
  density = 1
  expand = 3
  formula = Gd
  name = G4_Gd
  specific = 4
FEATURE [App::DocumentObjectGroupPython] Tb_element001  label="Tb_element : 1"  # scripted group (container) (typed FeaturePython)
  n = 1
  ref = Tb_element
FEATURE [App::DocumentObjectGroupPython] G4_Tb  # scripted group (container) (typed FeaturePython)
  Dunit = g/cm3
  Dvalue = 8.229
  Group = -> [Tb_element001]
  conduct = 2
  density = 1
  expand = 3
  formula = Tb
  name = G4_Tb
  specific = 4
FEATURE [App::DocumentObjectGroupPython] Dy_element001  label="Dy_element : 1"  # scripted group (container) (typed FeaturePython)
  n = 1
  ref = Dy_element
FEATURE [App::DocumentObjectGroupPython] G4_Dy  # scripted group (container) (typed FeaturePython)
  Dunit = g/cm3
  Dvalue = 8.55
  Group = -> [Dy_element001]
  conduct = 2
  density = 1
  expand = 3
  formula = Dy
  name = G4_Dy
  specific = 4
FEATURE [App::DocumentObjectGroupPython] Ho_element001  label="Ho_element : 1"  # scripted group (container) (typed FeaturePython)
  n = 1
  ref = Ho_element
FEATURE [App::DocumentObjectGroupPython] G4_Ho  # scripted group (container) (typed FeaturePython)
  Dunit = g/cm3
  Dvalue = 8.795
  Group = -> [Ho_element001]
  conduct = 2
  density = 1
  expand = 3
  formula = Ho
  name = G4_Ho
  specific = 4
FEATURE [App::DocumentObjectGroupPython] Er_element001  label="Er_element : 1"  # scripted group (container) (typed FeaturePython)
  n = 1
  ref = Er_element
FEATURE [App::DocumentObjectGroupPython] G4_Er  # scripted group (container) (typed FeaturePython)
  Dunit = g/cm3
  Dvalue = 9.066
  Group = -> [Er_element001]
  conduct = 2
  density = 1
  expand = 3
  formula = Er
  name = G4_Er
  specific = 4
FEATURE [App::DocumentObjectGroupPython] Tm_element001  label="Tm_element : 1"  # scripted group (container) (typed FeaturePython)
  n = 1
  ref = Tm_element
FEATURE [App::DocumentObjectGroupPython] G4_Tm  # scripted group (container) (typed FeaturePython)
  Dunit = g/cm3
  Dvalue = 9.321
  Group = -> [Tm_element001]
  conduct = 2
  density = 1
  expand = 3
  formula = Tm
  name = G4_Tm
  specific = 4
FEATURE [App::DocumentObjectGroupPython] Yb_element001  label="Yb_element : 1"  # scripted group (container) (typed FeaturePython)
  n = 1
  ref = Yb_element
FEATURE [App::DocumentObjectGroupPython] G4_Yb  # scripted group (container) (typed FeaturePython)
  Dunit = g/cm3
  Dvalue = 6.73
  Group = -> [Yb_element001]
  conduct = 2
  density = 1
  expand = 3
  formula = Yb
  name = G4_Yb
  specific = 4
FEATURE [App::DocumentObjectGroupPython] Lu_element001  label="Lu_element : 1"  # scripted group (container) (typed FeaturePython)
  n = 1
  ref = Lu_element
FEATURE [App::DocumentObjectGroupPython] G4_Lu  # scripted group (container) (typed FeaturePython)
  Dunit = g/cm3
  Dvalue = 9.84
  Group = -> [Lu_element001]
  conduct = 2
  density = 1
  expand = 3
  formula = Lu
  name = G4_Lu
  specific = 4
FEATURE [App::DocumentObjectGroupPython] Hf_element001  label="Hf_element : 1"  # scripted group (container) (typed FeaturePython)
  n = 1
  ref = Hf_element
FEATURE [App::DocumentObjectGroupPython] G4_Hf  # scripted group (container) (typed FeaturePython)
  Dunit = g/cm3
  Dvalue = 13.31
  Group = -> [Hf_element001]
  conduct = 2
  density = 1
  expand = 3
  formula = Hf
  name = G4_Hf
  specific = 4
FEATURE [App::DocumentObjectGroupPython] Ta_element001  label="Ta_element : 1"  # scripted group (container) (typed FeaturePython)
  n = 1
  ref = Ta_element
FEATURE [App::DocumentObjectGroupPython] G4_Ta  # scripted group (container) (typed FeaturePython)
  Dunit = g/cm3
  Dvalue = 16.654
  Group = -> [Ta_element001]
  conduct = 2
  density = 1
  expand = 3
  formula = Ta
  name = G4_Ta
  specific = 4
FEATURE [App::DocumentObjectGroupPython] W_element004  label="W_element : 004"  # scripted group (container) (typed FeaturePython)
  n = 1
  ref = W_element
FEATURE [App::DocumentObjectGroupPython] G4_W  # scripted group (container) (typed FeaturePython)
  Dunit = g/cm3
  Dvalue = 19.3
  Group = -> [W_element004]
  conduct = 2
  density = 1
  expand = 3
  formula = W
  name = G4_W
  specific = 4
FEATURE [App::DocumentObjectGroupPython] Re_element001  label="Re_element : 1"  # scripted group (container) (typed FeaturePython)
  n = 1
  ref = Re_element
FEATURE [App::DocumentObjectGroupPython] G4_Re  # scripted group (container) (typed FeaturePython)
  Dunit = g/cm3
  Dvalue = 21.02
  Group = -> [Re_element001]
  conduct = 2
  density = 1
  expand = 3
  formula = Re
  name = G4_Re
  specific = 4
FEATURE [App::DocumentObjectGroupPython] Os_element001  label="Os_element : 1"  # scripted group (container) (typed FeaturePython)
  n = 1
  ref = Os_element
FEATURE [App::DocumentObjectGroupPython] G4_Os  # scripted group (container) (typed FeaturePython)
  Dunit = g/cm3
  Dvalue = 22.57
  Group = -> [Os_element001]
  conduct = 2
  density = 1
  expand = 3
  formula = Os
  name = G4_Os
  specific = 4
FEATURE [App::DocumentObjectGroupPython] Ir_element001  label="Ir_element : 1"  # scripted group (container) (typed FeaturePython)
  n = 1
  ref = Ir_element
FEATURE [App::DocumentObjectGroupPython] G4_Ir  # scripted group (container) (typed FeaturePython)
  Dunit = g/cm3
  Dvalue = 22.42
  Group = -> [Ir_element001]
  conduct = 2
  density = 1
  expand = 3
  formula = Ir
  name = G4_Ir
  specific = 4
FEATURE [App::DocumentObjectGroupPython] Pt_element001  label="Pt_element : 1"  # scripted group (container) (typed FeaturePython)
  n = 1
  ref = Pt_element
FEATURE [App::DocumentObjectGroupPython] G4_Pt  # scripted group (container) (typed FeaturePython)
  Dunit = g/cm3
  Dvalue = 21.45
  Group = -> [Pt_element001]
  conduct = 2
  density = 1
  expand = 3
  formula = Pt
  name = G4_Pt
  specific = 4
FEATURE [App::DocumentObjectGroupPython] Au_element001  label="Au_element : 1"  # scripted group (container) (typed FeaturePython)
  n = 1
  ref = Au_element
FEATURE [App::DocumentObjectGroupPython] G4_Au  # scripted group (container) (typed FeaturePython)
  Dunit = g/cm3
  Dvalue = 19.32
  Group = -> [Au_element001]
  conduct = 2
  density = 1
  expand = 3
  formula = Au
  name = G4_Au
  specific = 4
FEATURE [App::DocumentObjectGroupPython] Hg_element002  label="Hg_element : 002"  # scripted group (container) (typed FeaturePython)
  n = 1
  ref = Hg_element
FEATURE [App::DocumentObjectGroupPython] G4_Hg  # scripted group (container) (typed FeaturePython)
  Dunit = g/cm3
  Dvalue = 13.546
  Group = -> [Hg_element002]
  conduct = 2
  density = 1
  expand = 3
  formula = Hg
  name = G4_Hg
  specific = 4
FEATURE [App::DocumentObjectGroupPython] Tl_element002  label="Tl_element : 002"  # scripted group (container) (typed FeaturePython)
  n = 1
  ref = Tl_element
FEATURE [App::DocumentObjectGroupPython] G4_Tl  # scripted group (container) (typed FeaturePython)
  Dunit = g/cm3
  Dvalue = 11.72
  Group = -> [Tl_element002]
  conduct = 2
  density = 1
  expand = 3
  formula = Tl
  name = G4_Tl
  specific = 4
FEATURE [App::DocumentObjectGroupPython] Pb_element003  label="Pb_element : 1"  # scripted group (container) (typed FeaturePython)
  n = 1
  ref = Pb_element
FEATURE [App::DocumentObjectGroupPython] G4_Pb  # scripted group (container) (typed FeaturePython)
  Dunit = g/cm3
  Dvalue = 11.35
  Group = -> [Pb_element003]
  conduct = 2
  density = 1
  expand = 3
  formula = Pb
  name = G4_Pb
  specific = 4
FEATURE [App::DocumentObjectGroupPython] Bi_element002  label="Bi_element : 1"  # scripted group (container) (typed FeaturePython)
  n = 1
  ref = Bi_element
FEATURE [App::DocumentObjectGroupPython] G4_Bi  # scripted group (container) (typed FeaturePython)
  Dunit = g/cm3
  Dvalue = 9.747
  Group = -> [Bi_element002]
  conduct = 2
  density = 1
  expand = 3
  formula = Bi
  name = G4_Bi
  specific = 4
FEATURE [App::DocumentObjectGroupPython] Po_element001  label="Po_element : 1"  # scripted group (container) (typed FeaturePython)
  n = 1
  ref = Po_element
FEATURE [App::DocumentObjectGroupPython] G4_Po  # scripted group (container) (typed FeaturePython)
  Dunit = g/cm3
  Dvalue = 9.32
  Group = -> [Po_element001]
  conduct = 2
  density = 1
  expand = 3
  formula = Po
  name = G4_Po
  specific = 4
FEATURE [App::DocumentObjectGroupPython] At_element001  label="At_element : 1"  # scripted group (container) (typed FeaturePython)
  n = 1
  ref = At_element
FEATURE [App::DocumentObjectGroupPython] G4_At  # scripted group (container) (typed FeaturePython)
  Dunit = g/cm3
  Dvalue = 9.32
  Group = -> [At_element001]
  conduct = 2
  density = 1
  expand = 3
  formula = At
  name = G4_At
  specific = 4
FEATURE [App::DocumentObjectGroupPython] Rn_element001  label="Rn_element : 1"  # scripted group (container) (typed FeaturePython)
  n = 1
  ref = Rn_element
FEATURE [App::DocumentObjectGroupPython] G4_Rn  # scripted group (container) (typed FeaturePython)
  Dunit = g/cm3
  Dvalue = 0.00900662
  Group = -> [Rn_element001]
  conduct = 2
  density = 1
  expand = 3
  formula = Rn
  name = G4_Rn
  specific = 4
FEATURE [App::DocumentObjectGroupPython] Fr_element001  label="Fr_element : 1"  # scripted group (container) (typed FeaturePython)
  n = 1
  ref = Fr_element
FEATURE [App::DocumentObjectGroupPython] G4_Fr  # scripted group (container) (typed FeaturePython)
  Dunit = g/cm3
  Dvalue = 1
  Group = -> [Fr_element001]
  conduct = 2
  density = 1
  expand = 3
  formula = Fr
  name = G4_Fr
  specific = 4
FEATURE [App::DocumentObjectGroupPython] Ra_element001  label="Ra_element : 1"  # scripted group (container) (typed FeaturePython)
  n = 1
  ref = Ra_element
FEATURE [App::DocumentObjectGroupPython] G4_Ra  # scripted group (container) (typed FeaturePython)
  Dunit = g/cm3
  Dvalue = 5
  Group = -> [Ra_element001]
  conduct = 2
  density = 1
  expand = 3
  formula = Ra
  name = G4_Ra
  specific = 4
FEATURE [App::DocumentObjectGroupPython] Ac_element001  label="Ac_element : 1"  # scripted group (container) (typed FeaturePython)
  n = 1
  ref = Ac_element
FEATURE [App::DocumentObjectGroupPython] G4_Ac  # scripted group (container) (typed FeaturePython)
  Dunit = g/cm3
  Dvalue = 10.07
  Group = -> [Ac_element001]
  conduct = 2
  density = 1
  expand = 3
  formula = Ac
  name = G4_Ac
  specific = 4
FEATURE [App::DocumentObjectGroupPython] Th_element001  label="Th_element : 1"  # scripted group (container) (typed FeaturePython)
  n = 1
  ref = Th_element
FEATURE [App::DocumentObjectGroupPython] G4_Th  # scripted group (container) (typed FeaturePython)
  Dunit = g/cm3
  Dvalue = 11.72
  Group = -> [Th_element001]
  conduct = 2
  density = 1
  expand = 3
  formula = Th
  name = G4_Th
  specific = 4
FEATURE [App::DocumentObjectGroupPython] Pa_element001  label="Pa_element : 1"  # scripted group (container) (typed FeaturePython)
  n = 1
  ref = Pa_element
FEATURE [App::DocumentObjectGroupPython] G4_Pa  # scripted group (container) (typed FeaturePython)
  Dunit = g/cm3
  Dvalue = 15.37
  Group = -> [Pa_element001]
  conduct = 2
  density = 1
  expand = 3
  formula = Pa
  name = G4_Pa
  specific = 4
FEATURE [App::DocumentObjectGroupPython] U_element004  label="U_element : 004"  # scripted group (container) (typed FeaturePython)
  n = 1
  ref = U_element
FEATURE [App::DocumentObjectGroupPython] G4_U  # scripted group (container) (typed FeaturePython)
  Dunit = g/cm3
  Dvalue = 18.95
  Group = -> [U_element004]
  conduct = 2
  density = 1
  expand = 3
  formula = U
  name = G4_U
  specific = 4
FEATURE [App::DocumentObjectGroupPython] Np_element001  label="Np_element : 1"  # scripted group (container) (typed FeaturePython)
  n = 1
  ref = Np_element
FEATURE [App::DocumentObjectGroupPython] G4_Np  # scripted group (container) (typed FeaturePython)
  Dunit = g/cm3
  Dvalue = 20.25
  Group = -> [Np_element001]
  conduct = 2
  density = 1
  expand = 3
  formula = Np
  name = G4_Np
  specific = 4
FEATURE [App::DocumentObjectGroupPython] Pu_element002  label="Pu_element : 002"  # scripted group (container) (typed FeaturePython)
  n = 1
  ref = Pu_element
FEATURE [App::DocumentObjectGroupPython] G4_Pu  # scripted group (container) (typed FeaturePython)
  Dunit = g/cm3
  Dvalue = 19.84
  Group = -> [Pu_element002]
  conduct = 2
  density = 1
  expand = 3
  formula = Pu
  name = G4_Pu
  specific = 4
FEATURE [App::DocumentObjectGroupPython] Am_element001  label="Am_element : 1"  # scripted group (container) (typed FeaturePython)
  n = 1
  ref = Am_element
FEATURE [App::DocumentObjectGroupPython] G4_Am  # scripted group (container) (typed FeaturePython)
  Dunit = g/cm3
  Dvalue = 13.67
  Group = -> [Am_element001]
  conduct = 2
  density = 1
  expand = 3
  formula = Am
  name = G4_Am
  specific = 4
FEATURE [App::DocumentObjectGroupPython] Cm_element001  label="Cm_element : 1"  # scripted group (container) (typed FeaturePython)
  n = 1
  ref = Cm_element
FEATURE [App::DocumentObjectGroupPython] G4_Cm  # scripted group (container) (typed FeaturePython)
  Dunit = g/cm3
  Dvalue = 13.51
  Group = -> [Cm_element001]
  conduct = 2
  density = 1
  expand = 3
  formula = Cm
  name = G4_Cm
  specific = 4
FEATURE [App::DocumentObjectGroupPython] Bk_element001  label="Bk_element : 1"  # scripted group (container) (typed FeaturePython)
  n = 1
  ref = Bk_element
FEATURE [App::DocumentObjectGroupPython] G4_Bk  # scripted group (container) (typed FeaturePython)
  Dunit = g/cm3
  Dvalue = 14
  Group = -> [Bk_element001]
  conduct = 2
  density = 1
  expand = 3
  formula = Bk
  name = G4_Bk
  specific = 4
FEATURE [App::DocumentObjectGroupPython] Cf_element001  label="Cf_element : 1"  # scripted group (container) (typed FeaturePython)
  n = 1
  ref = Cf_element
FEATURE [App::DocumentObjectGroupPython] G4_Cf  # scripted group (container) (typed FeaturePython)
  Dunit = g/cm3
  Dvalue = 10
  Group = -> [Cf_element001]
  conduct = 2
  density = 1
  expand = 3
  formula = Cf
  name = G4_Cf
  specific = 4
FEATURE [App::DocumentObjectGroupPython] Element  # scripted group (container) (typed FeaturePython)
  Group = -> [G4_H,G4_He,G4_Li,G4_Be,G4_B,G4_C,G4_N,G4_O,G4_F,G4_Ne,G4_Na,G4_Mg,G4_Al,G4_Si,G4_P,G4_S,G4_Cl,G4_Ar,G4_K,G4_Ca,G4_Sc,G4_Ti,G4_V,G4_Cr,G4_Mn,G4_Fe,G4_Co,G4_Ni,G4_Cu,G4_Zn,G4_Ga,G4_Ge,G4_As,G4_Se,G4_Br,G4_Kr,G4_Rb,G4_Sr,G4_Y,G4_Zr,G4_Nb,G4_Mo,G4_Tc,G4_Ru,G4_Rh,G4_Pd,G4_Ag,G4_Cd,G4_In,G4_Sn,G4_Sb,G4_Te,G4_I,G4_Xe,G4_Cs,G4_Ba,G4_La,G4_Ce,G4_Pr,G4_Nd,G4_Pm,G4_Sm,G4_Eu,G4_Gd,G4_Tb,G4_Dy,G4_Ho,G4_Er,+30 more]
FEATURE [App::DocumentObjectGroupPython] H_element114  label="H_element : 063"  # scripted group (container) (typed FeaturePython)
  n = 2
  ref = H_element
FEATURE [App::DocumentObjectGroupPython] G4_lH2  # scripted group (container) (typed FeaturePython)
  Dunit = g/cm3
  Dvalue = 0.0708
  Group = -> [H_element114]
  conduct = 2
  density = 1
  expand = 3
  formula = G4_lH2
  name = G4_lH2
  specific = 4
FEATURE [App::DocumentObjectGroupPython] N_element049  label="N_element : 022"  # scripted group (container) (typed FeaturePython)
  n = 2
  ref = N_element
FEATURE [App::DocumentObjectGroupPython] G4_lN2  # scripted group (container) (typed FeaturePython)
  Dunit = g/cm3
  Dvalue = 0.807
  Group = -> [N_element049]
  conduct = 2
  density = 1
  expand = 3
  formula = G4_lN2
  name = G4_lN2
  specific = 4
FEATURE [App::DocumentObjectGroupPython] O_element106  label="O_element : 060"  # scripted group (container) (typed FeaturePython)
  n = 2
  ref = O_element
FEATURE [App::DocumentObjectGroupPython] G4_lO2  # scripted group (container) (typed FeaturePython)
  Dunit = g/cm3
  Dvalue = 1.141
  Group = -> [O_element106]
  conduct = 2
  density = 1
  expand = 3
  formula = G4_lO2
  name = G4_lO2
  specific = 4
FEATURE [App::DocumentObjectGroupPython] Ar  label="Ar : 1"  # scripted group (container) (typed FeaturePython)
  n = 1
  ref = Ar
FEATURE [App::DocumentObjectGroupPython] G4_lAr  # scripted group (container) (typed FeaturePython)
  Dunit = g/cm3
  Dvalue = 1.396
  Group = -> [Ar]
  conduct = 2
  density = 1
  expand = 3
  formula = G4_lAr
  name = G4_lAr
  specific = 4
FEATURE [App::DocumentObjectGroupPython] Br  label="Br : 1"  # scripted group (container) (typed FeaturePython)
  n = 1
  ref = Br
FEATURE [App::DocumentObjectGroupPython] G4_lBr  # scripted group (container) (typed FeaturePython)
  Dunit = g/cm3
  Dvalue = 3.1028
  Group = -> [Br]
  conduct = 2
  density = 1
  expand = 3
  formula = G4_lBr
  name = G4_lBr
  specific = 4
FEATURE [App::DocumentObjectGroupPython] Kr  label="Kr : 1"  # scripted group (container) (typed FeaturePython)
  n = 1
  ref = Kr
FEATURE [App::DocumentObjectGroupPython] G4_lKr  # scripted group (container) (typed FeaturePython)
  Dunit = g/cm3
  Dvalue = 2.418
  Group = -> [Kr]
  conduct = 2
  density = 1
  expand = 3
  formula = G4_lKr
  name = G4_lKr
  specific = 4
FEATURE [App::DocumentObjectGroupPython] Xe  label="Xe : 1"  # scripted group (container) (typed FeaturePython)
  n = 1
  ref = Xe
FEATURE [App::DocumentObjectGroupPython] G4_lXe  # scripted group (container) (typed FeaturePython)
  Dunit = g/cm3
  Dvalue = 2.953
  Group = -> [Xe]
  conduct = 2
  density = 1
  expand = 3
  formula = G4_lXe
  name = G4_lXe
  specific = 4
FEATURE [App::DocumentObjectGroupPython] O_element107  label="O_element : 061"  # scripted group (container) (typed FeaturePython)
  n = 4
  ref = O_element
FEATURE [App::DocumentObjectGroupPython] Pb_element004  label="Pb_element : 002"  # scripted group (container) (typed FeaturePython)
  n = 1
  ref = Pb_element
FEATURE [App::DocumentObjectGroupPython] W_element005  label="W_element : 005"  # scripted group (container) (typed FeaturePython)
  n = 1
  ref = W_element
FEATURE [App::DocumentObjectGroupPython] G4_PbWO4  # scripted group (container) (typed FeaturePython)
  Dunit = g/cm3
  Dvalue = 8.28
  Group = -> [O_element107,Pb_element004,W_element005]
  conduct = 2
  density = 1
  expand = 3
  formula = G4_PbWO4
  name = G4_PbWO4
  specific = 4
FEATURE [App::DocumentObjectGroupPython] alactic  label="alactic : 1"  # scripted group (container) (typed FeaturePython)
  n = 1
  ref = alactic
FEATURE [App::DocumentObjectGroupPython] G4_Galactic  # scripted group (container) (typed FeaturePython)
  Dunit = g/cm3
  Dvalue = 0
  Group = -> [alactic]
  conduct = 2
  density = 1
  expand = 3
  formula = G4_Galactic
  name = G4_Galactic
  specific = 4
FEATURE [App::DocumentObjectGroupPython] RAPHITE_POROUS  label="RAPHITE_POROUS : 1"  # scripted group (container) (typed FeaturePython)
  n = 1
  ref = RAPHITE_POROUS
FEATURE [App::DocumentObjectGroupPython] G4_GRAPHITE_POROUS  # scripted group (container) (typed FeaturePython)
  Dunit = g/cm3
  Dvalue = 1.7
  Group = -> [RAPHITE_POROUS]
  conduct = 2
  density = 1
  expand = 3
  formula = G4_GRAPHITE_POROUS
  name = G4_GRAPHITE_POROUS
  specific = 4
FEATURE [App::DocumentObjectGroupPython] H_element115  label="H_element : 0.150"  # scripted group (container) (typed FeaturePython)
  n = 0.080538
FEATURE [App::DocumentObjectGroupPython] C_element125  label="C_element : 0.600"  # scripted group (container) (typed FeaturePython)
  n = 0.599848
FEATURE [App::DocumentObjectGroupPython] O_element108  label="O_element : 0.320"  # scripted group (container) (typed FeaturePython)
  n = 0.319614
FEATURE [App::DocumentObjectGroupPython] G4_LUCITE  # scripted group (container) (typed FeaturePython)
  Dunit = g/cm3
  Dvalue = 1.19
  Group = -> [H_element115,C_element125,O_element108]
  conduct = 2
  density = 1
  expand = 3
  formula = G4_LUCITE
  name = G4_LUCITE
  specific = 4
FEATURE [App::DocumentObjectGroupPython] Cu_element002  label="Cu_element : 62"  # scripted group (container) (typed FeaturePython)
  n = 62
  ref = Cu_element
FEATURE [App::DocumentObjectGroupPython] Zn_element002  label="Zn_element : 35"  # scripted group (container) (typed FeaturePython)
  n = 35
  ref = Zn_element
FEATURE [App::DocumentObjectGroupPython] Pb_element005  label="Pb_element : 3"  # scripted group (container) (typed FeaturePython)
  n = 3
  ref = Pb_element
FEATURE [App::DocumentObjectGroupPython] G4_BRASS  # scripted group (container) (typed FeaturePython)
  Dunit = g/cm3
  Dvalue = 8.52
  Group = -> [Cu_element002,Zn_element002,Pb_element005]
  conduct = 2
  density = 1
  expand = 3
  formula = G4_BRASS
  name = G4_BRASS
  specific = 4
FEATURE [App::DocumentObjectGroupPython] Cu_element003  label="Cu_element : 89"  # scripted group (container) (typed FeaturePython)
  n = 89
  ref = Cu_element
FEATURE [App::DocumentObjectGroupPython] Zn_element003  label="Zn_element : 9"  # scripted group (container) (typed FeaturePython)
  n = 9
  ref = Zn_element
FEATURE [App::DocumentObjectGroupPython] Pb_element006  label="Pb_element : 2"  # scripted group (container) (typed FeaturePython)
  n = 2
  ref = Pb_element
FEATURE [App::DocumentObjectGroupPython] G4_BRONZE  # scripted group (container) (typed FeaturePython)
  Dunit = g/cm3
  Dvalue = 8.82
  Group = -> [Cu_element003,Zn_element003,Pb_element006]
  conduct = 2
  density = 1
  expand = 3
  formula = G4_BRONZE
  name = G4_BRONZE
  specific = 4
FEATURE [App::DocumentObjectGroupPython] Fe_element008  label="Fe_element : 74"  # scripted group (container) (typed FeaturePython)
  n = 74
  ref = Fe_element
FEATURE [App::DocumentObjectGroupPython] Cr_element002  label="Cr_element : 18"  # scripted group (container) (typed FeaturePython)
  n = 18
  ref = Cr_element
FEATURE [App::DocumentObjectGroupPython] Ni_element002  label="Ni_element : 8"  # scripted group (container) (typed FeaturePython)
  n = 8
  ref = Ni_element
FEATURE [App::DocumentObjectGroupPython] G4_STAINLESS_STEEL  label="G4_STAINLESS-STEEL"  # scripted group (container) (typed FeaturePython)
  Dunit = g/cm3
  Dvalue = 8
  Group = -> [Fe_element008,Cr_element002,Ni_element002]
  conduct = 2
  density = 1
  expand = 3
  formula = G4_STAINLESS-STEEL
  name = G4_STAINLESS-STEEL
  specific = 4
FEATURE [App::DocumentObjectGroupPython] H_element116  label="H_element : 064"  # scripted group (container) (typed FeaturePython)
  n = 18
  ref = H_element
FEATURE [App::DocumentObjectGroupPython] C_element126  label="C_element : 071"  # scripted group (container) (typed FeaturePython)
  n = 12
  ref = C_element
FEATURE [App::DocumentObjectGroupPython] O_element109  label="O_element : 062"  # scripted group (container) (typed FeaturePython)
  n = 7
  ref = O_element
FEATURE [App::DocumentObjectGroupPython] G4_CR39  # scripted group (container) (typed FeaturePython)
  Dunit = g/cm3
  Dvalue = 1.32
  Group = -> [H_element116,C_element126,O_element109]
  conduct = 2
  density = 1
  expand = 3
  formula = G4_CR39
  name = G4_CR39
  specific = 4
FEATURE [App::DocumentObjectGroupPython] H_element117  label="H_element : 38"  # scripted group (container) (typed FeaturePython)
  n = 38
  ref = H_element
FEATURE [App::DocumentObjectGroupPython] C_element127  label="C_element : 072"  # scripted group (container) (typed FeaturePython)
  n = 18
  ref = C_element
FEATURE [App::DocumentObjectGroupPython] O_element110  label="O_element : 063"  # scripted group (container) (typed FeaturePython)
  n = 1
  ref = O_element
FEATURE [App::DocumentObjectGroupPython] G4_OCTADECANOL  # scripted group (container) (typed FeaturePython)
  Dunit = g/cm3
  Dvalue = 0.812
  Group = -> [H_element117,C_element127,O_element110]
  conduct = 2
  density = 1
  expand = 3
  formula = G4_OCTADECANOL
  name = G4_OCTADECANOL
  specific = 4
FEATURE [App::DocumentObjectGroupPython] HEP  # scripted group (container) (typed FeaturePython)
  Group = -> [G4_lH2,G4_lN2,G4_lO2,G4_lAr,G4_lBr,G4_lKr,G4_lXe,G4_PbWO4,G4_Galactic,G4_GRAPHITE_POROUS,G4_LUCITE,G4_BRASS,G4_BRONZE,G4_STAINLESS_STEEL,G4_CR39,G4_OCTADECANOL]
FEATURE [App::DocumentObjectGroupPython] C_element128  label="C_element : 073"  # scripted group (container) (typed FeaturePython)
  n = 14
  ref = C_element
FEATURE [App::DocumentObjectGroupPython] H_element118  label="H_element : 065"  # scripted group (container) (typed FeaturePython)
  n = 10
  ref = H_element
FEATURE [App::DocumentObjectGroupPython] O_element111  label="O_element : 064"  # scripted group (container) (typed FeaturePython)
  n = 2
  ref = O_element
FEATURE [App::DocumentObjectGroupPython] N_element050  label="N_element : 023"  # scripted group (container) (typed FeaturePython)
  n = 2
  ref = N_element
FEATURE [App::DocumentObjectGroupPython] G4_KEVLAR  # scripted group (container) (typed FeaturePython)
  Dunit = g/cm3
  Dvalue = 1.44
  Group = -> [C_element128,H_element118,O_element111,N_element050]
  conduct = 2
  density = 1
  expand = 3
  formula = G4_KEVLAR
  name = G4_KEVLAR
  specific = 4
FEATURE [App::DocumentObjectGroupPython] C_element129  label="C_element : 074"  # scripted group (container) (typed FeaturePython)
  n = 10
  ref = C_element
FEATURE [App::DocumentObjectGroupPython] H_element119  label="H_element : 066"  # scripted group (container) (typed FeaturePython)
  n = 8
  ref = H_element
FEATURE [App::DocumentObjectGroupPython] O_element112  label="O_element : 065"  # scripted group (container) (typed FeaturePython)
  n = 4
  ref = O_element
FEATURE [App::DocumentObjectGroupPython] G4_DACRON  # scripted group (container) (typed FeaturePython)
  Dunit = g/cm3
  Dvalue = 1.4
  Group = -> [C_element129,H_element119,O_element112]
  conduct = 2
  density = 1
  expand = 3
  formula = G4_DACRON
  name = G4_DACRON
  specific = 4
FEATURE [App::DocumentObjectGroupPython] C_element130  label="C_element : 075"  # scripted group (container) (typed FeaturePython)
  n = 4
  ref = C_element
FEATURE [App::DocumentObjectGroupPython] H_element120  label="H_element : 067"  # scripted group (container) (typed FeaturePython)
  n = 5
  ref = H_element
FEATURE [App::DocumentObjectGroupPython] Cl_element030  label="Cl_element : 016"  # scripted group (container) (typed FeaturePython)
  n = 1
  ref = Cl_element
FEATURE [App::DocumentObjectGroupPython] G4_NEOPRENE  # scripted group (container) (typed FeaturePython)
  Dunit = g/cm3
  Dvalue = 1.23
  Group = -> [C_element130,H_element120,Cl_element030]
  conduct = 2
  density = 1
  expand = 3
  formula = G4_NEOPRENE
  name = G4_NEOPRENE
  specific = 4
FEATURE [App::DocumentObjectGroupPython] Space  # scripted group (container) (typed FeaturePython)
  Group = -> [G4_KEVLAR,G4_DACRON,G4_NEOPRENE]
FEATURE [App::DocumentObjectGroupPython] H_element121  label="H_element : 068"  # scripted group (container) (typed FeaturePython)
  n = 5
  ref = H_element
FEATURE [App::DocumentObjectGroupPython] C_element131  label="C_element : 076"  # scripted group (container) (typed FeaturePython)
  n = 4
  ref = C_element
FEATURE [App::DocumentObjectGroupPython] N_element051  label="N_element : 3"  # scripted group (container) (typed FeaturePython)
  n = 3
  ref = N_element
FEATURE [App::DocumentObjectGroupPython] O_element113  label="O_element : 066"  # scripted group (container) (typed FeaturePython)
  n = 1
  ref = O_element
FEATURE [App::DocumentObjectGroupPython] G4_CYTOSINE  # scripted group (container) (typed FeaturePython)
  Dunit = g/cm3
  Dvalue = 1.55
  Group = -> [H_element121,C_element131,N_element051,O_element113]
  conduct = 2
  density = 1
  expand = 3
  formula = G4_CYTOSINE
  name = G4_CYTOSINE
  specific = 4
FEATURE [App::DocumentObjectGroupPython] H_element122  label="H_element : 069"  # scripted group (container) (typed FeaturePython)
  n = 6
  ref = H_element
FEATURE [App::DocumentObjectGroupPython] C_element132  label="C_element : 077"  # scripted group (container) (typed FeaturePython)
  n = 5
  ref = C_element
FEATURE [App::DocumentObjectGroupPython] N_element052  label="N_element : 024"  # scripted group (container) (typed FeaturePython)
  n = 2
  ref = N_element
FEATURE [App::DocumentObjectGroupPython] O_element114  label="O_element : 067"  # scripted group (container) (typed FeaturePython)
  n = 2
  ref = O_element
FEATURE [App::DocumentObjectGroupPython] G4_THYMINE  # scripted group (container) (typed FeaturePython)
  Dunit = g/cm3
  Dvalue = 1.23
  Group = -> [H_element122,C_element132,N_element052,O_element114]
  conduct = 2
  density = 1
  expand = 3
  formula = G4_THYMINE
  name = G4_THYMINE
  specific = 4
FEATURE [App::DocumentObjectGroupPython] H_element123  label="H_element : 070"  # scripted group (container) (typed FeaturePython)
  n = 4
  ref = H_element
FEATURE [App::DocumentObjectGroupPython] C_element133  label="C_element : 078"  # scripted group (container) (typed FeaturePython)
  n = 4
  ref = C_element
FEATURE [App::DocumentObjectGroupPython] N_element053  label="N_element : 025"  # scripted group (container) (typed FeaturePython)
  n = 2
  ref = N_element
FEATURE [App::DocumentObjectGroupPython] O_element115  label="O_element : 068"  # scripted group (container) (typed FeaturePython)
  n = 2
  ref = O_element
FEATURE [App::DocumentObjectGroupPython] G4_URACIL  # scripted group (container) (typed FeaturePython)
  Dunit = g/cm3
  Dvalue = 1.32
  Group = -> [H_element123,C_element133,N_element053,O_element115]
  conduct = 2
  density = 1
  expand = 3
  formula = G4_URACIL
  name = G4_URACIL
  specific = 4
FEATURE [App::DocumentObjectGroupPython] H_element124  label="H_element : 071"  # scripted group (container) (typed FeaturePython)
  n = 4
  ref = H_element
FEATURE [App::DocumentObjectGroupPython] C_element134  label="C_element : 079"  # scripted group (container) (typed FeaturePython)
  n = 5
  ref = C_element
FEATURE [App::DocumentObjectGroupPython] N_element054  label="N_element : 026"  # scripted group (container) (typed FeaturePython)
  n = 5
  ref = N_element
FEATURE [App::DocumentObjectGroupPython] G4_DNA_ADENINE  # scripted group (container) (typed FeaturePython)
  Dunit = g/cm3
  Dvalue = 1
  Group = -> [H_element124,C_element134,N_element054]
  conduct = 2
  density = 1
  expand = 3
  formula = G4_DNA_ADENINE
  name = G4_DNA_ADENINE
  specific = 4
FEATURE [App::DocumentObjectGroupPython] H_element125  label="H_element : 072"  # scripted group (container) (typed FeaturePython)
  n = 4
  ref = H_element
FEATURE [App::DocumentObjectGroupPython] C_element135  label="C_element : 080"  # scripted group (container) (typed FeaturePython)
  n = 5
  ref = C_element
FEATURE [App::DocumentObjectGroupPython] N_element055  label="N_element : 027"  # scripted group (container) (typed FeaturePython)
  n = 5
  ref = N_element
FEATURE [App::DocumentObjectGroupPython] O_element116  label="O_element : 069"  # scripted group (container) (typed FeaturePython)
  n = 1
  ref = O_element
FEATURE [App::DocumentObjectGroupPython] G4_DNA_GUANINE  # scripted group (container) (typed FeaturePython)
  Dunit = g/cm3
  Dvalue = 1
  Group = -> [H_element125,C_element135,N_element055,O_element116]
  conduct = 2
  density = 1
  expand = 3
  formula = G4_DNA_GUANINE
  name = G4_DNA_GUANINE
  specific = 4
FEATURE [App::DocumentObjectGroupPython] H_element126  label="H_element : 073"  # scripted group (container) (typed FeaturePython)
  n = 4
  ref = H_element
FEATURE [App::DocumentObjectGroupPython] C_element136  label="C_element : 081"  # scripted group (container) (typed FeaturePython)
  n = 4
  ref = C_element
FEATURE [App::DocumentObjectGroupPython] N_element056  label="N_element : 028"  # scripted group (container) (typed FeaturePython)
  n = 3
  ref = N_element
FEATURE [App::DocumentObjectGroupPython] O_element117  label="O_element : 070"  # scripted group (container) (typed FeaturePython)
  n = 1
  ref = O_element
FEATURE [App::DocumentObjectGroupPython] G4_DNA_CYTOSINE  # scripted group (container) (typed FeaturePython)
  Dunit = g/cm3
  Dvalue = 1
  Group = -> [H_element126,C_element136,N_element056,O_element117]
  conduct = 2
  density = 1
  expand = 3
  formula = G4_DNA_CYTOSINE
  name = G4_DNA_CYTOSINE
  specific = 4
FEATURE [App::DocumentObjectGroupPython] H_element127  label="H_element : 074"  # scripted group (container) (typed FeaturePython)
  n = 5
  ref = H_element
FEATURE [App::DocumentObjectGroupPython] C_element137  label="C_element : 082"  # scripted group (container) (typed FeaturePython)
  n = 5
  ref = C_element
FEATURE [App::DocumentObjectGroupPython] N_element057  label="N_element : 029"  # scripted group (container) (typed FeaturePython)
  n = 2
  ref = N_element
FEATURE [App::DocumentObjectGroupPython] O_element118  label="O_element : 071"  # scripted group (container) (typed FeaturePython)
  n = 2
  ref = O_element
FEATURE [App::DocumentObjectGroupPython] G4_DNA_THYMINE  # scripted group (container) (typed FeaturePython)
  Dunit = g/cm3
  Dvalue = 1
  Group = -> [H_element127,C_element137,N_element057,O_element118]
  conduct = 2
  density = 1
  expand = 3
  formula = G4_DNA_THYMINE
  name = G4_DNA_THYMINE
  specific = 4
FEATURE [App::DocumentObjectGroupPython] H_element128  label="H_element : 075"  # scripted group (container) (typed FeaturePython)
  n = 3
  ref = H_element
FEATURE [App::DocumentObjectGroupPython] C_element138  label="C_element : 083"  # scripted group (container) (typed FeaturePython)
  n = 4
  ref = C_element
FEATURE [App::DocumentObjectGroupPython] N_element058  label="N_element : 030"  # scripted group (container) (typed FeaturePython)
  n = 2
  ref = N_element
FEATURE [App::DocumentObjectGroupPython] O_element119  label="O_element : 072"  # scripted group (container) (typed FeaturePython)
  n = 2
  ref = O_element
FEATURE [App::DocumentObjectGroupPython] G4_DNA_URACIL  # scripted group (container) (typed FeaturePython)
  Dunit = g/cm3
  Dvalue = 1
  Group = -> [H_element128,C_element138,N_element058,O_element119]
  conduct = 2
  density = 1
  expand = 3
  formula = G4_DNA_URACIL
  name = G4_DNA_URACIL
  specific = 4
FEATURE [App::DocumentObjectGroupPython] H_element129  label="H_element : 076"  # scripted group (container) (typed FeaturePython)
  n = 10
  ref = H_element
FEATURE [App::DocumentObjectGroupPython] C_element139  label="C_element : 084"  # scripted group (container) (typed FeaturePython)
  n = 10
  ref = C_element
FEATURE [App::DocumentObjectGroupPython] N_element059  label="N_element : 031"  # scripted group (container) (typed FeaturePython)
  n = 5
  ref = N_element
FEATURE [App::DocumentObjectGroupPython] O_element120  label="O_element : 073"  # scripted group (container) (typed FeaturePython)
  n = 4
  ref = O_element
FEATURE [App::DocumentObjectGroupPython] G4_DNA_ADENOSINE  # scripted group (container) (typed FeaturePython)
  Dunit = g/cm3
  Dvalue = 1
  Group = -> [H_element129,C_element139,N_element059,O_element120]
  conduct = 2
  density = 1
  expand = 3
  formula = G4_DNA_ADENOSINE
  name = G4_DNA_ADENOSINE
  specific = 4
FEATURE [App::DocumentObjectGroupPython] H_element130  label="H_element : 077"  # scripted group (container) (typed FeaturePython)
  n = 10
  ref = H_element
FEATURE [App::DocumentObjectGroupPython] C_element140  label="C_element : 085"  # scripted group (container) (typed FeaturePython)
  n = 10
  ref = C_element
FEATURE [App::DocumentObjectGroupPython] N_element060  label="N_element : 032"  # scripted group (container) (typed FeaturePython)
  n = 5
  ref = N_element
FEATURE [App::DocumentObjectGroupPython] O_element121  label="O_element : 074"  # scripted group (container) (typed FeaturePython)
  n = 5
  ref = O_element
FEATURE [App::DocumentObjectGroupPython] G4_DNA_GUANOSINE  # scripted group (container) (typed FeaturePython)
  Dunit = g/cm3
  Dvalue = 1
  Group = -> [H_element130,C_element140,N_element060,O_element121]
  conduct = 2
  density = 1
  expand = 3
  formula = G4_DNA_GUANOSINE
  name = G4_DNA_GUANOSINE
  specific = 4
FEATURE [App::DocumentObjectGroupPython] H_element131  label="H_element : 078"  # scripted group (container) (typed FeaturePython)
  n = 10
  ref = H_element
FEATURE [App::DocumentObjectGroupPython] C_element141  label="C_element : 086"  # scripted group (container) (typed FeaturePython)
  n = 9
  ref = C_element
FEATURE [App::DocumentObjectGroupPython] N_element061  label="N_element : 033"  # scripted group (container) (typed FeaturePython)
  n = 3
  ref = N_element
FEATURE [App::DocumentObjectGroupPython] O_element122  label="O_element : 075"  # scripted group (container) (typed FeaturePython)
  n = 5
  ref = O_element
FEATURE [App::DocumentObjectGroupPython] G4_DNA_CYTIDINE  # scripted group (container) (typed FeaturePython)
  Dunit = g/cm3
  Dvalue = 1
  Group = -> [H_element131,C_element141,N_element061,O_element122]
  conduct = 2
  density = 1
  expand = 3
  formula = G4_DNA_CYTIDINE
  name = G4_DNA_CYTIDINE
  specific = 4
FEATURE [App::DocumentObjectGroupPython] H_element132  label="H_element : 079"  # scripted group (container) (typed FeaturePython)
  n = 9
  ref = H_element
FEATURE [App::DocumentObjectGroupPython] C_element142  label="C_element : 087"  # scripted group (container) (typed FeaturePython)
  n = 9
  ref = C_element
FEATURE [App::DocumentObjectGroupPython] N_element062  label="N_element : 034"  # scripted group (container) (typed FeaturePython)
  n = 2
  ref = N_element
FEATURE [App::DocumentObjectGroupPython] O_element123  label="O_element : 076"  # scripted group (container) (typed FeaturePython)
  n = 6
  ref = O_element
FEATURE [App::DocumentObjectGroupPython] G4_DNA_URIDINE  # scripted group (container) (typed FeaturePython)
  Dunit = g/cm3
  Dvalue = 1
  Group = -> [H_element132,C_element142,N_element062,O_element123]
  conduct = 2
  density = 1
  expand = 3
  formula = G4_DNA_URIDINE
  name = G4_DNA_URIDINE
  specific = 4
FEATURE [App::DocumentObjectGroupPython] H_element133  label="H_element : 080"  # scripted group (container) (typed FeaturePython)
  n = 11
  ref = H_element
FEATURE [App::DocumentObjectGroupPython] C_element143  label="C_element : 088"  # scripted group (container) (typed FeaturePython)
  n = 10
  ref = C_element
FEATURE [App::DocumentObjectGroupPython] N_element063  label="N_element : 035"  # scripted group (container) (typed FeaturePython)
  n = 2
  ref = N_element
FEATURE [App::DocumentObjectGroupPython] O_element124  label="O_element : 077"  # scripted group (container) (typed FeaturePython)
  n = 6
  ref = O_element
FEATURE [App::DocumentObjectGroupPython] G4_DNA_METHYLURIDINE  # scripted group (container) (typed FeaturePython)
  Dunit = g/cm3
  Dvalue = 1
  Group = -> [H_element133,C_element143,N_element063,O_element124]
  conduct = 2
  density = 1
  expand = 3
  formula = G4_DNA_METHYLURIDINE
  name = G4_DNA_METHYLURIDINE
  specific = 4
FEATURE [App::DocumentObjectGroupPython] P_element014  label="P_element : 003"  # scripted group (container) (typed FeaturePython)
  n = 1
  ref = P_element
FEATURE [App::DocumentObjectGroupPython] O_element125  label="O_element : 078"  # scripted group (container) (typed FeaturePython)
  n = 3
  ref = O_element
FEATURE [App::DocumentObjectGroupPython] G4_DNA_MONOPHOSPHATE  # scripted group (container) (typed FeaturePython)
  Dunit = g/cm3
  Dvalue = 1
  Group = -> [P_element014,O_element125]
  conduct = 2
  density = 1
  expand = 3
  formula = G4_DNA_MONOPHOSPHATE
  name = G4_DNA_MONOPHOSPHATE
  specific = 4
FEATURE [App::DocumentObjectGroupPython] H_element134  label="H_element : 081"  # scripted group (container) (typed FeaturePython)
  n = 10
  ref = H_element
FEATURE [App::DocumentObjectGroupPython] C_element144  label="C_element : 089"  # scripted group (container) (typed FeaturePython)
  n = 10
  ref = C_element
FEATURE [App::DocumentObjectGroupPython] N_element064  label="N_element : 036"  # scripted group (container) (typed FeaturePython)
  n = 5
  ref = N_element
FEATURE [App::DocumentObjectGroupPython] O_element126  label="O_element : 079"  # scripted group (container) (typed FeaturePython)
  n = 7
  ref = O_element
FEATURE [App::DocumentObjectGroupPython] P_element015  label="P_element : 004"  # scripted group (container) (typed FeaturePython)
  n = 1
  ref = P_element
FEATURE [App::DocumentObjectGroupPython] G4_DNA_A  # scripted group (container) (typed FeaturePython)
  Dunit = g/cm3
  Dvalue = 1
  Group = -> [H_element134,C_element144,N_element064,O_element126,P_element015]
  conduct = 2
  density = 1
  expand = 3
  formula = G4_DNA_A
  name = G4_DNA_A
  specific = 4
FEATURE [App::DocumentObjectGroupPython] H_element135  label="H_element : 082"  # scripted group (container) (typed FeaturePython)
  n = 10
  ref = H_element
FEATURE [App::DocumentObjectGroupPython] C_element145  label="C_element : 090"  # scripted group (container) (typed FeaturePython)
  n = 10
  ref = C_element
FEATURE [App::DocumentObjectGroupPython] N_element065  label="N_element : 037"  # scripted group (container) (typed FeaturePython)
  n = 5
  ref = N_element
FEATURE [App::DocumentObjectGroupPython] O_element127  label="O_element : 8"  # scripted group (container) (typed FeaturePython)
  n = 8
  ref = O_element
FEATURE [App::DocumentObjectGroupPython] P_element016  label="P_element : 005"  # scripted group (container) (typed FeaturePython)
  n = 1
  ref = P_element
FEATURE [App::DocumentObjectGroupPython] G4_DNA_G  # scripted group (container) (typed FeaturePython)
  Dunit = g/cm3
  Dvalue = 1
  Group = -> [H_element135,C_element145,N_element065,O_element127,P_element016]
  conduct = 2
  density = 1
  expand = 3
  formula = G4_DNA_G
  name = G4_DNA_G
  specific = 4
FEATURE [App::DocumentObjectGroupPython] H_element136  label="H_element : 083"  # scripted group (container) (typed FeaturePython)
  n = 10
  ref = H_element
FEATURE [App::DocumentObjectGroupPython] C_element146  label="C_element : 091"  # scripted group (container) (typed FeaturePython)
  n = 9
  ref = C_element
FEATURE [App::DocumentObjectGroupPython] N_element066  label="N_element : 038"  # scripted group (container) (typed FeaturePython)
  n = 3
  ref = N_element
FEATURE [App::DocumentObjectGroupPython] O_element128  label="O_element : 080"  # scripted group (container) (typed FeaturePython)
  n = 8
  ref = O_element
FEATURE [App::DocumentObjectGroupPython] P_element017  label="P_element : 006"  # scripted group (container) (typed FeaturePython)
  n = 1
  ref = P_element
FEATURE [App::DocumentObjectGroupPython] G4_DNA_C  # scripted group (container) (typed FeaturePython)
  Dunit = g/cm3
  Dvalue = 1
  Group = -> [H_element136,C_element146,N_element066,O_element128,P_element017]
  conduct = 2
  density = 1
  expand = 3
  formula = G4_DNA_C
  name = G4_DNA_C
  specific = 4
FEATURE [App::DocumentObjectGroupPython] H_element137  label="H_element : 084"  # scripted group (container) (typed FeaturePython)
  n = 9
  ref = H_element
FEATURE [App::DocumentObjectGroupPython] C_element147  label="C_element : 092"  # scripted group (container) (typed FeaturePython)
  n = 9
  ref = C_element
FEATURE [App::DocumentObjectGroupPython] N_element067  label="N_element : 039"  # scripted group (container) (typed FeaturePython)
  n = 2
  ref = N_element
FEATURE [App::DocumentObjectGroupPython] O_element129  label="O_element : 9"  # scripted group (container) (typed FeaturePython)
  n = 9
  ref = O_element
FEATURE [App::DocumentObjectGroupPython] P_element018  label="P_element : 007"  # scripted group (container) (typed FeaturePython)
  n = 1
  ref = P_element
FEATURE [App::DocumentObjectGroupPython] G4_DNA_U  # scripted group (container) (typed FeaturePython)
  Dunit = g/cm3
  Dvalue = 1
  Group = -> [H_element137,C_element147,N_element067,O_element129,P_element018]
  conduct = 2
  density = 1
  expand = 3
  formula = G4_DNA_U
  name = G4_DNA_U
  specific = 4
FEATURE [App::DocumentObjectGroupPython] H_element138  label="H_element : 085"  # scripted group (container) (typed FeaturePython)
  n = 11
  ref = H_element
FEATURE [App::DocumentObjectGroupPython] C_element148  label="C_element : 093"  # scripted group (container) (typed FeaturePython)
  n = 10
  ref = C_element
FEATURE [App::DocumentObjectGroupPython] N_element068  label="N_element : 040"  # scripted group (container) (typed FeaturePython)
  n = 2
  ref = N_element
FEATURE [App::DocumentObjectGroupPython] O_element130  label="O_element : 081"  # scripted group (container) (typed FeaturePython)
  n = 9
  ref = O_element
FEATURE [App::DocumentObjectGroupPython] P_element019  label="P_element : 008"  # scripted group (container) (typed FeaturePython)
  n = 1
  ref = P_element
FEATURE [App::DocumentObjectGroupPython] G4_DNA_MU  # scripted group (container) (typed FeaturePython)
  Dunit = g/cm3
  Dvalue = 1
  Group = -> [H_element138,C_element148,N_element068,O_element130,P_element019]
  conduct = 2
  density = 1
  expand = 3
  formula = G4_DNA_MU
  name = G4_DNA_MU
  specific = 4
FEATURE [App::DocumentObjectGroupPython] BioChemical  # scripted group (container) (typed FeaturePython)
  Group = -> [G4_CYTOSINE,G4_THYMINE,G4_URACIL,G4_DNA_ADENINE,G4_DNA_GUANINE,G4_DNA_CYTOSINE,G4_DNA_THYMINE,G4_DNA_URACIL,G4_DNA_ADENOSINE,G4_DNA_GUANOSINE,G4_DNA_CYTIDINE,G4_DNA_URIDINE,G4_DNA_METHYLURIDINE,G4_DNA_MONOPHOSPHATE,G4_DNA_A,G4_DNA_G,G4_DNA_C,G4_DNA_U,G4_DNA_MU]
FEATURE [App::DocumentObjectGroupPython] G4Materials  # scripted group (container) (typed FeaturePython)
  Group = -> [NIST,Element,HEP,Space,BioChemical]
  version = 1
FEATURE [App::DocumentObjectGroupPython] Geant4  # scripted group (container) (typed FeaturePython)
  Group = -> [G4Isotopes,G4Elements,G4Materials]
FEATURE [App::DocumentObjectGroupPython] Materials  # scripted group (container) (typed FeaturePython)
  Group = -> [Geant4]
FEATURE [Part::FeaturePython] GDMLBox_WorldBox  # WARN: FeaturePython — macro-defined, semantics opaque (R4)
  lunit = 2
  material = 5
  x = 200
  y = 200
  z = 200
FEATURE [Sketcher::SketchObject] Sketch
  ArcFitTolerance = 0
  FullyConstrained = false
  MakeInternals = false
  sketch-geometry (5):
    g0: ArcOfHyperbola CenterX=-23.607 CenterY=7.125 CenterZ=0 NormalX=0 NormalY=0 NormalZ=1 MajorRadius=20.1608 MinorRadius=14.3903 AngleXU=-0.133002 StartAngle=-1.4336 EndAngle=1.4079
    g1: LineSegment [constr] StartX=-3.62428 StartY=4.45146 StartZ=0 EndX=-43.5897 EndY=9.79853 EndZ=0
    g2: LineSegment [constr] StartX=-1.71598 StartY=18.7146 StartZ=0 EndX=-5.53258 EndY=-9.81171 EndZ=0
    g3: GeomPoint [constr] X=0.943907 Y=3.84028 Z=0
    g4: LineSegment StartX=23.3422 StartY=28.7386 StartZ=0 EndX=16.9028 EndY=-27.0075 EndZ=0
  constraints (5):
    c: InternalAlignment(g1,g0)
    c: InternalAlignment(g2,g0)
    c: InternalAlignment(g3,g0)
    c: Coincident(g4,g0)
    c: Coincident(g4,g0)
FEATURE [Part::Extrusion] Extrude
  Base = -> Sketch
  Dir = (0,0,1)
  DirMode = 2
  FaceMakerClass = Part::FaceMakerBullseye
  FaceMakerMode = 3
  LengthFwd = 10
  LengthRev = 0
  Solid = true
  Symmetric = false
FEATURE [App::Part] Part
  Group = -> [Sketch,Extrude]
  Origin = -> Origin001
  material = 5
FEATURE [App::Part] worldVOL
  Group = -> [GDMLBox_WorldBox,Part]
  Origin = -> Origin
